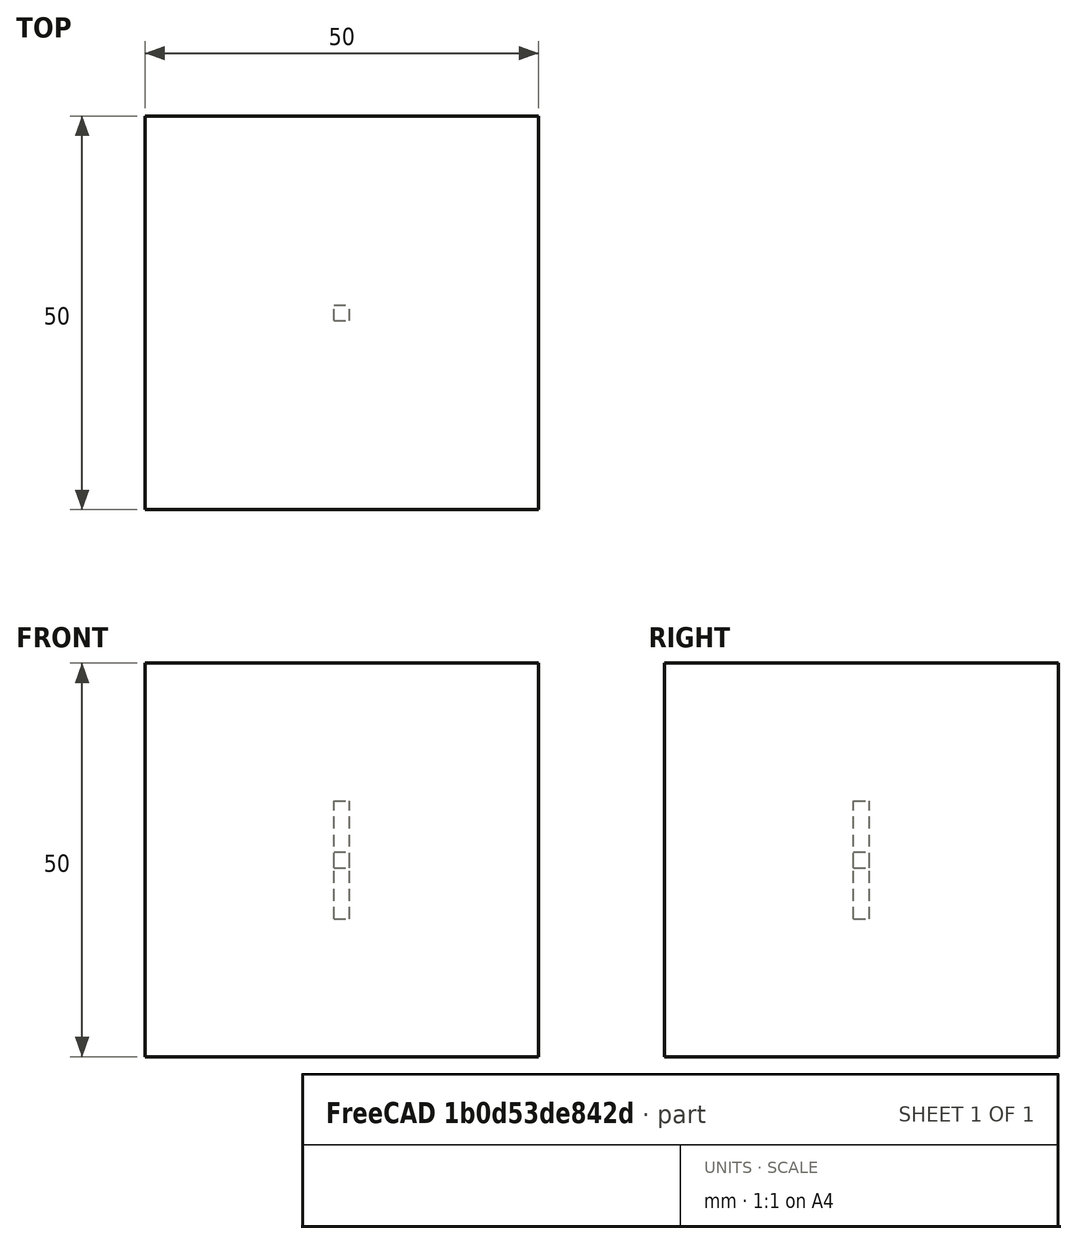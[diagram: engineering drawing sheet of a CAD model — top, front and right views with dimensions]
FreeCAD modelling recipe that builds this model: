
FCSTD DOCUMENT  (FreeCAD 0.20R29177 (Git))
Label: Expanded_simple_array
License: All rights reserved
LicenseURL: http://en.wikipedia.org/wiki/All_rights_reserved
objects: App::DocumentObjectGroupPython×1269, Part::FeaturePython×6, App::Part×6, App::Link×4, App::FeaturePython×2
note: 5 computed .brp shape members not serialized (recipe doc carries the construction recipe); baked Part::Feature solids carry a one-line shape summary decoded from their .brp

FEATURE [App::DocumentObjectGroupPython] Constants  # scripted group (container) (typed FeaturePython)
FEATURE [App::DocumentObjectGroupPython] Variables  # scripted group (container) (typed FeaturePython)
FEATURE [App::DocumentObjectGroupPython] Quantities  # scripted group (container) (typed FeaturePython)
FEATURE [App::DocumentObjectGroupPython] Isotopes  # scripted group (container) (typed FeaturePython)
FEATURE [App::DocumentObjectGroupPython] Elements  # scripted group (container) (typed FeaturePython)
FEATURE [App::DocumentObjectGroupPython] G4_CESIUM_IODIDE  label="G4_CESIUM_IODIDE : 1.000"  # scripted group (container) (typed FeaturePython)
  n = 1
FEATURE [App::DocumentObjectGroupPython] LYSO  # scripted group (container) (typed FeaturePython)
  ABSLENGTH = ABSLENGTHLAR
  Dunit = g/cm3
  Dvalue = 7.1
  FASTCOMPONENT = SCINTLAR
  Group = -> [G4_CESIUM_IODIDE]
  RAYLEIGH = RAYLEIGHLAR
  REEMISSIONPROB = SCINTLAR
  RESOLUTIONSCALE = RS
  RINDEX = RINDEXLAR
  SCINTILLATIONCOMPONENT1 = SCINTLAR
  SCINTILLATIONCOMPONENT2 = SCINTLAR
  SCINTILLATIONTIMECONSTANT1 = FTC
  SCINTILLATIONTIMECONSTANT2 = STC
  SCINTILLATIONYIELD = SY
  SCINTILLATIONYIELD1 = RY1
  SCINTILLATIONYIELD2 = RY2
  SLOWCOMPONENT = SCINTLAR
  YIELDRATIO = YR
  conduct = 2
  density = 1
  expand = 3
  name = LYSO
  specific = 4
FEATURE [App::DocumentObjectGroupPython] G4_AIR  label="G4_AIR : 1.000"  # scripted group (container) (typed FeaturePython)
  n = 1
FEATURE [App::DocumentObjectGroupPython] Air  # scripted group (container) (typed FeaturePython)
  Dunit = mg/cm3
  Dvalue = 1.29
  Group = -> [G4_AIR]
  RINDEX = AirRINDEX
  conduct = 2
  density = 1
  expand = 3
  name = Air
  specific = 4
FEATURE [App::DocumentObjectGroupPython] G4_SILICON_DIOXIDE  label="G4_SILICON_DIOXIDE : 1.000"  # scripted group (container) (typed FeaturePython)
  n = 1
FEATURE [App::DocumentObjectGroupPython] Glass  # scripted group (container) (typed FeaturePython)
  Dunit = g/cm3
  Dvalue = 2.32
  Group = -> [G4_SILICON_DIOXIDE]
  RINDEX = RINDEXLAR
  conduct = 2
  density = 1
  expand = 3
  name = Glass
  specific = 4
FEATURE [App::DocumentObjectGroupPython] SY  # scripted group (container) (typed FeaturePython)
  coldim = 1
  values = 100000
FEATURE [App::DocumentObjectGroupPython] RS  # scripted group (container) (typed FeaturePython)
  coldim = 1
  values = 1
FEATURE [App::DocumentObjectGroupPython] FTC  # scripted group (container) (typed FeaturePython)
  coldim = 1
  values = 21.5*ns
FEATURE [App::DocumentObjectGroupPython] STC  # scripted group (container) (typed FeaturePython)
  coldim = 1
  values = 43.8*ns
FEATURE [App::DocumentObjectGroupPython] RY1  # scripted group (container) (typed FeaturePython)
  coldim = 1
  values = 95
FEATURE [App::DocumentObjectGroupPython] RY2  # scripted group (container) (typed FeaturePython)
  coldim = 1
  values = 5
FEATURE [App::DocumentObjectGroupPython] YR  # scripted group (container) (typed FeaturePython)
  coldim = 1
  values = 0.8
FEATURE [App::DocumentObjectGroupPython] SCINTLAR  # scripted group (container) (typed FeaturePython)
  coldim = 2
  values = <blob: 2358 chars omitted>
FEATURE [App::DocumentObjectGroupPython] RINDEXLAR  # scripted group (container) (typed FeaturePython)
  coldim = 2
  values = <blob: 9384 chars omitted>
FEATURE [App::DocumentObjectGroupPython] ABSLENGTHLAR  # scripted group (container) (typed FeaturePython)
  coldim = 2
  values = 7.74901*eV 10.0*m 7.77525*eV 10.0*m 7.80167*eV 10.0*m 7.82827*eV 10.0*m 7.85506*eV 10.0*m 7.88202*eV 10.0*m 7.90917*eV 10.0*m 7.93651*eV 10.0*m 7.96404*eV 10.0*m 7.99176*eV 10.0*m 8.01968*eV 10.0*m 8.04779*eV 10.0*m 8.07609*eV 10.0*m 8.1046*eV 10.0*m 8.13331*eV 10.0*m 8.16222*eV 10.0*m 8.19134*eV 10.0*m 8.22067*eV 10.0*m 8.25021*eV 10.0*m 8.27996*eV 10.0*m 8.30993*eV 10.0*m 8.34012*eV 10.0*m 8.37052*eV 10.0*m 8.40115*eV 10.0*m 8.432*eV 10.0*m 8.46308*eV 10.0*m 8.4944*eV 10.0*m 8.52594*eV 10.0*m 8.55772*eV 10.0*m 8.58973*eV 10.0*m 8.62199*eV 10.0*m 8.65449*eV 10.0*m 8.68723*eV 10.0*m 8.72023*eV 10.0*m 8.75347*eV 10.0*m 8.78697*eV 10.0*m 8.82073*eV 10.0*m 8.85475*eV 10.0*m 8.88903*eV 10.0*m 8.92358*eV 10.0*m 8.9584*eV 10.0*m 8.99349*eV 10.0*m 9.02885*eV 10.0*m 9.0645*eV 10.0*m 9.10043*eV 10.0*m 9.13664*eV 10.0*m 9.17314*eV 10.0*m 9.20994*eV 10.0*m 9.24703*eV 10.0*m 9.28442*eV 10.0*m 9.32212*eV 10.0*m 9.36012*eV 10.0*m 9.39844*eV 10.0*m 9.43707*eV 10.0*m 9.47602*eV 10.0*m 9.51529*eV 10.0*m 9.55489*eV 10.0*m 9.59481*eV 10.0*m 9.63508*eV 10.0*m 9.67568*eV 10.0*m 9.71663*eV 10.0*m 9.75792*eV 10.0*m 9.79957*eV 10.0*m 9.84158*eV 10.0*m 9.88394*eV 10.0*m 9.92668*eV 10.0*m 9.96978*eV 10.0*m 10.0133*eV 10.0*m 10.0571*eV 10.0*m 10.1014*eV 10.0*m 10.146*eV 10.0*m 10.191*eV 10.0*m 10.2365*eV 10.0*m 10.2823*eV 10.0*m 10.3286*eV 10.0*m 10.3752*eV 10.0*m 10.4223*eV 10.0*m 10.4699*eV 10.0*m 10.5178*eV 10.0*m 10.5662*eV 10.0*m 10.6151*eV 10.0*m 10.6644*eV 10.0*m 10.7142*eV 10.0*m 10.7644*eV 10.0*m 10.8151*eV 10.0*m 10.8663*eV 10.0*m 10.9179*eV 10.0*m 10.9701*eV 10.0*m 11.0228*eV 10.0*m 11.076*eV 10.0*m 11.1296*eV 10.0*m 11.1839*eV 10.0*m 11.2386*eV 10.0*m 11.2939*eV 10.0*m 11.3497*eV 10.0*m 11.4061*eV 10.0*m 11.463*eV 10.0*m 11.5206*eV 10.0*m 11.5787*eV 10.0*m 11.6373*eV 10.0*m
FEATURE [App::DocumentObjectGroupPython] RAYLEIGHLAR  # scripted group (container) (typed FeaturePython)
  coldim = 2
  values = 7.74901*eV 90.0*cm 7.77525*eV 90.0*cm 7.80167*eV 90.0*cm 7.82827*eV 90.0*cm 7.85506*eV 90.0*cm 7.88202*eV 90.0*cm 7.90917*eV 90.0*cm 7.93651*eV 90.0*cm 7.96404*eV 90.0*cm 7.99176*eV 90.0*cm 8.01968*eV 90.0*cm 8.04779*eV 90.0*cm 8.07609*eV 90.0*cm 8.1046*eV 90.0*cm 8.13331*eV 90.0*cm 8.16222*eV 90.0*cm 8.19134*eV 90.0*cm 8.22067*eV 90.0*cm 8.25021*eV 90.0*cm 8.27996*eV 90.0*cm 8.30993*eV 90.0*cm 8.34012*eV 90.0*cm 8.37052*eV 90.0*cm 8.40115*eV 90.0*cm 8.432*eV 90.0*cm 8.46308*eV 90.0*cm 8.4944*eV 90.0*cm 8.52594*eV 90.0*cm 8.55772*eV 90.0*cm 8.58973*eV 90.0*cm 8.62199*eV 90.0*cm 8.65449*eV 90.0*cm 8.68723*eV 90.0*cm 8.72023*eV 90.0*cm 8.75347*eV 90.0*cm 8.78697*eV 90.0*cm 8.82073*eV 90.0*cm 8.85475*eV 90.0*cm 8.88903*eV 90.0*cm 8.92358*eV 90.0*cm 8.9584*eV 90.0*cm 8.99349*eV 90.0*cm 9.02885*eV 90.0*cm 9.0645*eV 90.0*cm 9.10043*eV 90.0*cm 9.13664*eV 90.0*cm 9.17314*eV 90.0*cm 9.20994*eV 90.0*cm 9.24703*eV 90.0*cm 9.28442*eV 90.0*cm 9.32212*eV 90.0*cm 9.36012*eV 90.0*cm 9.39844*eV 90.0*cm 9.43707*eV 90.0*cm 9.47602*eV 90.0*cm 9.51529*eV 90.0*cm 9.55489*eV 90.0*cm 9.59481*eV 90.0*cm 9.63508*eV 90.0*cm 9.67568*eV 90.0*cm 9.71663*eV 90.0*cm 9.75792*eV 90.0*cm 9.79957*eV 90.0*cm 9.84158*eV 90.0*cm 9.88394*eV 90.0*cm 9.92668*eV 90.0*cm 9.96978*eV 90.0*cm 10.0133*eV 90.0*cm 10.0571*eV 90.0*cm 10.1014*eV 90.0*cm 10.146*eV 90.0*cm 10.191*eV 90.0*cm 10.2365*eV 90.0*cm 10.2823*eV 90.0*cm 10.3286*eV 90.0*cm 10.3752*eV 90.0*cm 10.4223*eV 90.0*cm 10.4699*eV 90.0*cm 10.5178*eV 90.0*cm 10.5662*eV 90.0*cm 10.6151*eV 90.0*cm 10.6644*eV 90.0*cm 10.7142*eV 90.0*cm 10.7644*eV 90.0*cm 10.8151*eV 90.0*cm 10.8663*eV 90.0*cm 10.9179*eV 90.0*cm 10.9701*eV 90.0*cm 11.0228*eV 90.0*cm 11.076*eV 90.0*cm 11.1296*eV 90.0*cm 11.1839*eV 90.0*cm 11.2386*eV 90.0*cm 11.2939*eV 90.0*cm 11.3497*eV 90.0*cm 11.4061*eV 90.0*cm 11.463*eV 90.0*cm 11.5206*eV 90.0*cm 11.5787*eV 90.0*cm 11.6373*eV 90.0*cm
FEATURE [App::DocumentObjectGroupPython] REFLECTIVITY  # scripted group (container) (typed FeaturePython)
  coldim = 2
  values = 2.034*eV 0.98 2.068*eV 0.98 2.103*eV 0.98 2.139*eV 0.98 2.177*eV 0.98 2.216*eV 0.98 2.256*eV 0.98 2.298*eV 0.98 2.341*eV 0.98 2.386*eV 0.98 2.433*eV 0.98 2.481*eV 0.98 2.532*eV 0.98 2.585*eV 0.98 2.64*eV 0.98 2.697*eV 0.98 2.757*eV 0.98 2.82*eV 0.98 2.885*eV 0.98 2.954*eV 0.98 3.026*eV 0.98 3.102*eV 0.98 3.181*eV 0.98 3.265*eV 0.98 3.353*eV 0.98 3.446*eV 0.98 3.545*eV 0.98 3.649*eV 0.98 3.76*eV 0.98 3.877*eV 0.98 4.002*eV 0.98 4.136*eV 0.98 5.0*eV 0.98 6.0*eV 0.98 7.0*eV 0.98 8.0*eV 0.98 9.0*eV 0.98 9.0*eV 0.98 10.0*eV 0.98 11.0*eV 0.98 11.6*eV 0.98
FEATURE [App::DocumentObjectGroupPython] EFFICIENCY  # scripted group (container) (typed FeaturePython)
  coldim = 2
  values = 2.034*eV 1 2.068*eV 1 2.103*eV 1 2.139*eV 1 2.177*eV 1 2.216*eV 1 2.256*eV 1 2.298*eV 1 2.341*eV 1 2.386*eV 1 2.433*eV 1 2.481*eV 1 2.532*eV 1 2.585*eV 1 2.64*eV 1 2.697*eV 1 2.757*eV 1 2.82*eV 1 2.885*eV 1 2.954*eV 1 3.026*eV 1 3.102*eV 1 3.181*eV  1 3.265*eV 1 3.353*eV 1 3.446*eV 1 3.545*eV 1 3.649*eV 1 3.76*eV 1 3.877*eV 1 4.002*eV 1 4.136*eV 1 5.0*eV 1 6.0*eV 1 7.0*eV 1 8.0*eV 1 9.0*eV 1 9.0*eV 1 10.0*eV 1 11.0*eV 1 11.6*eV 1
FEATURE [App::DocumentObjectGroupPython] AirRINDEX  # scripted group (container) (typed FeaturePython)
  coldim = 2
  values = 2.034*eV 1 2.068*eV 1 2.103*eV 1 2.139*eV 1 2.177*eV 1 2.216*eV 1 2.256*eV 1 2.298*eV 1 2.341*eV 1 2.386*eV 1 2.433*eV 1 2.481*eV 1 2.532*eV 1 2.585*eV 1 2.64*eV 1 2.697*eV 1 2.757*eV 1 2.82*eV 1 2.885*eV 1 2.954*eV 1 3.026*eV 1 3.102*eV 1 3.181*eV 1 3.265*eV 1 3.353*eV 1 3.446*eV 1 3.545*eV 1 3.649*eV 1 3.76*eV 1 3.877*eV 1 4.002*eV 1 4.136*eV 1 5.0*eV 1 6.0*eV 1 7.0*eV 1 8.0*eV 1 9.0*eV 1 10.0*eV 1 11.0*eV 1 11.6*eV 1
FEATURE [App::DocumentObjectGroupPython] Matrix  # scripted group (container) (typed FeaturePython)
  Group = -> [SY,RS,FTC,STC,RY1,RY2,YR,SCINTLAR,RINDEXLAR,ABSLENGTHLAR,RAYLEIGHLAR,REFLECTIVITY,EFFICIENCY,AirRINDEX]
FEATURE [App::DocumentObjectGroupPython] ScintWrap  # scripted group (container) (typed FeaturePython)
  EFFICIENCY = EFFICIENCY
  REFLECTIVITY = REFLECTIVITY
  finish = 39
  model = 0
  type = 2
  value = 1
FEATURE [App::DocumentObjectGroupPython] Surfaces  # scripted group (container) (typed FeaturePython)
  Group = -> [ScintWrap]
FEATURE [App::DocumentObjectGroupPython] Opticals  # scripted group (container) (typed FeaturePython)
  Group = -> [Matrix,Surfaces]
FEATURE [App::DocumentObjectGroupPython] G4Isotopes  # scripted group (container) (typed FeaturePython)
FEATURE [App::DocumentObjectGroupPython] H_element  # scripted group (container) (typed FeaturePython)
  Z = 1
  atom_value = 1.008
  formula = H
  name = H_element
FEATURE [App::DocumentObjectGroupPython] He_element  # scripted group (container) (typed FeaturePython)
  Z = 2
  atom_value = 4.0026
  formula = He
  name = He_element
FEATURE [App::DocumentObjectGroupPython] Li_element  # scripted group (container) (typed FeaturePython)
  Z = 3
  atom_value = 6.94
  formula = Li
  name = Li_element
FEATURE [App::DocumentObjectGroupPython] Be_element  # scripted group (container) (typed FeaturePython)
  Z = 4
  atom_value = 9.01218
  formula = Be
  name = Be_element
FEATURE [App::DocumentObjectGroupPython] B_element  # scripted group (container) (typed FeaturePython)
  Z = 5
  atom_value = 10.81
  formula = B
  name = B_element
FEATURE [App::DocumentObjectGroupPython] C_element  # scripted group (container) (typed FeaturePython)
  Z = 6
  atom_value = 12.011
  formula = C
  name = C_element
FEATURE [App::DocumentObjectGroupPython] N_element  # scripted group (container) (typed FeaturePython)
  Z = 7
  atom_value = 14.007
  formula = N
  name = N_element
FEATURE [App::DocumentObjectGroupPython] O_element  # scripted group (container) (typed FeaturePython)
  Z = 8
  atom_value = 15.999
  formula = O
  name = O_element
FEATURE [App::DocumentObjectGroupPython] F_element  # scripted group (container) (typed FeaturePython)
  Z = 9
  atom_value = 18.9984
  formula = F
  name = F_element
FEATURE [App::DocumentObjectGroupPython] Ne_element  # scripted group (container) (typed FeaturePython)
  Z = 10
  atom_value = 20.1797
  formula = Ne
  name = Ne_element
FEATURE [App::DocumentObjectGroupPython] Na_element  # scripted group (container) (typed FeaturePython)
  Z = 11
  atom_value = 22.9898
  formula = Na
  name = Na_element
FEATURE [App::DocumentObjectGroupPython] Mg_element  # scripted group (container) (typed FeaturePython)
  Z = 12
  atom_value = 24.305
  formula = Mg
  name = Mg_element
FEATURE [App::DocumentObjectGroupPython] Al_element  # scripted group (container) (typed FeaturePython)
  Z = 13
  atom_value = 26.9815
  formula = Al
  name = Al_element
FEATURE [App::DocumentObjectGroupPython] Si_element  # scripted group (container) (typed FeaturePython)
  Z = 14
  atom_value = 28.085
  formula = Si
  name = Si_element
FEATURE [App::DocumentObjectGroupPython] P_element  # scripted group (container) (typed FeaturePython)
  Z = 15
  atom_value = 30.9738
  formula = P
  name = P_element
FEATURE [App::DocumentObjectGroupPython] S_element  # scripted group (container) (typed FeaturePython)
  Z = 16
  atom_value = 32.06
  formula = S
  name = S_element
FEATURE [App::DocumentObjectGroupPython] Cl_element  # scripted group (container) (typed FeaturePython)
  Z = 17
  atom_value = 35.45
  formula = Cl
  name = Cl_element
FEATURE [App::DocumentObjectGroupPython] Ar_element  # scripted group (container) (typed FeaturePython)
  Z = 18
  atom_value = 39.95
  formula = Ar
  name = Ar_element
FEATURE [App::DocumentObjectGroupPython] K_element  # scripted group (container) (typed FeaturePython)
  Z = 19
  atom_value = 39.0983
  formula = K
  name = K_element
FEATURE [App::DocumentObjectGroupPython] Ca_element  # scripted group (container) (typed FeaturePython)
  Z = 20
  atom_value = 40.078
  formula = Ca
  name = Ca_element
FEATURE [App::DocumentObjectGroupPython] Sc_element  # scripted group (container) (typed FeaturePython)
  Z = 21
  atom_value = 44.9559
  formula = Sc
  name = Sc_element
FEATURE [App::DocumentObjectGroupPython] Ti_element  # scripted group (container) (typed FeaturePython)
  Z = 22
  atom_value = 47.867
  formula = Ti
  name = Ti_element
FEATURE [App::DocumentObjectGroupPython] V_element  # scripted group (container) (typed FeaturePython)
  Z = 23
  atom_value = 50.9415
  formula = V
  name = V_element
FEATURE [App::DocumentObjectGroupPython] Cr_element  # scripted group (container) (typed FeaturePython)
  Z = 24
  atom_value = 51.9961
  formula = Cr
  name = Cr_element
FEATURE [App::DocumentObjectGroupPython] Mn_element  # scripted group (container) (typed FeaturePython)
  Z = 25
  atom_value = 54.938
  formula = Mn
  name = Mn_element
FEATURE [App::DocumentObjectGroupPython] Fe_element  # scripted group (container) (typed FeaturePython)
  Z = 26
  atom_value = 55.845
  formula = Fe
  name = Fe_element
FEATURE [App::DocumentObjectGroupPython] Co_element  # scripted group (container) (typed FeaturePython)
  Z = 27
  atom_value = 58.9332
  formula = Co
  name = Co_element
FEATURE [App::DocumentObjectGroupPython] Ni_element  # scripted group (container) (typed FeaturePython)
  Z = 28
  atom_value = 58.6934
  formula = Ni
  name = Ni_element
FEATURE [App::DocumentObjectGroupPython] Cu_element  # scripted group (container) (typed FeaturePython)
  Z = 29
  atom_value = 63.546
  formula = Cu
  name = Cu_element
FEATURE [App::DocumentObjectGroupPython] Zn_element  # scripted group (container) (typed FeaturePython)
  Z = 30
  atom_value = 65.38
  formula = Zn
  name = Zn_element
FEATURE [App::DocumentObjectGroupPython] Ga_element  # scripted group (container) (typed FeaturePython)
  Z = 31
  atom_value = 69.723
  formula = Ga
  name = Ga_element
FEATURE [App::DocumentObjectGroupPython] Ge_element  # scripted group (container) (typed FeaturePython)
  Z = 32
  atom_value = 72.63
  formula = Ge
  name = Ge_element
FEATURE [App::DocumentObjectGroupPython] As_element  # scripted group (container) (typed FeaturePython)
  Z = 33
  atom_value = 74.9216
  formula = As
  name = As_element
FEATURE [App::DocumentObjectGroupPython] Se_element  # scripted group (container) (typed FeaturePython)
  Z = 34
  atom_value = 78.971
  formula = Se
  name = Se_element
FEATURE [App::DocumentObjectGroupPython] Br_element  # scripted group (container) (typed FeaturePython)
  Z = 35
  atom_value = 79.904
  formula = Br
  name = Br_element
FEATURE [App::DocumentObjectGroupPython] Kr_element  # scripted group (container) (typed FeaturePython)
  Z = 36
  atom_value = 83.798
  formula = Kr
  name = Kr_element
FEATURE [App::DocumentObjectGroupPython] Rb_element  # scripted group (container) (typed FeaturePython)
  Z = 37
  atom_value = 85.4678
  formula = Rb
  name = Rb_element
FEATURE [App::DocumentObjectGroupPython] Sr_element  # scripted group (container) (typed FeaturePython)
  Z = 38
  atom_value = 87.62
  formula = Sr
  name = Sr_element
FEATURE [App::DocumentObjectGroupPython] Y_element  # scripted group (container) (typed FeaturePython)
  Z = 39
  atom_value = 88.9058
  formula = Y
  name = Y_element
FEATURE [App::DocumentObjectGroupPython] Zr_element  # scripted group (container) (typed FeaturePython)
  Z = 40
  atom_value = 91.224
  formula = Zr
  name = Zr_element
FEATURE [App::DocumentObjectGroupPython] Nb_element  # scripted group (container) (typed FeaturePython)
  Z = 41
  atom_value = 92.9064
  formula = Nb
  name = Nb_element
FEATURE [App::DocumentObjectGroupPython] Mo_element  # scripted group (container) (typed FeaturePython)
  Z = 42
  atom_value = 95.95
  formula = Mo
  name = Mo_element
FEATURE [App::DocumentObjectGroupPython] Tc_element  # scripted group (container) (typed FeaturePython)
  Z = 43
  atom_value = 97
  formula = Tc
  name = Tc_element
FEATURE [App::DocumentObjectGroupPython] Ru_element  # scripted group (container) (typed FeaturePython)
  Z = 44
  atom_value = 101.07
  formula = Ru
  name = Ru_element
FEATURE [App::DocumentObjectGroupPython] Rh_element  # scripted group (container) (typed FeaturePython)
  Z = 45
  atom_value = 102.905
  formula = Rh
  name = Rh_element
FEATURE [App::DocumentObjectGroupPython] Pd_element  # scripted group (container) (typed FeaturePython)
  Z = 46
  atom_value = 106.42
  formula = Pd
  name = Pd_element
FEATURE [App::DocumentObjectGroupPython] Ag_element  # scripted group (container) (typed FeaturePython)
  Z = 47
  atom_value = 107.868
  formula = Ag
  name = Ag_element
FEATURE [App::DocumentObjectGroupPython] Cd_element  # scripted group (container) (typed FeaturePython)
  Z = 48
  atom_value = 112.414
  formula = Cd
  name = Cd_element
FEATURE [App::DocumentObjectGroupPython] In_element  # scripted group (container) (typed FeaturePython)
  Z = 49
  atom_value = 114.818
  formula = In
  name = In_element
FEATURE [App::DocumentObjectGroupPython] Sn_element  # scripted group (container) (typed FeaturePython)
  Z = 50
  atom_value = 118.71
  formula = Sn
  name = Sn_element
FEATURE [App::DocumentObjectGroupPython] Sb_element  # scripted group (container) (typed FeaturePython)
  Z = 51
  atom_value = 121.76
  formula = Sb
  name = Sb_element
FEATURE [App::DocumentObjectGroupPython] Te_element  # scripted group (container) (typed FeaturePython)
  Z = 52
  atom_value = 127.6
  formula = Te
  name = Te_element
FEATURE [App::DocumentObjectGroupPython] I_element  # scripted group (container) (typed FeaturePython)
  Z = 53
  atom_value = 126.904
  formula = I
  name = I_element
FEATURE [App::DocumentObjectGroupPython] Xe_element  # scripted group (container) (typed FeaturePython)
  Z = 54
  atom_value = 131.293
  formula = Xe
  name = Xe_element
FEATURE [App::DocumentObjectGroupPython] Cs_element  # scripted group (container) (typed FeaturePython)
  Z = 55
  atom_value = 132.905
  formula = Cs
  name = Cs_element
FEATURE [App::DocumentObjectGroupPython] Ba_element  # scripted group (container) (typed FeaturePython)
  Z = 56
  atom_value = 137.327
  formula = Ba
  name = Ba_element
FEATURE [App::DocumentObjectGroupPython] La_element  # scripted group (container) (typed FeaturePython)
  Z = 57
  atom_value = 138.905
  formula = La
  name = La_element
FEATURE [App::DocumentObjectGroupPython] Ce_element  # scripted group (container) (typed FeaturePython)
  Z = 58
  atom_value = 140.116
  formula = Ce
  name = Ce_element
FEATURE [App::DocumentObjectGroupPython] Pr_element  # scripted group (container) (typed FeaturePython)
  Z = 59
  atom_value = 140.908
  formula = Pr
  name = Pr_element
FEATURE [App::DocumentObjectGroupPython] Nd_element  # scripted group (container) (typed FeaturePython)
  Z = 60
  atom_value = 144.242
  formula = Nd
  name = Nd_element
FEATURE [App::DocumentObjectGroupPython] Pm_element  # scripted group (container) (typed FeaturePython)
  Z = 61
  atom_value = 145
  formula = Pm
  name = Pm_element
FEATURE [App::DocumentObjectGroupPython] Sm_element  # scripted group (container) (typed FeaturePython)
  Z = 62
  atom_value = 150.36
  formula = Sm
  name = Sm_element
FEATURE [App::DocumentObjectGroupPython] Eu_element  # scripted group (container) (typed FeaturePython)
  Z = 63
  atom_value = 151.964
  formula = Eu
  name = Eu_element
FEATURE [App::DocumentObjectGroupPython] Gd_element  # scripted group (container) (typed FeaturePython)
  Z = 64
  atom_value = 157.25
  formula = Gd
  name = Gd_element
FEATURE [App::DocumentObjectGroupPython] Tb_element  # scripted group (container) (typed FeaturePython)
  Z = 65
  atom_value = 158.925
  formula = Tb
  name = Tb_element
FEATURE [App::DocumentObjectGroupPython] Dy_element  # scripted group (container) (typed FeaturePython)
  Z = 66
  atom_value = 162.5
  formula = Dy
  name = Dy_element
FEATURE [App::DocumentObjectGroupPython] Ho_element  # scripted group (container) (typed FeaturePython)
  Z = 67
  atom_value = 164.93
  formula = Ho
  name = Ho_element
FEATURE [App::DocumentObjectGroupPython] Er_element  # scripted group (container) (typed FeaturePython)
  Z = 68
  atom_value = 167.259
  formula = Er
  name = Er_element
FEATURE [App::DocumentObjectGroupPython] Tm_element  # scripted group (container) (typed FeaturePython)
  Z = 69
  atom_value = 168.934
  formula = Tm
  name = Tm_element
FEATURE [App::DocumentObjectGroupPython] Yb_element  # scripted group (container) (typed FeaturePython)
  Z = 70
  atom_value = 173.045
  formula = Yb
  name = Yb_element
FEATURE [App::DocumentObjectGroupPython] Lu_element  # scripted group (container) (typed FeaturePython)
  Z = 71
  atom_value = 174.967
  formula = Lu
  name = Lu_element
FEATURE [App::DocumentObjectGroupPython] Hf_element  # scripted group (container) (typed FeaturePython)
  Z = 72
  atom_value = 178.49
  formula = Hf
  name = Hf_element
FEATURE [App::DocumentObjectGroupPython] Ta_element  # scripted group (container) (typed FeaturePython)
  Z = 73
  atom_value = 180.948
  formula = Ta
  name = Ta_element
FEATURE [App::DocumentObjectGroupPython] W_element  # scripted group (container) (typed FeaturePython)
  Z = 74
  atom_value = 183.84
  formula = W
  name = W_element
FEATURE [App::DocumentObjectGroupPython] Re_element  # scripted group (container) (typed FeaturePython)
  Z = 75
  atom_value = 186.207
  formula = Re
  name = Re_element
FEATURE [App::DocumentObjectGroupPython] Os_element  # scripted group (container) (typed FeaturePython)
  Z = 76
  atom_value = 190.23
  formula = Os
  name = Os_element
FEATURE [App::DocumentObjectGroupPython] Ir_element  # scripted group (container) (typed FeaturePython)
  Z = 77
  atom_value = 192.217
  formula = Ir
  name = Ir_element
FEATURE [App::DocumentObjectGroupPython] Pt_element  # scripted group (container) (typed FeaturePython)
  Z = 78
  atom_value = 195.084
  formula = Pt
  name = Pt_element
FEATURE [App::DocumentObjectGroupPython] Au_element  # scripted group (container) (typed FeaturePython)
  Z = 79
  atom_value = 196.967
  formula = Au
  name = Au_element
FEATURE [App::DocumentObjectGroupPython] Hg_element  # scripted group (container) (typed FeaturePython)
  Z = 80
  atom_value = 200.592
  formula = Hg
  name = Hg_element
FEATURE [App::DocumentObjectGroupPython] Tl_element  # scripted group (container) (typed FeaturePython)
  Z = 81
  atom_value = 204.38
  formula = Tl
  name = Tl_element
FEATURE [App::DocumentObjectGroupPython] Pb_element  # scripted group (container) (typed FeaturePython)
  Z = 82
  atom_value = 207.2
  formula = Pb
  name = Pb_element
FEATURE [App::DocumentObjectGroupPython] Bi_element  # scripted group (container) (typed FeaturePython)
  Z = 83
  atom_value = 208.98
  formula = Bi
  name = Bi_element
FEATURE [App::DocumentObjectGroupPython] Po_element  # scripted group (container) (typed FeaturePython)
  Z = 84
  atom_value = 209
  formula = Po
  name = Po_element
FEATURE [App::DocumentObjectGroupPython] At_element  # scripted group (container) (typed FeaturePython)
  Z = 85
  atom_value = 210
  formula = At
  name = At_element
FEATURE [App::DocumentObjectGroupPython] Rn_element  # scripted group (container) (typed FeaturePython)
  Z = 86
  atom_value = 222
  formula = Rn
  name = Rn_element
FEATURE [App::DocumentObjectGroupPython] Fr_element  # scripted group (container) (typed FeaturePython)
  Z = 87
  atom_value = 223
  formula = Fr
  name = Fr_element
FEATURE [App::DocumentObjectGroupPython] Ra_element  # scripted group (container) (typed FeaturePython)
  Z = 88
  atom_value = 226
  formula = Ra
  name = Ra_element
FEATURE [App::DocumentObjectGroupPython] Ac_element  # scripted group (container) (typed FeaturePython)
  Z = 89
  atom_value = 227
  formula = Ac
  name = Ac_element
FEATURE [App::DocumentObjectGroupPython] Th_element  # scripted group (container) (typed FeaturePython)
  Z = 90
  atom_value = 232.038
  formula = Th
  name = Th_element
FEATURE [App::DocumentObjectGroupPython] Pa_element  # scripted group (container) (typed FeaturePython)
  Z = 91
  atom_value = 231.036
  formula = Pa
  name = Pa_element
FEATURE [App::DocumentObjectGroupPython] U_element  # scripted group (container) (typed FeaturePython)
  Z = 92
  atom_value = 238.029
  formula = U
  name = U_element
FEATURE [App::DocumentObjectGroupPython] Np_element  # scripted group (container) (typed FeaturePython)
  Z = 93
  atom_value = 237
  formula = Np
  name = Np_element
FEATURE [App::DocumentObjectGroupPython] Pu_element  # scripted group (container) (typed FeaturePython)
  Z = 94
  atom_value = 244
  formula = Pu
  name = Pu_element
FEATURE [App::DocumentObjectGroupPython] Am_element  # scripted group (container) (typed FeaturePython)
  Z = 95
  atom_value = 243
  formula = Am
  name = Am_element
FEATURE [App::DocumentObjectGroupPython] Cm_element  # scripted group (container) (typed FeaturePython)
  Z = 96
  atom_value = 247
  formula = Cm
  name = Cm_element
FEATURE [App::DocumentObjectGroupPython] Bk_element  # scripted group (container) (typed FeaturePython)
  Z = 97
  atom_value = 247
  formula = Bk
  name = Bk_element
FEATURE [App::DocumentObjectGroupPython] Cf_element  # scripted group (container) (typed FeaturePython)
  Z = 98
  atom_value = 251
  formula = Cf
  name = Cf_element
FEATURE [App::DocumentObjectGroupPython] G4Elements  # scripted group (container) (typed FeaturePython)
  Group = -> [H_element,He_element,Li_element,Be_element,B_element,C_element,N_element,O_element,F_element,Ne_element,Na_element,Mg_element,Al_element,Si_element,P_element,S_element,Cl_element,Ar_element,K_element,Ca_element,Sc_element,Ti_element,V_element,Cr_element,Mn_element,Fe_element,Co_element,Ni_element,Cu_element,Zn_element,Ga_element,Ge_element,As_element,Se_element,Br_element,Kr_element,Rb_element,+61 more]
FEATURE [App::DocumentObjectGroupPython] H_element001  label="H_element : 0.101"  # scripted group (container) (typed FeaturePython)
  n = 0.101327
FEATURE [App::DocumentObjectGroupPython] C_element001  label="C_element : 0.775"  # scripted group (container) (typed FeaturePython)
  n = 0.7755
FEATURE [App::DocumentObjectGroupPython] N_element001  label="N_element : 0.035"  # scripted group (container) (typed FeaturePython)
  n = 0.035057
FEATURE [App::DocumentObjectGroupPython] O_element001  label="O_element : 0.052"  # scripted group (container) (typed FeaturePython)
  n = 0.0523159
FEATURE [App::DocumentObjectGroupPython] F_element001  label="F_element : 0.017"  # scripted group (container) (typed FeaturePython)
  n = 0.017422
FEATURE [App::DocumentObjectGroupPython] Ca_element001  label="Ca_element : 0.018"  # scripted group (container) (typed FeaturePython)
  n = 0.018378
FEATURE [App::DocumentObjectGroupPython] G4_A_150_TISSUE  label="G4_A-150_TISSUE"  # scripted group (container) (typed FeaturePython)
  Dunit = g/cm3
  Dvalue = 1.127
  Group = -> [H_element001,C_element001,N_element001,O_element001,F_element001,Ca_element001]
  conduct = 2
  density = 1
  expand = 3
  formula = G4_A-150_TISSUE
  name = G4_A-150_TISSUE
  specific = 4
FEATURE [App::DocumentObjectGroupPython] C_element002  label="C_element : 3"  # scripted group (container) (typed FeaturePython)
  n = 3
  ref = C_element
FEATURE [App::DocumentObjectGroupPython] H_element002  label="H_element : 6"  # scripted group (container) (typed FeaturePython)
  n = 6
  ref = H_element
FEATURE [App::DocumentObjectGroupPython] O_element002  label="O_element : 1"  # scripted group (container) (typed FeaturePython)
  n = 1
  ref = O_element
FEATURE [App::DocumentObjectGroupPython] G4_ACETONE  # scripted group (container) (typed FeaturePython)
  Dunit = g/cm3
  Dvalue = 0.7899
  Group = -> [C_element002,H_element002,O_element002]
  conduct = 2
  density = 1
  expand = 3
  formula = G4_ACETONE
  name = G4_ACETONE
  specific = 4
FEATURE [App::DocumentObjectGroupPython] C_element003  label="C_element : 2"  # scripted group (container) (typed FeaturePython)
  n = 2
  ref = C_element
FEATURE [App::DocumentObjectGroupPython] H_element003  label="H_element : 2"  # scripted group (container) (typed FeaturePython)
  n = 2
  ref = H_element
FEATURE [App::DocumentObjectGroupPython] G4_ACETYLENE  # scripted group (container) (typed FeaturePython)
  Dunit = g/cm3
  Dvalue = 0.0010967
  Group = -> [C_element003,H_element003]
  conduct = 2
  density = 1
  expand = 3
  formula = G4_ACETYLENE
  name = G4_ACETYLENE
  specific = 4
FEATURE [App::DocumentObjectGroupPython] C_element004  label="C_element : 5"  # scripted group (container) (typed FeaturePython)
  n = 5
  ref = C_element
FEATURE [App::DocumentObjectGroupPython] H_element004  label="H_element : 5"  # scripted group (container) (typed FeaturePython)
  n = 5
  ref = H_element
FEATURE [App::DocumentObjectGroupPython] N_element002  label="N_element : 5"  # scripted group (container) (typed FeaturePython)
  n = 5
  ref = N_element
FEATURE [App::DocumentObjectGroupPython] G4_ADENINE  # scripted group (container) (typed FeaturePython)
  Dunit = g/cm3
  Dvalue = 1.6
  Group = -> [C_element004,H_element004,N_element002]
  conduct = 2
  density = 1
  expand = 3
  formula = G4_ADENINE
  name = G4_ADENINE
  specific = 4
FEATURE [App::DocumentObjectGroupPython] H_element005  label="H_element : 0.114"  # scripted group (container) (typed FeaturePython)
  n = 0.114
FEATURE [App::DocumentObjectGroupPython] C_element005  label="C_element : 0.598"  # scripted group (container) (typed FeaturePython)
  n = 0.598
FEATURE [App::DocumentObjectGroupPython] N_element003  label="N_element : 0.007"  # scripted group (container) (typed FeaturePython)
  n = 0.007
FEATURE [App::DocumentObjectGroupPython] O_element003  label="O_element : 0.278"  # scripted group (container) (typed FeaturePython)
  n = 0.278
FEATURE [App::DocumentObjectGroupPython] Na_element001  label="Na_element : 0.001"  # scripted group (container) (typed FeaturePython)
  n = 0.001
FEATURE [App::DocumentObjectGroupPython] S_element001  label="S_element : 0.001"  # scripted group (container) (typed FeaturePython)
  n = 0.001
FEATURE [App::DocumentObjectGroupPython] Cl_element001  label="Cl_element : 0.001"  # scripted group (container) (typed FeaturePython)
  n = 0.001
FEATURE [App::DocumentObjectGroupPython] G4_ADIPOSE_TISSUE_ICRP  # scripted group (container) (typed FeaturePython)
  Dunit = g/cm3
  Dvalue = 0.95
  Group = -> [H_element005,C_element005,N_element003,O_element003,Na_element001,S_element001,Cl_element001]
  conduct = 2
  density = 1
  expand = 3
  formula = G4_ADIPOSE_TISSUE_ICRP
  name = G4_ADIPOSE_TISSUE_ICRP
  specific = 4
FEATURE [App::DocumentObjectGroupPython] C_element006  label="C_element : 0.000"  # scripted group (container) (typed FeaturePython)
  n = 0.000124
FEATURE [App::DocumentObjectGroupPython] N_element004  label="N_element : 0.755"  # scripted group (container) (typed FeaturePython)
  n = 0.755268
FEATURE [App::DocumentObjectGroupPython] O_element004  label="O_element : 0.232"  # scripted group (container) (typed FeaturePython)
  n = 0.231781
FEATURE [App::DocumentObjectGroupPython] Ar_element001  label="Ar_element : 0.013"  # scripted group (container) (typed FeaturePython)
  n = 0.012827
FEATURE [App::DocumentObjectGroupPython] G4_AIR001  label="G4_AIR"  # scripted group (container) (typed FeaturePython)
  Dunit = g/cm3
  Dvalue = 0.00120479
  Group = -> [C_element006,N_element004,O_element004,Ar_element001]
  conduct = 2
  density = 1
  expand = 3
  formula = G4_AIR
  name = G4_AIR
  specific = 4
FEATURE [App::DocumentObjectGroupPython] C_element007  label="C_element : 006"  # scripted group (container) (typed FeaturePython)
  n = 3
  ref = C_element
FEATURE [App::DocumentObjectGroupPython] H_element006  label="H_element : 7"  # scripted group (container) (typed FeaturePython)
  n = 7
  ref = H_element
FEATURE [App::DocumentObjectGroupPython] N_element005  label="N_element : 1"  # scripted group (container) (typed FeaturePython)
  n = 1
  ref = N_element
FEATURE [App::DocumentObjectGroupPython] O_element005  label="O_element : 2"  # scripted group (container) (typed FeaturePython)
  n = 2
  ref = O_element
FEATURE [App::DocumentObjectGroupPython] G4_ALANINE  # scripted group (container) (typed FeaturePython)
  Dunit = g/cm3
  Dvalue = 1.42
  Group = -> [C_element007,H_element006,N_element005,O_element005]
  conduct = 2
  density = 1
  expand = 3
  formula = G4_ALANINE
  name = G4_ALANINE
  specific = 4
FEATURE [App::DocumentObjectGroupPython] Al_element001  label="Al_element : 2"  # scripted group (container) (typed FeaturePython)
  n = 2
  ref = Al_element
FEATURE [App::DocumentObjectGroupPython] O_element006  label="O_element : 3"  # scripted group (container) (typed FeaturePython)
  n = 3
  ref = O_element
FEATURE [App::DocumentObjectGroupPython] G4_ALUMINUM_OXIDE  # scripted group (container) (typed FeaturePython)
  Dunit = g/cm3
  Dvalue = 3.97
  Group = -> [Al_element001,O_element006]
  conduct = 2
  density = 1
  expand = 3
  formula = G4_ALUMINUM_OXIDE
  name = G4_ALUMINUM_OXIDE
  specific = 4
FEATURE [App::DocumentObjectGroupPython] H_element007  label="H_element : 0.106"  # scripted group (container) (typed FeaturePython)
  n = 0.10593
FEATURE [App::DocumentObjectGroupPython] C_element008  label="C_element : 0.789"  # scripted group (container) (typed FeaturePython)
  n = 0.788974
FEATURE [App::DocumentObjectGroupPython] O_element007  label="O_element : 0.105"  # scripted group (container) (typed FeaturePython)
  n = 0.105096
FEATURE [App::DocumentObjectGroupPython] G4_AMBER  # scripted group (container) (typed FeaturePython)
  Dunit = g/cm3
  Dvalue = 1.1
  Group = -> [H_element007,C_element008,O_element007]
  conduct = 2
  density = 1
  expand = 3
  formula = G4_AMBER
  name = G4_AMBER
  specific = 4
FEATURE [App::DocumentObjectGroupPython] N_element006  label="N_element : 006"  # scripted group (container) (typed FeaturePython)
  n = 1
  ref = N_element
FEATURE [App::DocumentObjectGroupPython] H_element008  label="H_element : 3"  # scripted group (container) (typed FeaturePython)
  n = 3
  ref = H_element
FEATURE [App::DocumentObjectGroupPython] G4_AMMONIA  # scripted group (container) (typed FeaturePython)
  Dunit = g/cm3
  Dvalue = 0.000826019
  Group = -> [N_element006,H_element008]
  conduct = 2
  density = 1
  expand = 3
  formula = G4_AMMONIA
  name = G4_AMMONIA
  specific = 4
FEATURE [App::DocumentObjectGroupPython] C_element009  label="C_element : 6"  # scripted group (container) (typed FeaturePython)
  n = 6
  ref = C_element
FEATURE [App::DocumentObjectGroupPython] H_element009  label="H_element : 008"  # scripted group (container) (typed FeaturePython)
  n = 7
  ref = H_element
FEATURE [App::DocumentObjectGroupPython] N_element007  label="N_element : 007"  # scripted group (container) (typed FeaturePython)
  n = 1
  ref = N_element
FEATURE [App::DocumentObjectGroupPython] G4_ANILINE  # scripted group (container) (typed FeaturePython)
  Dunit = g/cm3
  Dvalue = 1.0235
  Group = -> [C_element009,H_element009,N_element007]
  conduct = 2
  density = 1
  expand = 3
  formula = G4_ANILINE
  name = G4_ANILINE
  specific = 4
FEATURE [App::DocumentObjectGroupPython] C_element010  label="C_element : 14"  # scripted group (container) (typed FeaturePython)
  n = 14
  ref = C_element
FEATURE [App::DocumentObjectGroupPython] H_element010  label="H_element : 10"  # scripted group (container) (typed FeaturePython)
  n = 10
  ref = H_element
FEATURE [App::DocumentObjectGroupPython] G4_ANTHRACENE  # scripted group (container) (typed FeaturePython)
  Dunit = g/cm3
  Dvalue = 1.283
  Group = -> [C_element010,H_element010]
  conduct = 2
  density = 1
  expand = 3
  formula = G4_ANTHRACENE
  name = G4_ANTHRACENE
  specific = 4
FEATURE [App::DocumentObjectGroupPython] H_element011  label="H_element : 0.065"  # scripted group (container) (typed FeaturePython)
  n = 0.0654709
FEATURE [App::DocumentObjectGroupPython] C_element011  label="C_element : 0.537"  # scripted group (container) (typed FeaturePython)
  n = 0.536944
FEATURE [App::DocumentObjectGroupPython] N_element008  label="N_element : 0.021"  # scripted group (container) (typed FeaturePython)
  n = 0.0215
FEATURE [App::DocumentObjectGroupPython] O_element008  label="O_element : 0.032"  # scripted group (container) (typed FeaturePython)
  n = 0.032085
FEATURE [App::DocumentObjectGroupPython] F_element002  label="F_element : 0.167"  # scripted group (container) (typed FeaturePython)
  n = 0.167411
FEATURE [App::DocumentObjectGroupPython] Ca_element002  label="Ca_element : 0.177"  # scripted group (container) (typed FeaturePython)
  n = 0.176589
FEATURE [App::DocumentObjectGroupPython] G4_B_100_BONE  label="G4_B-100_BONE"  # scripted group (container) (typed FeaturePython)
  Dunit = g/cm3
  Dvalue = 1.45
  Group = -> [H_element011,C_element011,N_element008,O_element008,F_element002,Ca_element002]
  conduct = 2
  density = 1
  expand = 3
  formula = G4_B-100_BONE
  name = G4_B-100_BONE
  specific = 4
FEATURE [App::DocumentObjectGroupPython] H_element012  label="H_element : 0.057"  # scripted group (container) (typed FeaturePython)
  n = 0.057441
FEATURE [App::DocumentObjectGroupPython] C_element012  label="C_element : 0.790"  # scripted group (container) (typed FeaturePython)
  n = 0.774591
FEATURE [App::DocumentObjectGroupPython] O_element009  label="O_element : 0.168"  # scripted group (container) (typed FeaturePython)
  n = 0.167968
FEATURE [App::DocumentObjectGroupPython] G4_BAKELITE  # scripted group (container) (typed FeaturePython)
  Dunit = g/cm3
  Dvalue = 1.25
  Group = -> [H_element012,C_element012,O_element009]
  conduct = 2
  density = 1
  expand = 3
  formula = G4_BAKELITE
  name = G4_BAKELITE
  specific = 4
FEATURE [App::DocumentObjectGroupPython] Ba_element001  label="Ba_element : 1"  # scripted group (container) (typed FeaturePython)
  n = 1
  ref = Ba_element
FEATURE [App::DocumentObjectGroupPython] F_element003  label="F_element : 2"  # scripted group (container) (typed FeaturePython)
  n = 2
  ref = F_element
FEATURE [App::DocumentObjectGroupPython] G4_BARIUM_FLUORIDE  # scripted group (container) (typed FeaturePython)
  Dunit = g/cm3
  Dvalue = 4.89
  Group = -> [Ba_element001,F_element003]
  conduct = 2
  density = 1
  expand = 3
  formula = G4_BARIUM_FLUORIDE
  name = G4_BARIUM_FLUORIDE
  specific = 4
FEATURE [App::DocumentObjectGroupPython] Ba_element002  label="Ba_element : 002"  # scripted group (container) (typed FeaturePython)
  n = 1
  ref = Ba_element
FEATURE [App::DocumentObjectGroupPython] S_element002  label="S_element : 1"  # scripted group (container) (typed FeaturePython)
  n = 1
  ref = S_element
FEATURE [App::DocumentObjectGroupPython] O_element010  label="O_element : 4"  # scripted group (container) (typed FeaturePython)
  n = 4
  ref = O_element
FEATURE [App::DocumentObjectGroupPython] G4_BARIUM_SULFATE  # scripted group (container) (typed FeaturePython)
  Dunit = g/cm3
  Dvalue = 4.5
  Group = -> [Ba_element002,S_element002,O_element010]
  conduct = 2
  density = 1
  expand = 3
  formula = G4_BARIUM_SULFATE
  name = G4_BARIUM_SULFATE
  specific = 4
FEATURE [App::DocumentObjectGroupPython] C_element013  label="C_element : 007"  # scripted group (container) (typed FeaturePython)
  n = 6
  ref = C_element
FEATURE [App::DocumentObjectGroupPython] H_element013  label="H_element : 009"  # scripted group (container) (typed FeaturePython)
  n = 6
  ref = H_element
FEATURE [App::DocumentObjectGroupPython] G4_BENZENE  # scripted group (container) (typed FeaturePython)
  Dunit = g/cm3
  Dvalue = 0.87865
  Group = -> [C_element013,H_element013]
  conduct = 2
  density = 1
  expand = 3
  formula = G4_BENZENE
  name = G4_BENZENE
  specific = 4
FEATURE [App::DocumentObjectGroupPython] Be_element001  label="Be_element : 1"  # scripted group (container) (typed FeaturePython)
  n = 1
  ref = Be_element
FEATURE [App::DocumentObjectGroupPython] O_element011  label="O_element : 005"  # scripted group (container) (typed FeaturePython)
  n = 1
  ref = O_element
FEATURE [App::DocumentObjectGroupPython] G4_BERYLLIUM_OXIDE  # scripted group (container) (typed FeaturePython)
  Dunit = g/cm3
  Dvalue = 3.01
  Group = -> [Be_element001,O_element011]
  conduct = 2
  density = 1
  expand = 3
  formula = G4_BERYLLIUM_OXIDE
  name = G4_BERYLLIUM_OXIDE
  specific = 4
FEATURE [App::DocumentObjectGroupPython] Bi_element001  label="Bi_element : 4"  # scripted group (container) (typed FeaturePython)
  n = 4
  ref = Bi_element
FEATURE [App::DocumentObjectGroupPython] Ge_element001  label="Ge_element : 3"  # scripted group (container) (typed FeaturePython)
  n = 3
  ref = Ge_element
FEATURE [App::DocumentObjectGroupPython] O_element012  label="O_element : 12"  # scripted group (container) (typed FeaturePython)
  n = 12
  ref = O_element
FEATURE [App::DocumentObjectGroupPython] G4_BGO  # scripted group (container) (typed FeaturePython)
  Dunit = g/cm3
  Dvalue = 7.13
  Group = -> [Bi_element001,Ge_element001,O_element012]
  conduct = 2
  density = 1
  expand = 3
  formula = G4_BGO
  name = G4_BGO
  specific = 4
FEATURE [App::DocumentObjectGroupPython] H_element014  label="H_element : 0.102"  # scripted group (container) (typed FeaturePython)
  n = 0.102
FEATURE [App::DocumentObjectGroupPython] C_element014  label="C_element : 0.110"  # scripted group (container) (typed FeaturePython)
  n = 0.11
FEATURE [App::DocumentObjectGroupPython] N_element009  label="N_element : 0.033"  # scripted group (container) (typed FeaturePython)
  n = 0.033
FEATURE [App::DocumentObjectGroupPython] O_element013  label="O_element : 0.745"  # scripted group (container) (typed FeaturePython)
  n = 0.745
FEATURE [App::DocumentObjectGroupPython] Na_element002  label="Na_element : 0.002"  # scripted group (container) (typed FeaturePython)
  n = 0.001
FEATURE [App::DocumentObjectGroupPython] P_element001  label="P_element : 0.001"  # scripted group (container) (typed FeaturePython)
  n = 0.001
FEATURE [App::DocumentObjectGroupPython] S_element003  label="S_element : 0.002"  # scripted group (container) (typed FeaturePython)
  n = 0.002
FEATURE [App::DocumentObjectGroupPython] Cl_element002  label="Cl_element : 0.003"  # scripted group (container) (typed FeaturePython)
  n = 0.003
FEATURE [App::DocumentObjectGroupPython] K_element001  label="K_element : 0.002"  # scripted group (container) (typed FeaturePython)
  n = 0.002
FEATURE [App::DocumentObjectGroupPython] Fe_element001  label="Fe_element : 0.001"  # scripted group (container) (typed FeaturePython)
  n = 0.001
FEATURE [App::DocumentObjectGroupPython] G4_BLOOD_ICRP  # scripted group (container) (typed FeaturePython)
  Dunit = g/cm3
  Dvalue = 1.06
  Group = -> [H_element014,C_element014,N_element009,O_element013,Na_element002,P_element001,S_element003,Cl_element002,K_element001,Fe_element001]
  conduct = 2
  density = 1
  expand = 3
  formula = G4_BLOOD_ICRP
  name = G4_BLOOD_ICRP
  specific = 4
FEATURE [App::DocumentObjectGroupPython] H_element015  label="H_element : 0.064"  # scripted group (container) (typed FeaturePython)
  n = 0.064
FEATURE [App::DocumentObjectGroupPython] C_element015  label="C_element : 0.278"  # scripted group (container) (typed FeaturePython)
  n = 0.278
FEATURE [App::DocumentObjectGroupPython] N_element010  label="N_element : 0.027"  # scripted group (container) (typed FeaturePython)
  n = 0.027
FEATURE [App::DocumentObjectGroupPython] O_element014  label="O_element : 0.410"  # scripted group (container) (typed FeaturePython)
  n = 0.41
FEATURE [App::DocumentObjectGroupPython] Mg_element001  label="Mg_element : 0.002"  # scripted group (container) (typed FeaturePython)
  n = 0.002
FEATURE [App::DocumentObjectGroupPython] P_element002  label="P_element : 0.070"  # scripted group (container) (typed FeaturePython)
  n = 0.07
FEATURE [App::DocumentObjectGroupPython] S_element004  label="S_element : 0.003"  # scripted group (container) (typed FeaturePython)
  n = 0.002
FEATURE [App::DocumentObjectGroupPython] Ca_element003  label="Ca_element : 0.147"  # scripted group (container) (typed FeaturePython)
  n = 0.147
FEATURE [App::DocumentObjectGroupPython] G4_BONE_COMPACT_ICRU  # scripted group (container) (typed FeaturePython)
  Dunit = g/cm3
  Dvalue = 1.85
  Group = -> [H_element015,C_element015,N_element010,O_element014,Mg_element001,P_element002,S_element004,Ca_element003]
  conduct = 2
  density = 1
  expand = 3
  formula = G4_BONE_COMPACT_ICRU
  name = G4_BONE_COMPACT_ICRU
  specific = 4
FEATURE [App::DocumentObjectGroupPython] H_element016  label="H_element : 0.034"  # scripted group (container) (typed FeaturePython)
  n = 0.034
FEATURE [App::DocumentObjectGroupPython] C_element016  label="C_element : 0.155"  # scripted group (container) (typed FeaturePython)
  n = 0.155
FEATURE [App::DocumentObjectGroupPython] N_element011  label="N_element : 0.042"  # scripted group (container) (typed FeaturePython)
  n = 0.042
FEATURE [App::DocumentObjectGroupPython] O_element015  label="O_element : 0.435"  # scripted group (container) (typed FeaturePython)
  n = 0.435
FEATURE [App::DocumentObjectGroupPython] Na_element003  label="Na_element : 0.003"  # scripted group (container) (typed FeaturePython)
  n = 0.001
FEATURE [App::DocumentObjectGroupPython] Mg_element002  label="Mg_element : 0.003"  # scripted group (container) (typed FeaturePython)
  n = 0.002
FEATURE [App::DocumentObjectGroupPython] P_element003  label="P_element : 0.103"  # scripted group (container) (typed FeaturePython)
  n = 0.103
FEATURE [App::DocumentObjectGroupPython] S_element005  label="S_element : 0.004"  # scripted group (container) (typed FeaturePython)
  n = 0.003
FEATURE [App::DocumentObjectGroupPython] Ca_element004  label="Ca_element : 0.225"  # scripted group (container) (typed FeaturePython)
  n = 0.225
FEATURE [App::DocumentObjectGroupPython] G4_BONE_CORTICAL_ICRP  # scripted group (container) (typed FeaturePython)
  Dunit = g/cm3
  Dvalue = 1.92
  Group = -> [H_element016,C_element016,N_element011,O_element015,Na_element003,Mg_element002,P_element003,S_element005,Ca_element004]
  conduct = 2
  density = 1
  expand = 3
  formula = G4_BONE_CORTICAL_ICRP
  name = G4_BONE_CORTICAL_ICRP
  specific = 4
FEATURE [App::DocumentObjectGroupPython] B_element001  label="B_element : 4"  # scripted group (container) (typed FeaturePython)
  n = 4
  ref = B_element
FEATURE [App::DocumentObjectGroupPython] C_element017  label="C_element : 1"  # scripted group (container) (typed FeaturePython)
  n = 1
  ref = C_element
FEATURE [App::DocumentObjectGroupPython] G4_BORON_CARBIDE  # scripted group (container) (typed FeaturePython)
  Dunit = g/cm3
  Dvalue = 2.52
  Group = -> [B_element001,C_element017]
  conduct = 2
  density = 1
  expand = 3
  formula = G4_BORON_CARBIDE
  name = G4_BORON_CARBIDE
  specific = 4
FEATURE [App::DocumentObjectGroupPython] B_element002  label="B_element : 2"  # scripted group (container) (typed FeaturePython)
  n = 2
  ref = B_element
FEATURE [App::DocumentObjectGroupPython] O_element016  label="O_element : 006"  # scripted group (container) (typed FeaturePython)
  n = 3
  ref = O_element
FEATURE [App::DocumentObjectGroupPython] G4_BORON_OXIDE  # scripted group (container) (typed FeaturePython)
  Dunit = g/cm3
  Dvalue = 1.812
  Group = -> [B_element002,O_element016]
  conduct = 2
  density = 1
  expand = 3
  formula = G4_BORON_OXIDE
  name = G4_BORON_OXIDE
  specific = 4
FEATURE [App::DocumentObjectGroupPython] H_element017  label="H_element : 0.107"  # scripted group (container) (typed FeaturePython)
  n = 0.107
FEATURE [App::DocumentObjectGroupPython] C_element018  label="C_element : 0.145"  # scripted group (container) (typed FeaturePython)
  n = 0.145
FEATURE [App::DocumentObjectGroupPython] N_element012  label="N_element : 0.022"  # scripted group (container) (typed FeaturePython)
  n = 0.022
FEATURE [App::DocumentObjectGroupPython] O_element017  label="O_element : 0.712"  # scripted group (container) (typed FeaturePython)
  n = 0.712
FEATURE [App::DocumentObjectGroupPython] Na_element004  label="Na_element : 0.004"  # scripted group (container) (typed FeaturePython)
  n = 0.002
FEATURE [App::DocumentObjectGroupPython] P_element004  label="P_element : 0.004"  # scripted group (container) (typed FeaturePython)
  n = 0.004
FEATURE [App::DocumentObjectGroupPython] S_element006  label="S_element : 0.005"  # scripted group (container) (typed FeaturePython)
  n = 0.002
FEATURE [App::DocumentObjectGroupPython] Cl_element003  label="Cl_element : 0.004"  # scripted group (container) (typed FeaturePython)
  n = 0.003
FEATURE [App::DocumentObjectGroupPython] K_element002  label="K_element : 0.003"  # scripted group (container) (typed FeaturePython)
  n = 0.003
FEATURE [App::DocumentObjectGroupPython] G4_BRAIN_ICRP  # scripted group (container) (typed FeaturePython)
  Dunit = g/cm3
  Dvalue = 1.04
  Group = -> [H_element017,C_element018,N_element012,O_element017,Na_element004,P_element004,S_element006,Cl_element003,K_element002]
  conduct = 2
  density = 1
  expand = 3
  formula = G4_BRAIN_ICRP
  name = G4_BRAIN_ICRP
  specific = 4
FEATURE [App::DocumentObjectGroupPython] C_element019  label="C_element : 4"  # scripted group (container) (typed FeaturePython)
  n = 4
  ref = C_element
FEATURE [App::DocumentObjectGroupPython] H_element018  label="H_element : 010"  # scripted group (container) (typed FeaturePython)
  n = 10
  ref = H_element
FEATURE [App::DocumentObjectGroupPython] G4_BUTANE  # scripted group (container) (typed FeaturePython)
  Dunit = g/cm3
  Dvalue = 0.00249343
  Group = -> [C_element019,H_element018]
  conduct = 2
  density = 1
  expand = 3
  formula = G4_BUTANE
  name = G4_BUTANE
  specific = 4
FEATURE [App::DocumentObjectGroupPython] C_element020  label="C_element : 008"  # scripted group (container) (typed FeaturePython)
  n = 4
  ref = C_element
FEATURE [App::DocumentObjectGroupPython] H_element019  label="H_element : 011"  # scripted group (container) (typed FeaturePython)
  n = 10
  ref = H_element
FEATURE [App::DocumentObjectGroupPython] O_element018  label="O_element : 007"  # scripted group (container) (typed FeaturePython)
  n = 1
  ref = O_element
FEATURE [App::DocumentObjectGroupPython] G4_N_BUTYL_ALCOHOL  label="G4_N-BUTYL_ALCOHOL"  # scripted group (container) (typed FeaturePython)
  Dunit = g/cm3
  Dvalue = 0.8098
  Group = -> [C_element020,H_element019,O_element018]
  conduct = 2
  density = 1
  expand = 3
  formula = G4_N-BUTYL_ALCOHOL
  name = G4_N-BUTYL_ALCOHOL
  specific = 4
FEATURE [App::DocumentObjectGroupPython] H_element020  label="H_element : 0.025"  # scripted group (container) (typed FeaturePython)
  n = 0.02468
FEATURE [App::DocumentObjectGroupPython] C_element021  label="C_element : 0.502"  # scripted group (container) (typed FeaturePython)
  n = 0.501611
FEATURE [App::DocumentObjectGroupPython] O_element019  label="O_element : 0.005"  # scripted group (container) (typed FeaturePython)
  n = 0.004527
FEATURE [App::DocumentObjectGroupPython] F_element004  label="F_element : 0.465"  # scripted group (container) (typed FeaturePython)
  n = 0.465209
FEATURE [App::DocumentObjectGroupPython] Si_element001  label="Si_element : 0.004"  # scripted group (container) (typed FeaturePython)
  n = 0.003973
FEATURE [App::DocumentObjectGroupPython] G4_C_552  label="G4_C-552"  # scripted group (container) (typed FeaturePython)
  Dunit = g/cm3
  Dvalue = 1.76
  Group = -> [H_element020,C_element021,O_element019,F_element004,Si_element001]
  conduct = 2
  density = 1
  expand = 3
  formula = G4_C-552
  name = G4_C-552
  specific = 4
FEATURE [App::DocumentObjectGroupPython] Cd_element001  label="Cd_element : 1"  # scripted group (container) (typed FeaturePython)
  n = 1
  ref = Cd_element
FEATURE [App::DocumentObjectGroupPython] Te_element001  label="Te_element : 1"  # scripted group (container) (typed FeaturePython)
  n = 1
  ref = Te_element
FEATURE [App::DocumentObjectGroupPython] G4_CADMIUM_TELLURIDE  # scripted group (container) (typed FeaturePython)
  Dunit = g/cm3
  Dvalue = 6.2
  Group = -> [Cd_element001,Te_element001]
  conduct = 2
  density = 1
  expand = 3
  formula = G4_CADMIUM_TELLURIDE
  name = G4_CADMIUM_TELLURIDE
  specific = 4
FEATURE [App::DocumentObjectGroupPython] Cd_element002  label="Cd_element : 002"  # scripted group (container) (typed FeaturePython)
  n = 1
  ref = Cd_element
FEATURE [App::DocumentObjectGroupPython] W_element001  label="W_element : 1"  # scripted group (container) (typed FeaturePython)
  n = 1
  ref = W_element
FEATURE [App::DocumentObjectGroupPython] O_element020  label="O_element : 008"  # scripted group (container) (typed FeaturePython)
  n = 4
  ref = O_element
FEATURE [App::DocumentObjectGroupPython] G4_CADMIUM_TUNGSTATE  # scripted group (container) (typed FeaturePython)
  Dunit = g/cm3
  Dvalue = 7.9
  Group = -> [Cd_element002,W_element001,O_element020]
  conduct = 2
  density = 1
  expand = 3
  formula = G4_CADMIUM_TUNGSTATE
  name = G4_CADMIUM_TUNGSTATE
  specific = 4
FEATURE [App::DocumentObjectGroupPython] Ca_element005  label="Ca_element : 1"  # scripted group (container) (typed FeaturePython)
  n = 1
  ref = Ca_element
FEATURE [App::DocumentObjectGroupPython] C_element022  label="C_element : 009"  # scripted group (container) (typed FeaturePython)
  n = 1
  ref = C_element
FEATURE [App::DocumentObjectGroupPython] O_element021  label="O_element : 009"  # scripted group (container) (typed FeaturePython)
  n = 3
  ref = O_element
FEATURE [App::DocumentObjectGroupPython] G4_CALCIUM_CARBONATE  # scripted group (container) (typed FeaturePython)
  Dunit = g/cm3
  Dvalue = 2.8
  Group = -> [Ca_element005,C_element022,O_element021]
  conduct = 2
  density = 1
  expand = 3
  formula = G4_CALCIUM_CARBONATE
  name = G4_CALCIUM_CARBONATE
  specific = 4
FEATURE [App::DocumentObjectGroupPython] Ca_element006  label="Ca_element : 002"  # scripted group (container) (typed FeaturePython)
  n = 1
  ref = Ca_element
FEATURE [App::DocumentObjectGroupPython] F_element005  label="F_element : 003"  # scripted group (container) (typed FeaturePython)
  n = 2
  ref = F_element
FEATURE [App::DocumentObjectGroupPython] G4_CALCIUM_FLUORIDE  # scripted group (container) (typed FeaturePython)
  Dunit = g/cm3
  Dvalue = 3.18
  Group = -> [Ca_element006,F_element005]
  conduct = 2
  density = 1
  expand = 3
  formula = G4_CALCIUM_FLUORIDE
  name = G4_CALCIUM_FLUORIDE
  specific = 4
FEATURE [App::DocumentObjectGroupPython] Ca_element007  label="Ca_element : 003"  # scripted group (container) (typed FeaturePython)
  n = 1
  ref = Ca_element
FEATURE [App::DocumentObjectGroupPython] O_element022  label="O_element : 010"  # scripted group (container) (typed FeaturePython)
  n = 1
  ref = O_element
FEATURE [App::DocumentObjectGroupPython] G4_CALCIUM_OXIDE  # scripted group (container) (typed FeaturePython)
  Dunit = g/cm3
  Dvalue = 3.3
  Group = -> [Ca_element007,O_element022]
  conduct = 2
  density = 1
  expand = 3
  formula = G4_CALCIUM_OXIDE
  name = G4_CALCIUM_OXIDE
  specific = 4
FEATURE [App::DocumentObjectGroupPython] Ca_element008  label="Ca_element : 004"  # scripted group (container) (typed FeaturePython)
  n = 1
  ref = Ca_element
FEATURE [App::DocumentObjectGroupPython] S_element007  label="S_element : 002"  # scripted group (container) (typed FeaturePython)
  n = 1
  ref = S_element
FEATURE [App::DocumentObjectGroupPython] O_element023  label="O_element : 011"  # scripted group (container) (typed FeaturePython)
  n = 4
  ref = O_element
FEATURE [App::DocumentObjectGroupPython] G4_CALCIUM_SULFATE  # scripted group (container) (typed FeaturePython)
  Dunit = g/cm3
  Dvalue = 2.96
  Group = -> [Ca_element008,S_element007,O_element023]
  conduct = 2
  density = 1
  expand = 3
  formula = G4_CALCIUM_SULFATE
  name = G4_CALCIUM_SULFATE
  specific = 4
FEATURE [App::DocumentObjectGroupPython] Ca_element009  label="Ca_element : 005"  # scripted group (container) (typed FeaturePython)
  n = 1
  ref = Ca_element
FEATURE [App::DocumentObjectGroupPython] W_element002  label="W_element : 002"  # scripted group (container) (typed FeaturePython)
  n = 1
  ref = W_element
FEATURE [App::DocumentObjectGroupPython] O_element024  label="O_element : 012"  # scripted group (container) (typed FeaturePython)
  n = 4
  ref = O_element
FEATURE [App::DocumentObjectGroupPython] G4_CALCIUM_TUNGSTATE  # scripted group (container) (typed FeaturePython)
  Dunit = g/cm3
  Dvalue = 6.062
  Group = -> [Ca_element009,W_element002,O_element024]
  conduct = 2
  density = 1
  expand = 3
  formula = G4_CALCIUM_TUNGSTATE
  name = G4_CALCIUM_TUNGSTATE
  specific = 4
FEATURE [App::DocumentObjectGroupPython] C_element023  label="C_element : 010"  # scripted group (container) (typed FeaturePython)
  n = 1
  ref = C_element
FEATURE [App::DocumentObjectGroupPython] O_element025  label="O_element : 013"  # scripted group (container) (typed FeaturePython)
  n = 2
  ref = O_element
FEATURE [App::DocumentObjectGroupPython] G4_CARBON_DIOXIDE  # scripted group (container) (typed FeaturePython)
  Dunit = g/cm3
  Dvalue = 0.00184212
  Group = -> [C_element023,O_element025]
  conduct = 2
  density = 1
  expand = 3
  formula = G4_CARBON_DIOXIDE
  name = G4_CARBON_DIOXIDE
  specific = 4
FEATURE [App::DocumentObjectGroupPython] C_element024  label="C_element : 011"  # scripted group (container) (typed FeaturePython)
  n = 1
  ref = C_element
FEATURE [App::DocumentObjectGroupPython] Cl_element004  label="Cl_element : 4"  # scripted group (container) (typed FeaturePython)
  n = 4
  ref = Cl_element
FEATURE [App::DocumentObjectGroupPython] G4_CARBON_TETRACHLORIDE  # scripted group (container) (typed FeaturePython)
  Dunit = g/cm3
  Dvalue = 1.594
  Group = -> [C_element024,Cl_element004]
  conduct = 2
  density = 1
  expand = 3
  formula = G4_CARBON_TETRACHLORIDE
  name = G4_CARBON_TETRACHLORIDE
  specific = 4
FEATURE [App::DocumentObjectGroupPython] C_element025  label="C_element : 012"  # scripted group (container) (typed FeaturePython)
  n = 6
  ref = C_element
FEATURE [App::DocumentObjectGroupPython] H_element021  label="H_element : 012"  # scripted group (container) (typed FeaturePython)
  n = 10
  ref = H_element
FEATURE [App::DocumentObjectGroupPython] O_element026  label="O_element : 5"  # scripted group (container) (typed FeaturePython)
  n = 5
  ref = O_element
FEATURE [App::DocumentObjectGroupPython] G4_CELLULOSE_CELLOPHANE  # scripted group (container) (typed FeaturePython)
  Dunit = g/cm3
  Dvalue = 1.42
  Group = -> [C_element025,H_element021,O_element026]
  conduct = 2
  density = 1
  expand = 3
  formula = G4_CELLULOSE_CELLOPHANE
  name = G4_CELLULOSE_CELLOPHANE
  specific = 4
FEATURE [App::DocumentObjectGroupPython] H_element022  label="H_element : 0.067"  # scripted group (container) (typed FeaturePython)
  n = 0.067125
FEATURE [App::DocumentObjectGroupPython] C_element026  label="C_element : 0.545"  # scripted group (container) (typed FeaturePython)
  n = 0.545403
FEATURE [App::DocumentObjectGroupPython] O_element027  label="O_element : 0.387"  # scripted group (container) (typed FeaturePython)
  n = 0.387472
FEATURE [App::DocumentObjectGroupPython] G4_CELLULOSE_BUTYRATE  # scripted group (container) (typed FeaturePython)
  Dunit = g/cm3
  Dvalue = 1.2
  Group = -> [H_element022,C_element026,O_element027]
  conduct = 2
  density = 1
  expand = 3
  formula = G4_CELLULOSE_BUTYRATE
  name = G4_CELLULOSE_BUTYRATE
  specific = 4
FEATURE [App::DocumentObjectGroupPython] H_element023  label="H_element : 0.029"  # scripted group (container) (typed FeaturePython)
  n = 0.029216
FEATURE [App::DocumentObjectGroupPython] C_element027  label="C_element : 0.271"  # scripted group (container) (typed FeaturePython)
  n = 0.271296
FEATURE [App::DocumentObjectGroupPython] N_element013  label="N_element : 0.121"  # scripted group (container) (typed FeaturePython)
  n = 0.121276
FEATURE [App::DocumentObjectGroupPython] O_element028  label="O_element : 0.578"  # scripted group (container) (typed FeaturePython)
  n = 0.578212
FEATURE [App::DocumentObjectGroupPython] G4_CELLULOSE_NITRATE  # scripted group (container) (typed FeaturePython)
  Dunit = g/cm3
  Dvalue = 1.49
  Group = -> [H_element023,C_element027,N_element013,O_element028]
  conduct = 2
  density = 1
  expand = 3
  formula = G4_CELLULOSE_NITRATE
  name = G4_CELLULOSE_NITRATE
  specific = 4
FEATURE [App::DocumentObjectGroupPython] H_element024  label="H_element : 0.108"  # scripted group (container) (typed FeaturePython)
  n = 0.107596
FEATURE [App::DocumentObjectGroupPython] N_element014  label="N_element : 0.001"  # scripted group (container) (typed FeaturePython)
  n = 0.0008
FEATURE [App::DocumentObjectGroupPython] O_element029  label="O_element : 0.875"  # scripted group (container) (typed FeaturePython)
  n = 0.874976
FEATURE [App::DocumentObjectGroupPython] S_element008  label="S_element : 0.015"  # scripted group (container) (typed FeaturePython)
  n = 0.014627
FEATURE [App::DocumentObjectGroupPython] Ce_element001  label="Ce_element : 0.002"  # scripted group (container) (typed FeaturePython)
  n = 0.002001
FEATURE [App::DocumentObjectGroupPython] G4_CERIC_SULFATE  # scripted group (container) (typed FeaturePython)
  Dunit = g/cm3
  Dvalue = 1.03
  Group = -> [H_element024,N_element014,O_element029,S_element008,Ce_element001]
  conduct = 2
  density = 1
  expand = 3
  formula = G4_CERIC_SULFATE
  name = G4_CERIC_SULFATE
  specific = 4
FEATURE [App::DocumentObjectGroupPython] Cs_element001  label="Cs_element : 1"  # scripted group (container) (typed FeaturePython)
  n = 1
  ref = Cs_element
FEATURE [App::DocumentObjectGroupPython] F_element006  label="F_element : 1"  # scripted group (container) (typed FeaturePython)
  n = 1
  ref = F_element
FEATURE [App::DocumentObjectGroupPython] G4_CESIUM_FLUORIDE  # scripted group (container) (typed FeaturePython)
  Dunit = g/cm3
  Dvalue = 4.115
  Group = -> [Cs_element001,F_element006]
  conduct = 2
  density = 1
  expand = 3
  formula = G4_CESIUM_FLUORIDE
  name = G4_CESIUM_FLUORIDE
  specific = 4
FEATURE [App::DocumentObjectGroupPython] Cs_element002  label="Cs_element : 002"  # scripted group (container) (typed FeaturePython)
  n = 1
  ref = Cs_element
FEATURE [App::DocumentObjectGroupPython] I_element001  label="I_element : 1"  # scripted group (container) (typed FeaturePython)
  n = 1
  ref = I_element
FEATURE [App::DocumentObjectGroupPython] G4_CESIUM_IODIDE001  label="G4_CESIUM_IODIDE"  # scripted group (container) (typed FeaturePython)
  Dunit = g/cm3
  Dvalue = 4.51
  Group = -> [Cs_element002,I_element001]
  conduct = 2
  density = 1
  expand = 3
  formula = G4_CESIUM_IODIDE
  name = G4_CESIUM_IODIDE
  specific = 4
FEATURE [App::DocumentObjectGroupPython] C_element028  label="C_element : 013"  # scripted group (container) (typed FeaturePython)
  n = 6
  ref = C_element
FEATURE [App::DocumentObjectGroupPython] H_element025  label="H_element : 013"  # scripted group (container) (typed FeaturePython)
  n = 5
  ref = H_element
FEATURE [App::DocumentObjectGroupPython] Cl_element005  label="Cl_element : 1"  # scripted group (container) (typed FeaturePython)
  n = 1
  ref = Cl_element
FEATURE [App::DocumentObjectGroupPython] G4_CHLOROBENZENE  # scripted group (container) (typed FeaturePython)
  Dunit = g/cm3
  Dvalue = 1.1058
  Group = -> [C_element028,H_element025,Cl_element005]
  conduct = 2
  density = 1
  expand = 3
  formula = G4_CHLOROBENZENE
  name = G4_CHLOROBENZENE
  specific = 4
FEATURE [App::DocumentObjectGroupPython] C_element029  label="C_element : 014"  # scripted group (container) (typed FeaturePython)
  n = 1
  ref = C_element
FEATURE [App::DocumentObjectGroupPython] H_element026  label="H_element : 1"  # scripted group (container) (typed FeaturePython)
  n = 1
  ref = H_element
FEATURE [App::DocumentObjectGroupPython] Cl_element006  label="Cl_element : 3"  # scripted group (container) (typed FeaturePython)
  n = 3
  ref = Cl_element
FEATURE [App::DocumentObjectGroupPython] G4_CHLOROFORM  # scripted group (container) (typed FeaturePython)
  Dunit = g/cm3
  Dvalue = 1.4832
  Group = -> [C_element029,H_element026,Cl_element006]
  conduct = 2
  density = 1
  expand = 3
  formula = G4_CHLOROFORM
  name = G4_CHLOROFORM
  specific = 4
FEATURE [App::DocumentObjectGroupPython] H_element027  label="H_element : 0.010"  # scripted group (container) (typed FeaturePython)
  n = 0.01
FEATURE [App::DocumentObjectGroupPython] C_element030  label="C_element : 0.001"  # scripted group (container) (typed FeaturePython)
  n = 0.001
FEATURE [App::DocumentObjectGroupPython] O_element030  label="O_element : 0.529"  # scripted group (container) (typed FeaturePython)
  n = 0.529107
FEATURE [App::DocumentObjectGroupPython] Na_element005  label="Na_element : 0.016"  # scripted group (container) (typed FeaturePython)
  n = 0.016
FEATURE [App::DocumentObjectGroupPython] Mg_element003  label="Mg_element : 0.004"  # scripted group (container) (typed FeaturePython)
  n = 0.002
FEATURE [App::DocumentObjectGroupPython] Al_element002  label="Al_element : 0.034"  # scripted group (container) (typed FeaturePython)
  n = 0.033872
FEATURE [App::DocumentObjectGroupPython] Si_element002  label="Si_element : 0.337"  # scripted group (container) (typed FeaturePython)
  n = 0.337021
FEATURE [App::DocumentObjectGroupPython] K_element003  label="K_element : 0.013"  # scripted group (container) (typed FeaturePython)
  n = 0.013
FEATURE [App::DocumentObjectGroupPython] Ca_element010  label="Ca_element : 0.044"  # scripted group (container) (typed FeaturePython)
  n = 0.044
FEATURE [App::DocumentObjectGroupPython] Fe_element002  label="Fe_element : 0.014"  # scripted group (container) (typed FeaturePython)
  n = 0.014
FEATURE [App::DocumentObjectGroupPython] G4_CONCRETE  # scripted group (container) (typed FeaturePython)
  Dunit = g/cm3
  Dvalue = 2.3
  Group = -> [H_element027,C_element030,O_element030,Na_element005,Mg_element003,Al_element002,Si_element002,K_element003,Ca_element010,Fe_element002]
  conduct = 2
  density = 1
  expand = 3
  formula = G4_CONCRETE
  name = G4_CONCRETE
  specific = 4
FEATURE [App::DocumentObjectGroupPython] C_element031  label="C_element : 015"  # scripted group (container) (typed FeaturePython)
  n = 6
  ref = C_element
FEATURE [App::DocumentObjectGroupPython] H_element028  label="H_element : 12"  # scripted group (container) (typed FeaturePython)
  n = 12
  ref = H_element
FEATURE [App::DocumentObjectGroupPython] G4_CYCLOHEXANE  # scripted group (container) (typed FeaturePython)
  Dunit = g/cm3
  Dvalue = 0.779
  Group = -> [C_element031,H_element028]
  conduct = 2
  density = 1
  expand = 3
  formula = G4_CYCLOHEXANE
  name = G4_CYCLOHEXANE
  specific = 4
FEATURE [App::DocumentObjectGroupPython] C_element032  label="C_element : 016"  # scripted group (container) (typed FeaturePython)
  n = 6
  ref = C_element
FEATURE [App::DocumentObjectGroupPython] H_element029  label="H_element : 4"  # scripted group (container) (typed FeaturePython)
  n = 4
  ref = H_element
FEATURE [App::DocumentObjectGroupPython] Cl_element007  label="Cl_element : 2"  # scripted group (container) (typed FeaturePython)
  n = 2
  ref = Cl_element
FEATURE [App::DocumentObjectGroupPython] G4_1_2_DICHLOROBENZENE  label="G4_1.2-DICHLOROBENZENE"  # scripted group (container) (typed FeaturePython)
  Dunit = g/cm3
  Dvalue = 1.3048
  Group = -> [C_element032,H_element029,Cl_element007]
  conduct = 2
  density = 1
  expand = 3
  formula = G4_1.2-DICHLOROBENZENE
  name = G4_1.2-DICHLOROBENZENE
  specific = 4
FEATURE [App::DocumentObjectGroupPython] C_element033  label="C_element : 017"  # scripted group (container) (typed FeaturePython)
  n = 4
  ref = C_element
FEATURE [App::DocumentObjectGroupPython] H_element030  label="H_element : 8"  # scripted group (container) (typed FeaturePython)
  n = 8
  ref = H_element
FEATURE [App::DocumentObjectGroupPython] O_element031  label="O_element : 014"  # scripted group (container) (typed FeaturePython)
  n = 1
  ref = O_element
FEATURE [App::DocumentObjectGroupPython] Cl_element008  label="Cl_element : 005"  # scripted group (container) (typed FeaturePython)
  n = 2
  ref = Cl_element
FEATURE [App::DocumentObjectGroupPython] G4_DICHLORODIETHYL_ETHER  # scripted group (container) (typed FeaturePython)
  Dunit = g/cm3
  Dvalue = 1.2199
  Group = -> [C_element033,H_element030,O_element031,Cl_element008]
  conduct = 2
  density = 1
  expand = 3
  formula = G4_DICHLORODIETHYL_ETHER
  name = G4_DICHLORODIETHYL_ETHER
  specific = 4
FEATURE [App::DocumentObjectGroupPython] C_element034  label="C_element : 018"  # scripted group (container) (typed FeaturePython)
  n = 2
  ref = C_element
FEATURE [App::DocumentObjectGroupPython] H_element031  label="H_element : 014"  # scripted group (container) (typed FeaturePython)
  n = 4
  ref = H_element
FEATURE [App::DocumentObjectGroupPython] Cl_element009  label="Cl_element : 006"  # scripted group (container) (typed FeaturePython)
  n = 2
  ref = Cl_element
FEATURE [App::DocumentObjectGroupPython] G4_1_2_DICHLOROETHANE  label="G4_1.2-DICHLOROETHANE"  # scripted group (container) (typed FeaturePython)
  Dunit = g/cm3
  Dvalue = 1.2351
  Group = -> [C_element034,H_element031,Cl_element009]
  conduct = 2
  density = 1
  expand = 3
  formula = G4_1.2-DICHLOROETHANE
  name = G4_1.2-DICHLOROETHANE
  specific = 4
FEATURE [App::DocumentObjectGroupPython] C_element035  label="C_element : 019"  # scripted group (container) (typed FeaturePython)
  n = 4
  ref = C_element
FEATURE [App::DocumentObjectGroupPython] H_element032  label="H_element : 015"  # scripted group (container) (typed FeaturePython)
  n = 10
  ref = H_element
FEATURE [App::DocumentObjectGroupPython] O_element032  label="O_element : 015"  # scripted group (container) (typed FeaturePython)
  n = 1
  ref = O_element
FEATURE [App::DocumentObjectGroupPython] G4_DIETHYL_ETHER  # scripted group (container) (typed FeaturePython)
  Dunit = g/cm3
  Dvalue = 0.71378
  Group = -> [C_element035,H_element032,O_element032]
  conduct = 2
  density = 1
  expand = 3
  formula = G4_DIETHYL_ETHER
  name = G4_DIETHYL_ETHER
  specific = 4
FEATURE [App::DocumentObjectGroupPython] C_element036  label="C_element : 020"  # scripted group (container) (typed FeaturePython)
  n = 3
  ref = C_element
FEATURE [App::DocumentObjectGroupPython] H_element033  label="H_element : 016"  # scripted group (container) (typed FeaturePython)
  n = 7
  ref = H_element
FEATURE [App::DocumentObjectGroupPython] N_element015  label="N_element : 008"  # scripted group (container) (typed FeaturePython)
  n = 1
  ref = N_element
FEATURE [App::DocumentObjectGroupPython] O_element033  label="O_element : 016"  # scripted group (container) (typed FeaturePython)
  n = 1
  ref = O_element
FEATURE [App::DocumentObjectGroupPython] G4_N_N_DIMETHYL_FORMAMIDE  label="G4_N.N-DIMETHYL_FORMAMIDE"  # scripted group (container) (typed FeaturePython)
  Dunit = g/cm3
  Dvalue = 0.9487
  Group = -> [C_element036,H_element033,N_element015,O_element033]
  conduct = 2
  density = 1
  expand = 3
  formula = G4_N.N-DIMETHYL_FORMAMIDE
  name = G4_N.N-DIMETHYL_FORMAMIDE
  specific = 4
FEATURE [App::DocumentObjectGroupPython] C_element037  label="C_element : 021"  # scripted group (container) (typed FeaturePython)
  n = 2
  ref = C_element
FEATURE [App::DocumentObjectGroupPython] H_element034  label="H_element : 017"  # scripted group (container) (typed FeaturePython)
  n = 6
  ref = H_element
FEATURE [App::DocumentObjectGroupPython] O_element034  label="O_element : 017"  # scripted group (container) (typed FeaturePython)
  n = 1
  ref = O_element
FEATURE [App::DocumentObjectGroupPython] S_element009  label="S_element : 003"  # scripted group (container) (typed FeaturePython)
  n = 1
  ref = S_element
FEATURE [App::DocumentObjectGroupPython] G4_DIMETHYL_SULFOXIDE  # scripted group (container) (typed FeaturePython)
  Dunit = g/cm3
  Dvalue = 1.1014
  Group = -> [C_element037,H_element034,O_element034,S_element009]
  conduct = 2
  density = 1
  expand = 3
  formula = G4_DIMETHYL_SULFOXIDE
  name = G4_DIMETHYL_SULFOXIDE
  specific = 4
FEATURE [App::DocumentObjectGroupPython] C_element038  label="C_element : 022"  # scripted group (container) (typed FeaturePython)
  n = 2
  ref = C_element
FEATURE [App::DocumentObjectGroupPython] H_element035  label="H_element : 018"  # scripted group (container) (typed FeaturePython)
  n = 6
  ref = H_element
FEATURE [App::DocumentObjectGroupPython] G4_ETHANE  # scripted group (container) (typed FeaturePython)
  Dunit = g/cm3
  Dvalue = 0.00125324
  Group = -> [C_element038,H_element035]
  conduct = 2
  density = 1
  expand = 3
  formula = G4_ETHANE
  name = G4_ETHANE
  specific = 4
FEATURE [App::DocumentObjectGroupPython] C_element039  label="C_element : 023"  # scripted group (container) (typed FeaturePython)
  n = 2
  ref = C_element
FEATURE [App::DocumentObjectGroupPython] H_element036  label="H_element : 019"  # scripted group (container) (typed FeaturePython)
  n = 6
  ref = H_element
FEATURE [App::DocumentObjectGroupPython] O_element035  label="O_element : 018"  # scripted group (container) (typed FeaturePython)
  n = 1
  ref = O_element
FEATURE [App::DocumentObjectGroupPython] G4_ETHYL_ALCOHOL  # scripted group (container) (typed FeaturePython)
  Dunit = g/cm3
  Dvalue = 0.7893
  Group = -> [C_element039,H_element036,O_element035]
  conduct = 2
  density = 1
  expand = 3
  formula = G4_ETHYL_ALCOHOL
  name = G4_ETHYL_ALCOHOL
  specific = 4
FEATURE [App::DocumentObjectGroupPython] H_element037  label="H_element : 0.090"  # scripted group (container) (typed FeaturePython)
  n = 0.090027
FEATURE [App::DocumentObjectGroupPython] C_element040  label="C_element : 0.585"  # scripted group (container) (typed FeaturePython)
  n = 0.585182
FEATURE [App::DocumentObjectGroupPython] O_element036  label="O_element : 0.325"  # scripted group (container) (typed FeaturePython)
  n = 0.324791
FEATURE [App::DocumentObjectGroupPython] G4_ETHYL_CELLULOSE  # scripted group (container) (typed FeaturePython)
  Dunit = g/cm3
  Dvalue = 1.13
  Group = -> [H_element037,C_element040,O_element036]
  conduct = 2
  density = 1
  expand = 3
  formula = G4_ETHYL_CELLULOSE
  name = G4_ETHYL_CELLULOSE
  specific = 4
FEATURE [App::DocumentObjectGroupPython] C_element041  label="C_element : 024"  # scripted group (container) (typed FeaturePython)
  n = 2
  ref = C_element
FEATURE [App::DocumentObjectGroupPython] H_element038  label="H_element : 020"  # scripted group (container) (typed FeaturePython)
  n = 4
  ref = H_element
FEATURE [App::DocumentObjectGroupPython] G4_ETHYLENE  # scripted group (container) (typed FeaturePython)
  Dunit = g/cm3
  Dvalue = 0.00117497
  Group = -> [C_element041,H_element038]
  conduct = 2
  density = 1
  expand = 3
  formula = G4_ETHYLENE
  name = G4_ETHYLENE
  specific = 4
FEATURE [App::DocumentObjectGroupPython] H_element039  label="H_element : 0.096"  # scripted group (container) (typed FeaturePython)
  n = 0.096
FEATURE [App::DocumentObjectGroupPython] C_element042  label="C_element : 0.195"  # scripted group (container) (typed FeaturePython)
  n = 0.195
FEATURE [App::DocumentObjectGroupPython] N_element016  label="N_element : 0.057"  # scripted group (container) (typed FeaturePython)
  n = 0.057
FEATURE [App::DocumentObjectGroupPython] O_element037  label="O_element : 0.646"  # scripted group (container) (typed FeaturePython)
  n = 0.646
FEATURE [App::DocumentObjectGroupPython] Na_element006  label="Na_element : 0.017"  # scripted group (container) (typed FeaturePython)
  n = 0.001
FEATURE [App::DocumentObjectGroupPython] P_element005  label="P_element : 0.104"  # scripted group (container) (typed FeaturePython)
  n = 0.001
FEATURE [App::DocumentObjectGroupPython] S_element010  label="S_element : 0.016"  # scripted group (container) (typed FeaturePython)
  n = 0.003
FEATURE [App::DocumentObjectGroupPython] Cl_element010  label="Cl_element : 0.005"  # scripted group (container) (typed FeaturePython)
  n = 0.001
FEATURE [App::DocumentObjectGroupPython] G4_EYE_LENS_ICRP  # scripted group (container) (typed FeaturePython)
  Dunit = g/cm3
  Dvalue = 1.07
  Group = -> [H_element039,C_element042,N_element016,O_element037,Na_element006,P_element005,S_element010,Cl_element010]
  conduct = 2
  density = 1
  expand = 3
  formula = G4_EYE_LENS_ICRP
  name = G4_EYE_LENS_ICRP
  specific = 4
FEATURE [App::DocumentObjectGroupPython] Fe_element003  label="Fe_element : 2"  # scripted group (container) (typed FeaturePython)
  n = 2
  ref = Fe_element
FEATURE [App::DocumentObjectGroupPython] O_element038  label="O_element : 019"  # scripted group (container) (typed FeaturePython)
  n = 3
  ref = O_element
FEATURE [App::DocumentObjectGroupPython] G4_FERRIC_OXIDE  # scripted group (container) (typed FeaturePython)
  Dunit = g/cm3
  Dvalue = 5.2
  Group = -> [Fe_element003,O_element038]
  conduct = 2
  density = 1
  expand = 3
  formula = G4_FERRIC_OXIDE
  name = G4_FERRIC_OXIDE
  specific = 4
FEATURE [App::DocumentObjectGroupPython] Fe_element004  label="Fe_element : 1"  # scripted group (container) (typed FeaturePython)
  n = 1
  ref = Fe_element
FEATURE [App::DocumentObjectGroupPython] B_element003  label="B_element : 1"  # scripted group (container) (typed FeaturePython)
  n = 1
  ref = B_element
FEATURE [App::DocumentObjectGroupPython] G4_FERROBORIDE  # scripted group (container) (typed FeaturePython)
  Dunit = g/cm3
  Dvalue = 7.15
  Group = -> [Fe_element004,B_element003]
  conduct = 2
  density = 1
  expand = 3
  formula = G4_FERROBORIDE
  name = G4_FERROBORIDE
  specific = 4
FEATURE [App::DocumentObjectGroupPython] Fe_element005  label="Fe_element : 003"  # scripted group (container) (typed FeaturePython)
  n = 1
  ref = Fe_element
FEATURE [App::DocumentObjectGroupPython] O_element039  label="O_element : 020"  # scripted group (container) (typed FeaturePython)
  n = 1
  ref = O_element
FEATURE [App::DocumentObjectGroupPython] G4_FERROUS_OXIDE  # scripted group (container) (typed FeaturePython)
  Dunit = g/cm3
  Dvalue = 5.7
  Group = -> [Fe_element005,O_element039]
  conduct = 2
  density = 1
  expand = 3
  formula = G4_FERROUS_OXIDE
  name = G4_FERROUS_OXIDE
  specific = 4
FEATURE [App::DocumentObjectGroupPython] H_element040  label="H_element : 0.115"  # scripted group (container) (typed FeaturePython)
  n = 0.108259
FEATURE [App::DocumentObjectGroupPython] N_element017  label="N_element : 0.000"  # scripted group (container) (typed FeaturePython)
  n = 2.7e-05
FEATURE [App::DocumentObjectGroupPython] O_element040  label="O_element : 0.879"  # scripted group (container) (typed FeaturePython)
  n = 0.878636
FEATURE [App::DocumentObjectGroupPython] Na_element007  label="Na_element : 0.000"  # scripted group (container) (typed FeaturePython)
  n = 2.2e-05
FEATURE [App::DocumentObjectGroupPython] S_element011  label="S_element : 0.013"  # scripted group (container) (typed FeaturePython)
  n = 0.012968
FEATURE [App::DocumentObjectGroupPython] Cl_element011  label="Cl_element : 0.000"  # scripted group (container) (typed FeaturePython)
  n = 3.4e-05
FEATURE [App::DocumentObjectGroupPython] Fe_element006  label="Fe_element : 0.000"  # scripted group (container) (typed FeaturePython)
  n = 5.4e-05
FEATURE [App::DocumentObjectGroupPython] G4_FERROUS_SULFATE  # scripted group (container) (typed FeaturePython)
  Dunit = g/cm3
  Dvalue = 1.024
  Group = -> [H_element040,N_element017,O_element040,Na_element007,S_element011,Cl_element011,Fe_element006]
  conduct = 2
  density = 1
  expand = 3
  formula = G4_FERROUS_SULFATE
  name = G4_FERROUS_SULFATE
  specific = 4
FEATURE [App::DocumentObjectGroupPython] C_element043  label="C_element : 0.099"  # scripted group (container) (typed FeaturePython)
  n = 0.099335
FEATURE [App::DocumentObjectGroupPython] F_element007  label="F_element : 0.314"  # scripted group (container) (typed FeaturePython)
  n = 0.314247
FEATURE [App::DocumentObjectGroupPython] Cl_element012  label="Cl_element : 0.586"  # scripted group (container) (typed FeaturePython)
  n = 0.586418
FEATURE [App::DocumentObjectGroupPython] G4_FREON_12  label="G4_FREON-12"  # scripted group (container) (typed FeaturePython)
  Dunit = g/cm3
  Dvalue = 1.12
  Group = -> [C_element043,F_element007,Cl_element012]
  conduct = 2
  density = 1
  expand = 3
  formula = G4_FREON-12
  name = G4_FREON-12
  specific = 4
FEATURE [App::DocumentObjectGroupPython] C_element044  label="C_element : 0.057"  # scripted group (container) (typed FeaturePython)
  n = 0.057245
FEATURE [App::DocumentObjectGroupPython] F_element008  label="F_element : 0.181"  # scripted group (container) (typed FeaturePython)
  n = 0.181096
FEATURE [App::DocumentObjectGroupPython] Br_element001  label="Br_element : 0.762"  # scripted group (container) (typed FeaturePython)
  n = 0.761659
FEATURE [App::DocumentObjectGroupPython] G4_FREON_12B2  label="G4_FREON-12B2"  # scripted group (container) (typed FeaturePython)
  Dunit = g/cm3
  Dvalue = 1.8
  Group = -> [C_element044,F_element008,Br_element001]
  conduct = 2
  density = 1
  expand = 3
  formula = G4_FREON-12B2
  name = G4_FREON-12B2
  specific = 4
FEATURE [App::DocumentObjectGroupPython] C_element045  label="C_element : 0.115"  # scripted group (container) (typed FeaturePython)
  n = 0.114983
FEATURE [App::DocumentObjectGroupPython] F_element009  label="F_element : 0.546"  # scripted group (container) (typed FeaturePython)
  n = 0.545621
FEATURE [App::DocumentObjectGroupPython] Cl_element013  label="Cl_element : 0.339"  # scripted group (container) (typed FeaturePython)
  n = 0.339396
FEATURE [App::DocumentObjectGroupPython] G4_FREON_13  label="G4_FREON-13"  # scripted group (container) (typed FeaturePython)
  Dunit = g/cm3
  Dvalue = 0.95
  Group = -> [C_element045,F_element009,Cl_element013]
  conduct = 2
  density = 1
  expand = 3
  formula = G4_FREON-13
  name = G4_FREON-13
  specific = 4
FEATURE [App::DocumentObjectGroupPython] C_element046  label="C_element : 025"  # scripted group (container) (typed FeaturePython)
  n = 1
  ref = C_element
FEATURE [App::DocumentObjectGroupPython] F_element010  label="F_element : 3"  # scripted group (container) (typed FeaturePython)
  n = 3
  ref = F_element
FEATURE [App::DocumentObjectGroupPython] Br_element002  label="Br_element : 1"  # scripted group (container) (typed FeaturePython)
  n = 1
  ref = Br_element
FEATURE [App::DocumentObjectGroupPython] G4_FREON_13B1  label="G4_FREON-13B1"  # scripted group (container) (typed FeaturePython)
  Dunit = g/cm3
  Dvalue = 1.5
  Group = -> [C_element046,F_element010,Br_element002]
  conduct = 2
  density = 1
  expand = 3
  formula = G4_FREON-13B1
  name = G4_FREON-13B1
  specific = 4
FEATURE [App::DocumentObjectGroupPython] C_element047  label="C_element : 0.061"  # scripted group (container) (typed FeaturePython)
  n = 0.061309
FEATURE [App::DocumentObjectGroupPython] F_element011  label="F_element : 0.291"  # scripted group (container) (typed FeaturePython)
  n = 0.290924
FEATURE [App::DocumentObjectGroupPython] I_element002  label="I_element : 0.648"  # scripted group (container) (typed FeaturePython)
  n = 0.647767
FEATURE [App::DocumentObjectGroupPython] G4_FREON_13I1  label="G4_FREON-13I1"  # scripted group (container) (typed FeaturePython)
  Dunit = g/cm3
  Dvalue = 1.8
  Group = -> [C_element047,F_element011,I_element002]
  conduct = 2
  density = 1
  expand = 3
  formula = G4_FREON-13I1
  name = G4_FREON-13I1
  specific = 4
FEATURE [App::DocumentObjectGroupPython] Gd_element001  label="Gd_element : 2"  # scripted group (container) (typed FeaturePython)
  n = 2
  ref = Gd_element
FEATURE [App::DocumentObjectGroupPython] O_element041  label="O_element : 021"  # scripted group (container) (typed FeaturePython)
  n = 2
  ref = O_element
FEATURE [App::DocumentObjectGroupPython] S_element012  label="S_element : 004"  # scripted group (container) (typed FeaturePython)
  n = 1
  ref = S_element
FEATURE [App::DocumentObjectGroupPython] G4_GADOLINIUM_OXYSULFIDE  # scripted group (container) (typed FeaturePython)
  Dunit = g/cm3
  Dvalue = 7.44
  Group = -> [Gd_element001,O_element041,S_element012]
  conduct = 2
  density = 1
  expand = 3
  formula = G4_GADOLINIUM_OXYSULFIDE
  name = G4_GADOLINIUM_OXYSULFIDE
  specific = 4
FEATURE [App::DocumentObjectGroupPython] Ga_element001  label="Ga_element : 1"  # scripted group (container) (typed FeaturePython)
  n = 1
  ref = Ga_element
FEATURE [App::DocumentObjectGroupPython] As_element001  label="As_element : 1"  # scripted group (container) (typed FeaturePython)
  n = 1
  ref = As_element
FEATURE [App::DocumentObjectGroupPython] G4_GALLIUM_ARSENIDE  # scripted group (container) (typed FeaturePython)
  Dunit = g/cm3
  Dvalue = 5.31
  Group = -> [Ga_element001,As_element001]
  conduct = 2
  density = 1
  expand = 3
  formula = G4_GALLIUM_ARSENIDE
  name = G4_GALLIUM_ARSENIDE
  specific = 4
FEATURE [App::DocumentObjectGroupPython] H_element041  label="H_element : 0.081"  # scripted group (container) (typed FeaturePython)
  n = 0.08118
FEATURE [App::DocumentObjectGroupPython] C_element048  label="C_element : 0.416"  # scripted group (container) (typed FeaturePython)
  n = 0.41606
FEATURE [App::DocumentObjectGroupPython] N_element018  label="N_element : 0.111"  # scripted group (container) (typed FeaturePython)
  n = 0.11124
FEATURE [App::DocumentObjectGroupPython] O_element042  label="O_element : 0.381"  # scripted group (container) (typed FeaturePython)
  n = 0.38064
FEATURE [App::DocumentObjectGroupPython] S_element013  label="S_element : 0.011"  # scripted group (container) (typed FeaturePython)
  n = 0.01088
FEATURE [App::DocumentObjectGroupPython] G4_GEL_PHOTO_EMULSION  # scripted group (container) (typed FeaturePython)
  Dunit = g/cm3
  Dvalue = 1.2914
  Group = -> [H_element041,C_element048,N_element018,O_element042,S_element013]
  conduct = 2
  density = 1
  expand = 3
  formula = G4_GEL_PHOTO_EMULSION
  name = G4_GEL_PHOTO_EMULSION
  specific = 4
FEATURE [App::DocumentObjectGroupPython] B_element004  label="B_element : 0.040"  # scripted group (container) (typed FeaturePython)
  n = 0.0400639
FEATURE [App::DocumentObjectGroupPython] O_element043  label="O_element : 0.540"  # scripted group (container) (typed FeaturePython)
  n = 0.539561
FEATURE [App::DocumentObjectGroupPython] Na_element008  label="Na_element : 0.028"  # scripted group (container) (typed FeaturePython)
  n = 0.0281909
FEATURE [App::DocumentObjectGroupPython] Al_element003  label="Al_element : 0.012"  # scripted group (container) (typed FeaturePython)
  n = 0.011644
FEATURE [App::DocumentObjectGroupPython] Si_element003  label="Si_element : 0.377"  # scripted group (container) (typed FeaturePython)
  n = 0.377219
FEATURE [App::DocumentObjectGroupPython] K_element004  label="K_element : 0.014"  # scripted group (container) (typed FeaturePython)
  n = 0.00332099
FEATURE [App::DocumentObjectGroupPython] G4_Pyrex_Glass  # scripted group (container) (typed FeaturePython)
  Dunit = g/cm3
  Dvalue = 2.23
  Group = -> [B_element004,O_element043,Na_element008,Al_element003,Si_element003,K_element004]
  conduct = 2
  density = 1
  expand = 3
  formula = G4_Pyrex_Glass
  name = G4_Pyrex_Glass
  specific = 4
FEATURE [App::DocumentObjectGroupPython] O_element044  label="O_element : 0.156"  # scripted group (container) (typed FeaturePython)
  n = 0.156453
FEATURE [App::DocumentObjectGroupPython] Si_element004  label="Si_element : 0.081"  # scripted group (container) (typed FeaturePython)
  n = 0.080866
FEATURE [App::DocumentObjectGroupPython] Ti_element001  label="Ti_element : 0.008"  # scripted group (container) (typed FeaturePython)
  n = 0.008092
FEATURE [App::DocumentObjectGroupPython] As_element002  label="As_element : 0.003"  # scripted group (container) (typed FeaturePython)
  n = 0.002651
FEATURE [App::DocumentObjectGroupPython] Pb_element001  label="Pb_element : 0.752"  # scripted group (container) (typed FeaturePython)
  n = 0.751938
FEATURE [App::DocumentObjectGroupPython] G4_GLASS_LEAD  # scripted group (container) (typed FeaturePython)
  Dunit = g/cm3
  Dvalue = 6.22
  Group = -> [O_element044,Si_element004,Ti_element001,As_element002,Pb_element001]
  conduct = 2
  density = 1
  expand = 3
  formula = G4_GLASS_LEAD
  name = G4_GLASS_LEAD
  specific = 4
FEATURE [App::DocumentObjectGroupPython] O_element045  label="O_element : 0.460"  # scripted group (container) (typed FeaturePython)
  n = 0.4598
FEATURE [App::DocumentObjectGroupPython] Na_element009  label="Na_element : 0.096"  # scripted group (container) (typed FeaturePython)
  n = 0.0964411
FEATURE [App::DocumentObjectGroupPython] Si_element005  label="Si_element : 0.378"  # scripted group (container) (typed FeaturePython)
  n = 0.336553
FEATURE [App::DocumentObjectGroupPython] Ca_element011  label="Ca_element : 0.107"  # scripted group (container) (typed FeaturePython)
  n = 0.107205
FEATURE [App::DocumentObjectGroupPython] G4_GLASS_PLATE  # scripted group (container) (typed FeaturePython)
  Dunit = g/cm3
  Dvalue = 2.4
  Group = -> [O_element045,Na_element009,Si_element005,Ca_element011]
  conduct = 2
  density = 1
  expand = 3
  formula = G4_GLASS_PLATE
  name = G4_GLASS_PLATE
  specific = 4
FEATURE [App::DocumentObjectGroupPython] C_element049  label="C_element : 026"  # scripted group (container) (typed FeaturePython)
  n = 5
  ref = C_element
FEATURE [App::DocumentObjectGroupPython] H_element042  label="H_element : 021"  # scripted group (container) (typed FeaturePython)
  n = 10
  ref = H_element
FEATURE [App::DocumentObjectGroupPython] N_element019  label="N_element : 2"  # scripted group (container) (typed FeaturePython)
  n = 2
  ref = N_element
FEATURE [App::DocumentObjectGroupPython] O_element046  label="O_element : 022"  # scripted group (container) (typed FeaturePython)
  n = 3
  ref = O_element
FEATURE [App::DocumentObjectGroupPython] G4_GLUTAMINE  # scripted group (container) (typed FeaturePython)
  Dunit = g/cm3
  Dvalue = 1.46
  Group = -> [C_element049,H_element042,N_element019,O_element046]
  conduct = 2
  density = 1
  expand = 3
  formula = G4_GLUTAMINE
  name = G4_GLUTAMINE
  specific = 4
FEATURE [App::DocumentObjectGroupPython] C_element050  label="C_element : 027"  # scripted group (container) (typed FeaturePython)
  n = 3
  ref = C_element
FEATURE [App::DocumentObjectGroupPython] H_element043  label="H_element : 022"  # scripted group (container) (typed FeaturePython)
  n = 8
  ref = H_element
FEATURE [App::DocumentObjectGroupPython] O_element047  label="O_element : 023"  # scripted group (container) (typed FeaturePython)
  n = 3
  ref = O_element
FEATURE [App::DocumentObjectGroupPython] G4_GLYCEROL  # scripted group (container) (typed FeaturePython)
  Dunit = g/cm3
  Dvalue = 1.2613
  Group = -> [C_element050,H_element043,O_element047]
  conduct = 2
  density = 1
  expand = 3
  formula = G4_GLYCEROL
  name = G4_GLYCEROL
  specific = 4
FEATURE [App::DocumentObjectGroupPython] C_element051  label="C_element : 028"  # scripted group (container) (typed FeaturePython)
  n = 5
  ref = C_element
FEATURE [App::DocumentObjectGroupPython] H_element044  label="H_element : 023"  # scripted group (container) (typed FeaturePython)
  n = 5
  ref = H_element
FEATURE [App::DocumentObjectGroupPython] N_element020  label="N_element : 009"  # scripted group (container) (typed FeaturePython)
  n = 5
  ref = N_element
FEATURE [App::DocumentObjectGroupPython] O_element048  label="O_element : 024"  # scripted group (container) (typed FeaturePython)
  n = 1
  ref = O_element
FEATURE [App::DocumentObjectGroupPython] G4_GUANINE  # scripted group (container) (typed FeaturePython)
  Dunit = g/cm3
  Dvalue = 2.2
  Group = -> [C_element051,H_element044,N_element020,O_element048]
  conduct = 2
  density = 1
  expand = 3
  formula = G4_GUANINE
  name = G4_GUANINE
  specific = 4
FEATURE [App::DocumentObjectGroupPython] Ca_element012  label="Ca_element : 006"  # scripted group (container) (typed FeaturePython)
  n = 1
  ref = Ca_element
FEATURE [App::DocumentObjectGroupPython] S_element014  label="S_element : 005"  # scripted group (container) (typed FeaturePython)
  n = 1
  ref = S_element
FEATURE [App::DocumentObjectGroupPython] O_element049  label="O_element : 6"  # scripted group (container) (typed FeaturePython)
  n = 6
  ref = O_element
FEATURE [App::DocumentObjectGroupPython] H_element045  label="H_element : 024"  # scripted group (container) (typed FeaturePython)
  n = 4
  ref = H_element
FEATURE [App::DocumentObjectGroupPython] G4_GYPSUM  # scripted group (container) (typed FeaturePython)
  Dunit = g/cm3
  Dvalue = 2.32
  Group = -> [Ca_element012,S_element014,O_element049,H_element045]
  conduct = 2
  density = 1
  expand = 3
  formula = G4_GYPSUM
  name = G4_GYPSUM
  specific = 4
FEATURE [App::DocumentObjectGroupPython] C_element052  label="C_element : 7"  # scripted group (container) (typed FeaturePython)
  n = 7
  ref = C_element
FEATURE [App::DocumentObjectGroupPython] H_element046  label="H_element : 16"  # scripted group (container) (typed FeaturePython)
  n = 16
  ref = H_element
FEATURE [App::DocumentObjectGroupPython] G4_N_HEPTANE  label="G4_N-HEPTANE"  # scripted group (container) (typed FeaturePython)
  Dunit = g/cm3
  Dvalue = 0.68376
  Group = -> [C_element052,H_element046]
  conduct = 2
  density = 1
  expand = 3
  formula = G4_N-HEPTANE
  name = G4_N-HEPTANE
  specific = 4
FEATURE [App::DocumentObjectGroupPython] C_element053  label="C_element : 029"  # scripted group (container) (typed FeaturePython)
  n = 6
  ref = C_element
FEATURE [App::DocumentObjectGroupPython] H_element047  label="H_element : 14"  # scripted group (container) (typed FeaturePython)
  n = 14
  ref = H_element
FEATURE [App::DocumentObjectGroupPython] G4_N_HEXANE  label="G4_N-HEXANE"  # scripted group (container) (typed FeaturePython)
  Dunit = g/cm3
  Dvalue = 0.6603
  Group = -> [C_element053,H_element047]
  conduct = 2
  density = 1
  expand = 3
  formula = G4_N-HEXANE
  name = G4_N-HEXANE
  specific = 4
FEATURE [App::DocumentObjectGroupPython] C_element054  label="C_element : 22"  # scripted group (container) (typed FeaturePython)
  n = 22
  ref = C_element
FEATURE [App::DocumentObjectGroupPython] H_element048  label="H_element : 025"  # scripted group (container) (typed FeaturePython)
  n = 10
  ref = H_element
FEATURE [App::DocumentObjectGroupPython] N_element021  label="N_element : 010"  # scripted group (container) (typed FeaturePython)
  n = 2
  ref = N_element
FEATURE [App::DocumentObjectGroupPython] O_element050  label="O_element : 025"  # scripted group (container) (typed FeaturePython)
  n = 5
  ref = O_element
FEATURE [App::DocumentObjectGroupPython] G4_KAPTON  # scripted group (container) (typed FeaturePython)
  Dunit = g/cm3
  Dvalue = 1.42
  Group = -> [C_element054,H_element048,N_element021,O_element050]
  conduct = 2
  density = 1
  expand = 3
  formula = G4_KAPTON
  name = G4_KAPTON
  specific = 4
FEATURE [App::DocumentObjectGroupPython] La_element001  label="La_element : 1"  # scripted group (container) (typed FeaturePython)
  n = 1
  ref = La_element
FEATURE [App::DocumentObjectGroupPython] Br_element003  label="Br_element : 002"  # scripted group (container) (typed FeaturePython)
  n = 1
  ref = Br_element
FEATURE [App::DocumentObjectGroupPython] O_element051  label="O_element : 026"  # scripted group (container) (typed FeaturePython)
  n = 1
  ref = O_element
FEATURE [App::DocumentObjectGroupPython] G4_LANTHANUM_OXYBROMIDE  # scripted group (container) (typed FeaturePython)
  Dunit = g/cm3
  Dvalue = 6.28
  Group = -> [La_element001,Br_element003,O_element051]
  conduct = 2
  density = 1
  expand = 3
  formula = G4_LANTHANUM_OXYBROMIDE
  name = G4_LANTHANUM_OXYBROMIDE
  specific = 4
FEATURE [App::DocumentObjectGroupPython] La_element002  label="La_element : 2"  # scripted group (container) (typed FeaturePython)
  n = 2
  ref = La_element
FEATURE [App::DocumentObjectGroupPython] O_element052  label="O_element : 027"  # scripted group (container) (typed FeaturePython)
  n = 2
  ref = O_element
FEATURE [App::DocumentObjectGroupPython] S_element015  label="S_element : 006"  # scripted group (container) (typed FeaturePython)
  n = 1
  ref = S_element
FEATURE [App::DocumentObjectGroupPython] G4_LANTHANUM_OXYSULFIDE  # scripted group (container) (typed FeaturePython)
  Dunit = g/cm3
  Dvalue = 5.86
  Group = -> [La_element002,O_element052,S_element015]
  conduct = 2
  density = 1
  expand = 3
  formula = G4_LANTHANUM_OXYSULFIDE
  name = G4_LANTHANUM_OXYSULFIDE
  specific = 4
FEATURE [App::DocumentObjectGroupPython] O_element053  label="O_element : 0.072"  # scripted group (container) (typed FeaturePython)
  n = 0.071682
FEATURE [App::DocumentObjectGroupPython] Pb_element002  label="Pb_element : 0.928"  # scripted group (container) (typed FeaturePython)
  n = 0.928318
FEATURE [App::DocumentObjectGroupPython] G4_LEAD_OXIDE  # scripted group (container) (typed FeaturePython)
  Dunit = g/cm3
  Dvalue = 9.53
  Group = -> [O_element053,Pb_element002]
  conduct = 2
  density = 1
  expand = 3
  formula = G4_LEAD_OXIDE
  name = G4_LEAD_OXIDE
  specific = 4
FEATURE [App::DocumentObjectGroupPython] Li_element001  label="Li_element : 1"  # scripted group (container) (typed FeaturePython)
  n = 1
  ref = Li_element
FEATURE [App::DocumentObjectGroupPython] N_element022  label="N_element : 011"  # scripted group (container) (typed FeaturePython)
  n = 1
  ref = N_element
FEATURE [App::DocumentObjectGroupPython] H_element049  label="H_element : 026"  # scripted group (container) (typed FeaturePython)
  n = 2
  ref = H_element
FEATURE [App::DocumentObjectGroupPython] G4_LITHIUM_AMIDE  # scripted group (container) (typed FeaturePython)
  Dunit = g/cm3
  Dvalue = 1.178
  Group = -> [Li_element001,N_element022,H_element049]
  conduct = 2
  density = 1
  expand = 3
  formula = G4_LITHIUM_AMIDE
  name = G4_LITHIUM_AMIDE
  specific = 4
FEATURE [App::DocumentObjectGroupPython] Li_element002  label="Li_element : 2"  # scripted group (container) (typed FeaturePython)
  n = 2
  ref = Li_element
FEATURE [App::DocumentObjectGroupPython] C_element055  label="C_element : 030"  # scripted group (container) (typed FeaturePython)
  n = 1
  ref = C_element
FEATURE [App::DocumentObjectGroupPython] O_element054  label="O_element : 028"  # scripted group (container) (typed FeaturePython)
  n = 3
  ref = O_element
FEATURE [App::DocumentObjectGroupPython] G4_LITHIUM_CARBONATE  # scripted group (container) (typed FeaturePython)
  Dunit = g/cm3
  Dvalue = 2.11
  Group = -> [Li_element002,C_element055,O_element054]
  conduct = 2
  density = 1
  expand = 3
  formula = G4_LITHIUM_CARBONATE
  name = G4_LITHIUM_CARBONATE
  specific = 4
FEATURE [App::DocumentObjectGroupPython] Li_element003  label="Li_element : 003"  # scripted group (container) (typed FeaturePython)
  n = 1
  ref = Li_element
FEATURE [App::DocumentObjectGroupPython] F_element012  label="F_element : 004"  # scripted group (container) (typed FeaturePython)
  n = 1
  ref = F_element
FEATURE [App::DocumentObjectGroupPython] G4_LITHIUM_FLUORIDE  # scripted group (container) (typed FeaturePython)
  Dunit = g/cm3
  Dvalue = 2.635
  Group = -> [Li_element003,F_element012]
  conduct = 2
  density = 1
  expand = 3
  formula = G4_LITHIUM_FLUORIDE
  name = G4_LITHIUM_FLUORIDE
  specific = 4
FEATURE [App::DocumentObjectGroupPython] Li_element004  label="Li_element : 004"  # scripted group (container) (typed FeaturePython)
  n = 1
  ref = Li_element
FEATURE [App::DocumentObjectGroupPython] H_element050  label="H_element : 027"  # scripted group (container) (typed FeaturePython)
  n = 1
  ref = H_element
FEATURE [App::DocumentObjectGroupPython] G4_LITHIUM_HYDRIDE  # scripted group (container) (typed FeaturePython)
  Dunit = g/cm3
  Dvalue = 0.82
  Group = -> [Li_element004,H_element050]
  conduct = 2
  density = 1
  expand = 3
  formula = G4_LITHIUM_HYDRIDE
  name = G4_LITHIUM_HYDRIDE
  specific = 4
FEATURE [App::DocumentObjectGroupPython] Li_element005  label="Li_element : 005"  # scripted group (container) (typed FeaturePython)
  n = 1
  ref = Li_element
FEATURE [App::DocumentObjectGroupPython] I_element003  label="I_element : 002"  # scripted group (container) (typed FeaturePython)
  n = 1
  ref = I_element
FEATURE [App::DocumentObjectGroupPython] G4_LITHIUM_IODIDE  # scripted group (container) (typed FeaturePython)
  Dunit = g/cm3
  Dvalue = 3.494
  Group = -> [Li_element005,I_element003]
  conduct = 2
  density = 1
  expand = 3
  formula = G4_LITHIUM_IODIDE
  name = G4_LITHIUM_IODIDE
  specific = 4
FEATURE [App::DocumentObjectGroupPython] Li_element006  label="Li_element : 006"  # scripted group (container) (typed FeaturePython)
  n = 2
  ref = Li_element
FEATURE [App::DocumentObjectGroupPython] O_element055  label="O_element : 029"  # scripted group (container) (typed FeaturePython)
  n = 1
  ref = O_element
FEATURE [App::DocumentObjectGroupPython] G4_LITHIUM_OXIDE  # scripted group (container) (typed FeaturePython)
  Dunit = g/cm3
  Dvalue = 2.013
  Group = -> [Li_element006,O_element055]
  conduct = 2
  density = 1
  expand = 3
  formula = G4_LITHIUM_OXIDE
  name = G4_LITHIUM_OXIDE
  specific = 4
FEATURE [App::DocumentObjectGroupPython] Li_element007  label="Li_element : 007"  # scripted group (container) (typed FeaturePython)
  n = 2
  ref = Li_element
FEATURE [App::DocumentObjectGroupPython] B_element005  label="B_element : 005"  # scripted group (container) (typed FeaturePython)
  n = 4
  ref = B_element
FEATURE [App::DocumentObjectGroupPython] O_element056  label="O_element : 7"  # scripted group (container) (typed FeaturePython)
  n = 7
  ref = O_element
FEATURE [App::DocumentObjectGroupPython] G4_LITHIUM_TETRABORATE  # scripted group (container) (typed FeaturePython)
  Dunit = g/cm3
  Dvalue = 2.44
  Group = -> [Li_element007,B_element005,O_element056]
  conduct = 2
  density = 1
  expand = 3
  formula = G4_LITHIUM_TETRABORATE
  name = G4_LITHIUM_TETRABORATE
  specific = 4
FEATURE [App::DocumentObjectGroupPython] H_element051  label="H_element : 0.105"  # scripted group (container) (typed FeaturePython)
  n = 0.105
FEATURE [App::DocumentObjectGroupPython] C_element056  label="C_element : 0.083"  # scripted group (container) (typed FeaturePython)
  n = 0.083
FEATURE [App::DocumentObjectGroupPython] N_element023  label="N_element : 0.023"  # scripted group (container) (typed FeaturePython)
  n = 0.023
FEATURE [App::DocumentObjectGroupPython] O_element057  label="O_element : 0.779"  # scripted group (container) (typed FeaturePython)
  n = 0.779
FEATURE [App::DocumentObjectGroupPython] Na_element010  label="Na_element : 0.097"  # scripted group (container) (typed FeaturePython)
  n = 0.002
FEATURE [App::DocumentObjectGroupPython] P_element006  label="P_element : 0.105"  # scripted group (container) (typed FeaturePython)
  n = 0.001
FEATURE [App::DocumentObjectGroupPython] S_element016  label="S_element : 0.017"  # scripted group (container) (typed FeaturePython)
  n = 0.002
FEATURE [App::DocumentObjectGroupPython] Cl_element014  label="Cl_element : 0.587"  # scripted group (container) (typed FeaturePython)
  n = 0.003
FEATURE [App::DocumentObjectGroupPython] K_element005  label="K_element : 0.015"  # scripted group (container) (typed FeaturePython)
  n = 0.002
FEATURE [App::DocumentObjectGroupPython] G4_LUNG_ICRP  # scripted group (container) (typed FeaturePython)
  Dunit = g/cm3
  Dvalue = 1.04
  Group = -> [H_element051,C_element056,N_element023,O_element057,Na_element010,P_element006,S_element016,Cl_element014,K_element005]
  conduct = 2
  density = 1
  expand = 3
  formula = G4_LUNG_ICRP
  name = G4_LUNG_ICRP
  specific = 4
FEATURE [App::DocumentObjectGroupPython] H_element052  label="H_element : 0.116"  # scripted group (container) (typed FeaturePython)
  n = 0.114318
FEATURE [App::DocumentObjectGroupPython] C_element057  label="C_element : 0.656"  # scripted group (container) (typed FeaturePython)
  n = 0.655824
FEATURE [App::DocumentObjectGroupPython] O_element058  label="O_element : 0.092"  # scripted group (container) (typed FeaturePython)
  n = 0.0921831
FEATURE [App::DocumentObjectGroupPython] Mg_element004  label="Mg_element : 0.135"  # scripted group (container) (typed FeaturePython)
  n = 0.134792
FEATURE [App::DocumentObjectGroupPython] Ca_element013  label="Ca_element : 0.003"  # scripted group (container) (typed FeaturePython)
  n = 0.002883
FEATURE [App::DocumentObjectGroupPython] G4_M3_WAX  # scripted group (container) (typed FeaturePython)
  Dunit = g/cm3
  Dvalue = 1.05
  Group = -> [H_element052,C_element057,O_element058,Mg_element004,Ca_element013]
  conduct = 2
  density = 1
  expand = 3
  formula = G4_M3_WAX
  name = G4_M3_WAX
  specific = 4
FEATURE [App::DocumentObjectGroupPython] Mg_element005  label="Mg_element : 1"  # scripted group (container) (typed FeaturePython)
  n = 1
  ref = Mg_element
FEATURE [App::DocumentObjectGroupPython] C_element058  label="C_element : 031"  # scripted group (container) (typed FeaturePython)
  n = 1
  ref = C_element
FEATURE [App::DocumentObjectGroupPython] O_element059  label="O_element : 030"  # scripted group (container) (typed FeaturePython)
  n = 3
  ref = O_element
FEATURE [App::DocumentObjectGroupPython] G4_MAGNESIUM_CARBONATE  # scripted group (container) (typed FeaturePython)
  Dunit = g/cm3
  Dvalue = 2.958
  Group = -> [Mg_element005,C_element058,O_element059]
  conduct = 2
  density = 1
  expand = 3
  formula = G4_MAGNESIUM_CARBONATE
  name = G4_MAGNESIUM_CARBONATE
  specific = 4
FEATURE [App::DocumentObjectGroupPython] Mg_element006  label="Mg_element : 002"  # scripted group (container) (typed FeaturePython)
  n = 1
  ref = Mg_element
FEATURE [App::DocumentObjectGroupPython] F_element013  label="F_element : 005"  # scripted group (container) (typed FeaturePython)
  n = 2
  ref = F_element
FEATURE [App::DocumentObjectGroupPython] G4_MAGNESIUM_FLUORIDE  # scripted group (container) (typed FeaturePython)
  Dunit = g/cm3
  Dvalue = 3
  Group = -> [Mg_element006,F_element013]
  conduct = 2
  density = 1
  expand = 3
  formula = G4_MAGNESIUM_FLUORIDE
  name = G4_MAGNESIUM_FLUORIDE
  specific = 4
FEATURE [App::DocumentObjectGroupPython] Mg_element007  label="Mg_element : 003"  # scripted group (container) (typed FeaturePython)
  n = 1
  ref = Mg_element
FEATURE [App::DocumentObjectGroupPython] O_element060  label="O_element : 031"  # scripted group (container) (typed FeaturePython)
  n = 1
  ref = O_element
FEATURE [App::DocumentObjectGroupPython] G4_MAGNESIUM_OXIDE  # scripted group (container) (typed FeaturePython)
  Dunit = g/cm3
  Dvalue = 3.58
  Group = -> [Mg_element007,O_element060]
  conduct = 2
  density = 1
  expand = 3
  formula = G4_MAGNESIUM_OXIDE
  name = G4_MAGNESIUM_OXIDE
  specific = 4
FEATURE [App::DocumentObjectGroupPython] Mg_element008  label="Mg_element : 004"  # scripted group (container) (typed FeaturePython)
  n = 1
  ref = Mg_element
FEATURE [App::DocumentObjectGroupPython] B_element006  label="B_element : 006"  # scripted group (container) (typed FeaturePython)
  n = 4
  ref = B_element
FEATURE [App::DocumentObjectGroupPython] O_element061  label="O_element : 032"  # scripted group (container) (typed FeaturePython)
  n = 7
  ref = O_element
FEATURE [App::DocumentObjectGroupPython] G4_MAGNESIUM_TETRABORATE  # scripted group (container) (typed FeaturePython)
  Dunit = g/cm3
  Dvalue = 2.53
  Group = -> [Mg_element008,B_element006,O_element061]
  conduct = 2
  density = 1
  expand = 3
  formula = G4_MAGNESIUM_TETRABORATE
  name = G4_MAGNESIUM_TETRABORATE
  specific = 4
FEATURE [App::DocumentObjectGroupPython] Hg_element001  label="Hg_element : 1"  # scripted group (container) (typed FeaturePython)
  n = 1
  ref = Hg_element
FEATURE [App::DocumentObjectGroupPython] I_element004  label="I_element : 2"  # scripted group (container) (typed FeaturePython)
  n = 2
  ref = I_element
FEATURE [App::DocumentObjectGroupPython] G4_MERCURIC_IODIDE  # scripted group (container) (typed FeaturePython)
  Dunit = g/cm3
  Dvalue = 6.36
  Group = -> [Hg_element001,I_element004]
  conduct = 2
  density = 1
  expand = 3
  formula = G4_MERCURIC_IODIDE
  name = G4_MERCURIC_IODIDE
  specific = 4
FEATURE [App::DocumentObjectGroupPython] C_element059  label="C_element : 032"  # scripted group (container) (typed FeaturePython)
  n = 1
  ref = C_element
FEATURE [App::DocumentObjectGroupPython] H_element053  label="H_element : 028"  # scripted group (container) (typed FeaturePython)
  n = 4
  ref = H_element
FEATURE [App::DocumentObjectGroupPython] G4_METHANE  # scripted group (container) (typed FeaturePython)
  Dunit = g/cm3
  Dvalue = 0.000667151
  Group = -> [C_element059,H_element053]
  conduct = 2
  density = 1
  expand = 3
  formula = G4_METHANE
  name = G4_METHANE
  specific = 4
FEATURE [App::DocumentObjectGroupPython] C_element060  label="C_element : 033"  # scripted group (container) (typed FeaturePython)
  n = 1
  ref = C_element
FEATURE [App::DocumentObjectGroupPython] H_element054  label="H_element : 029"  # scripted group (container) (typed FeaturePython)
  n = 4
  ref = H_element
FEATURE [App::DocumentObjectGroupPython] O_element062  label="O_element : 033"  # scripted group (container) (typed FeaturePython)
  n = 1
  ref = O_element
FEATURE [App::DocumentObjectGroupPython] G4_METHANOL  # scripted group (container) (typed FeaturePython)
  Dunit = g/cm3
  Dvalue = 0.7914
  Group = -> [C_element060,H_element054,O_element062]
  conduct = 2
  density = 1
  expand = 3
  formula = G4_METHANOL
  name = G4_METHANOL
  specific = 4
FEATURE [App::DocumentObjectGroupPython] H_element055  label="H_element : 0.134"  # scripted group (container) (typed FeaturePython)
  n = 0.13404
FEATURE [App::DocumentObjectGroupPython] C_element061  label="C_element : 0.778"  # scripted group (container) (typed FeaturePython)
  n = 0.77796
FEATURE [App::DocumentObjectGroupPython] O_element063  label="O_element : 0.035"  # scripted group (container) (typed FeaturePython)
  n = 0.03502
FEATURE [App::DocumentObjectGroupPython] Mg_element009  label="Mg_element : 0.039"  # scripted group (container) (typed FeaturePython)
  n = 0.038594
FEATURE [App::DocumentObjectGroupPython] Ti_element002  label="Ti_element : 0.014"  # scripted group (container) (typed FeaturePython)
  n = 0.014386
FEATURE [App::DocumentObjectGroupPython] G4_MIX_D_WAX  # scripted group (container) (typed FeaturePython)
  Dunit = g/cm3
  Dvalue = 0.99
  Group = -> [H_element055,C_element061,O_element063,Mg_element009,Ti_element002]
  conduct = 2
  density = 1
  expand = 3
  formula = G4_MIX_D_WAX
  name = G4_MIX_D_WAX
  specific = 4
FEATURE [App::DocumentObjectGroupPython] H_element056  label="H_element : 0.135"  # scripted group (container) (typed FeaturePython)
  n = 0.081192
FEATURE [App::DocumentObjectGroupPython] C_element062  label="C_element : 0.583"  # scripted group (container) (typed FeaturePython)
  n = 0.583442
FEATURE [App::DocumentObjectGroupPython] N_element024  label="N_element : 0.018"  # scripted group (container) (typed FeaturePython)
  n = 0.017798
FEATURE [App::DocumentObjectGroupPython] O_element064  label="O_element : 0.186"  # scripted group (container) (typed FeaturePython)
  n = 0.186381
FEATURE [App::DocumentObjectGroupPython] Mg_element010  label="Mg_element : 0.130"  # scripted group (container) (typed FeaturePython)
  n = 0.130287
FEATURE [App::DocumentObjectGroupPython] Cl_element015  label="Cl_element : 0.588"  # scripted group (container) (typed FeaturePython)
  n = 0.0009
FEATURE [App::DocumentObjectGroupPython] G4_MS20_TISSUE  # scripted group (container) (typed FeaturePython)
  Dunit = g/cm3
  Dvalue = 1
  Group = -> [H_element056,C_element062,N_element024,O_element064,Mg_element010,Cl_element015]
  conduct = 2
  density = 1
  expand = 3
  formula = G4_MS20_TISSUE
  name = G4_MS20_TISSUE
  specific = 4
FEATURE [App::DocumentObjectGroupPython] H_element057  label="H_element : 0.136"  # scripted group (container) (typed FeaturePython)
  n = 0.102
FEATURE [App::DocumentObjectGroupPython] C_element063  label="C_element : 0.143"  # scripted group (container) (typed FeaturePython)
  n = 0.143
FEATURE [App::DocumentObjectGroupPython] N_element025  label="N_element : 0.034"  # scripted group (container) (typed FeaturePython)
  n = 0.034
FEATURE [App::DocumentObjectGroupPython] O_element065  label="O_element : 0.710"  # scripted group (container) (typed FeaturePython)
  n = 0.71
FEATURE [App::DocumentObjectGroupPython] Na_element011  label="Na_element : 0.098"  # scripted group (container) (typed FeaturePython)
  n = 0.001
FEATURE [App::DocumentObjectGroupPython] P_element007  label="P_element : 0.002"  # scripted group (container) (typed FeaturePython)
  n = 0.002
FEATURE [App::DocumentObjectGroupPython] S_element017  label="S_element : 0.018"  # scripted group (container) (typed FeaturePython)
  n = 0.003
FEATURE [App::DocumentObjectGroupPython] Cl_element016  label="Cl_element : 0.589"  # scripted group (container) (typed FeaturePython)
  n = 0.001
FEATURE [App::DocumentObjectGroupPython] K_element006  label="K_element : 0.004"  # scripted group (container) (typed FeaturePython)
  n = 0.004
FEATURE [App::DocumentObjectGroupPython] G4_MUSCLE_SKELETAL_ICRP  # scripted group (container) (typed FeaturePython)
  Dunit = g/cm3
  Dvalue = 1.05
  Group = -> [H_element057,C_element063,N_element025,O_element065,Na_element011,P_element007,S_element017,Cl_element016,K_element006]
  conduct = 2
  density = 1
  expand = 3
  formula = G4_MUSCLE_SKELETAL_ICRP
  name = G4_MUSCLE_SKELETAL_ICRP
  specific = 4
FEATURE [App::DocumentObjectGroupPython] H_element058  label="H_element : 0.137"  # scripted group (container) (typed FeaturePython)
  n = 0.102102
FEATURE [App::DocumentObjectGroupPython] C_element064  label="C_element : 0.123"  # scripted group (container) (typed FeaturePython)
  n = 0.123123
FEATURE [App::DocumentObjectGroupPython] N_element026  label="N_element : 0.756"  # scripted group (container) (typed FeaturePython)
  n = 0.035035
FEATURE [App::DocumentObjectGroupPython] O_element066  label="O_element : 0.730"  # scripted group (container) (typed FeaturePython)
  n = 0.72973
FEATURE [App::DocumentObjectGroupPython] Na_element012  label="Na_element : 0.099"  # scripted group (container) (typed FeaturePython)
  n = 0.001001
FEATURE [App::DocumentObjectGroupPython] P_element008  label="P_element : 0.106"  # scripted group (container) (typed FeaturePython)
  n = 0.002002
FEATURE [App::DocumentObjectGroupPython] S_element018  label="S_element : 0.019"  # scripted group (container) (typed FeaturePython)
  n = 0.004004
FEATURE [App::DocumentObjectGroupPython] K_element007  label="K_element : 0.016"  # scripted group (container) (typed FeaturePython)
  n = 0.003003
FEATURE [App::DocumentObjectGroupPython] G4_MUSCLE_STRIATED_ICRU  # scripted group (container) (typed FeaturePython)
  Dunit = g/cm3
  Dvalue = 1.04
  Group = -> [H_element058,C_element064,N_element026,O_element066,Na_element012,P_element008,S_element018,K_element007]
  conduct = 2
  density = 1
  expand = 3
  formula = G4_MUSCLE_STRIATED_ICRU
  name = G4_MUSCLE_STRIATED_ICRU
  specific = 4
FEATURE [App::DocumentObjectGroupPython] H_element059  label="H_element : 0.098"  # scripted group (container) (typed FeaturePython)
  n = 0.0982341
FEATURE [App::DocumentObjectGroupPython] C_element065  label="C_element : 0.156"  # scripted group (container) (typed FeaturePython)
  n = 0.156214
FEATURE [App::DocumentObjectGroupPython] N_element027  label="N_element : 0.757"  # scripted group (container) (typed FeaturePython)
  n = 0.035451
FEATURE [App::DocumentObjectGroupPython] O_element067  label="O_element : 0.880"  # scripted group (container) (typed FeaturePython)
  n = 0.710101
FEATURE [App::DocumentObjectGroupPython] G4_MUSCLE_WITH_SUCROSE  # scripted group (container) (typed FeaturePython)
  Dunit = g/cm3
  Dvalue = 1.11
  Group = -> [H_element059,C_element065,N_element027,O_element067]
  conduct = 2
  density = 1
  expand = 3
  formula = G4_MUSCLE_WITH_SUCROSE
  name = G4_MUSCLE_WITH_SUCROSE
  specific = 4
FEATURE [App::DocumentObjectGroupPython] H_element060  label="H_element : 0.138"  # scripted group (container) (typed FeaturePython)
  n = 0.101969
FEATURE [App::DocumentObjectGroupPython] C_element066  label="C_element : 0.120"  # scripted group (container) (typed FeaturePython)
  n = 0.120058
FEATURE [App::DocumentObjectGroupPython] N_element028  label="N_element : 0.758"  # scripted group (container) (typed FeaturePython)
  n = 0.035451
FEATURE [App::DocumentObjectGroupPython] O_element068  label="O_element : 0.743"  # scripted group (container) (typed FeaturePython)
  n = 0.742522
FEATURE [App::DocumentObjectGroupPython] G4_MUSCLE_WITHOUT_SUCROSE  # scripted group (container) (typed FeaturePython)
  Dunit = g/cm3
  Dvalue = 1.07
  Group = -> [H_element060,C_element066,N_element028,O_element068]
  conduct = 2
  density = 1
  expand = 3
  formula = G4_MUSCLE_WITHOUT_SUCROSE
  name = G4_MUSCLE_WITHOUT_SUCROSE
  specific = 4
FEATURE [App::DocumentObjectGroupPython] C_element067  label="C_element : 10"  # scripted group (container) (typed FeaturePython)
  n = 10
  ref = C_element
FEATURE [App::DocumentObjectGroupPython] H_element061  label="H_element : 030"  # scripted group (container) (typed FeaturePython)
  n = 8
  ref = H_element
FEATURE [App::DocumentObjectGroupPython] G4_NAPHTHALENE  # scripted group (container) (typed FeaturePython)
  Dunit = g/cm3
  Dvalue = 1.145
  Group = -> [C_element067,H_element061]
  conduct = 2
  density = 1
  expand = 3
  formula = G4_NAPHTHALENE
  name = G4_NAPHTHALENE
  specific = 4
FEATURE [App::DocumentObjectGroupPython] C_element068  label="C_element : 034"  # scripted group (container) (typed FeaturePython)
  n = 6
  ref = C_element
FEATURE [App::DocumentObjectGroupPython] H_element062  label="H_element : 031"  # scripted group (container) (typed FeaturePython)
  n = 5
  ref = H_element
FEATURE [App::DocumentObjectGroupPython] N_element029  label="N_element : 012"  # scripted group (container) (typed FeaturePython)
  n = 1
  ref = N_element
FEATURE [App::DocumentObjectGroupPython] O_element069  label="O_element : 034"  # scripted group (container) (typed FeaturePython)
  n = 2
  ref = O_element
FEATURE [App::DocumentObjectGroupPython] G4_NITROBENZENE  # scripted group (container) (typed FeaturePython)
  Dunit = g/cm3
  Dvalue = 1.19867
  Group = -> [C_element068,H_element062,N_element029,O_element069]
  conduct = 2
  density = 1
  expand = 3
  formula = G4_NITROBENZENE
  name = G4_NITROBENZENE
  specific = 4
FEATURE [App::DocumentObjectGroupPython] N_element030  label="N_element : 013"  # scripted group (container) (typed FeaturePython)
  n = 2
  ref = N_element
FEATURE [App::DocumentObjectGroupPython] O_element070  label="O_element : 035"  # scripted group (container) (typed FeaturePython)
  n = 1
  ref = O_element
FEATURE [App::DocumentObjectGroupPython] G4_NITROUS_OXIDE  # scripted group (container) (typed FeaturePython)
  Dunit = g/cm3
  Dvalue = 0.00183094
  Group = -> [N_element030,O_element070]
  conduct = 2
  density = 1
  expand = 3
  formula = G4_NITROUS_OXIDE
  name = G4_NITROUS_OXIDE
  specific = 4
FEATURE [App::DocumentObjectGroupPython] H_element063  label="H_element : 0.104"  # scripted group (container) (typed FeaturePython)
  n = 0.103509
FEATURE [App::DocumentObjectGroupPython] C_element069  label="C_element : 0.648"  # scripted group (container) (typed FeaturePython)
  n = 0.648416
FEATURE [App::DocumentObjectGroupPython] N_element031  label="N_element : 0.100"  # scripted group (container) (typed FeaturePython)
  n = 0.0995361
FEATURE [App::DocumentObjectGroupPython] O_element071  label="O_element : 0.149"  # scripted group (container) (typed FeaturePython)
  n = 0.148539
FEATURE [App::DocumentObjectGroupPython] G4_NYLON_8062  label="G4_NYLON-8062"  # scripted group (container) (typed FeaturePython)
  Dunit = g/cm3
  Dvalue = 1.08
  Group = -> [H_element063,C_element069,N_element031,O_element071]
  conduct = 2
  density = 1
  expand = 3
  formula = G4_NYLON-8062
  name = G4_NYLON-8062
  specific = 4
FEATURE [App::DocumentObjectGroupPython] C_element070  label="C_element : 035"  # scripted group (container) (typed FeaturePython)
  n = 6
  ref = C_element
FEATURE [App::DocumentObjectGroupPython] H_element064  label="H_element : 11"  # scripted group (container) (typed FeaturePython)
  n = 11
  ref = H_element
FEATURE [App::DocumentObjectGroupPython] N_element032  label="N_element : 014"  # scripted group (container) (typed FeaturePython)
  n = 1
  ref = N_element
FEATURE [App::DocumentObjectGroupPython] O_element072  label="O_element : 036"  # scripted group (container) (typed FeaturePython)
  n = 1
  ref = O_element
FEATURE [App::DocumentObjectGroupPython] G4_NYLON_6_6  label="G4_NYLON-6-6"  # scripted group (container) (typed FeaturePython)
  Dunit = g/cm3
  Dvalue = 1.14
  Group = -> [C_element070,H_element064,N_element032,O_element072]
  conduct = 2
  density = 1
  expand = 3
  formula = G4_NYLON-6-6
  name = G4_NYLON-6-6
  specific = 4
FEATURE [App::DocumentObjectGroupPython] H_element065  label="H_element : 0.139"  # scripted group (container) (typed FeaturePython)
  n = 0.107062
FEATURE [App::DocumentObjectGroupPython] C_element071  label="C_element : 0.680"  # scripted group (container) (typed FeaturePython)
  n = 0.680449
FEATURE [App::DocumentObjectGroupPython] N_element033  label="N_element : 0.099"  # scripted group (container) (typed FeaturePython)
  n = 0.099189
FEATURE [App::DocumentObjectGroupPython] O_element073  label="O_element : 0.113"  # scripted group (container) (typed FeaturePython)
  n = 0.1133
FEATURE [App::DocumentObjectGroupPython] G4_NYLON_6_10  label="G4_NYLON-6-10"  # scripted group (container) (typed FeaturePython)
  Dunit = g/cm3
  Dvalue = 1.14
  Group = -> [H_element065,C_element071,N_element033,O_element073]
  conduct = 2
  density = 1
  expand = 3
  formula = G4_NYLON-6-10
  name = G4_NYLON-6-10
  specific = 4
FEATURE [App::DocumentObjectGroupPython] H_element066  label="H_element : 0.140"  # scripted group (container) (typed FeaturePython)
  n = 0.115476
FEATURE [App::DocumentObjectGroupPython] C_element072  label="C_element : 0.721"  # scripted group (container) (typed FeaturePython)
  n = 0.720818
FEATURE [App::DocumentObjectGroupPython] N_element034  label="N_element : 0.076"  # scripted group (container) (typed FeaturePython)
  n = 0.0764169
FEATURE [App::DocumentObjectGroupPython] O_element074  label="O_element : 0.087"  # scripted group (container) (typed FeaturePython)
  n = 0.0872889
FEATURE [App::DocumentObjectGroupPython] G4_NYLON_11_RILSAN  label="G4_NYLON-11_RILSAN"  # scripted group (container) (typed FeaturePython)
  Dunit = g/cm3
  Dvalue = 1.425
  Group = -> [H_element066,C_element072,N_element034,O_element074]
  conduct = 2
  density = 1
  expand = 3
  formula = G4_NYLON-11_RILSAN
  name = G4_NYLON-11_RILSAN
  specific = 4
FEATURE [App::DocumentObjectGroupPython] C_element073  label="C_element : 8"  # scripted group (container) (typed FeaturePython)
  n = 8
  ref = C_element
FEATURE [App::DocumentObjectGroupPython] H_element067  label="H_element : 18"  # scripted group (container) (typed FeaturePython)
  n = 18
  ref = H_element
FEATURE [App::DocumentObjectGroupPython] G4_OCTANE  # scripted group (container) (typed FeaturePython)
  Dunit = g/cm3
  Dvalue = 0.7026
  Group = -> [C_element073,H_element067]
  conduct = 2
  density = 1
  expand = 3
  formula = G4_OCTANE
  name = G4_OCTANE
  specific = 4
FEATURE [App::DocumentObjectGroupPython] C_element074  label="C_element : 25"  # scripted group (container) (typed FeaturePython)
  n = 25
  ref = C_element
FEATURE [App::DocumentObjectGroupPython] H_element068  label="H_element : 52"  # scripted group (container) (typed FeaturePython)
  n = 52
  ref = H_element
FEATURE [App::DocumentObjectGroupPython] G4_PARAFFIN  # scripted group (container) (typed FeaturePython)
  Dunit = g/cm3
  Dvalue = 0.93
  Group = -> [C_element074,H_element068]
  conduct = 2
  density = 1
  expand = 3
  formula = G4_PARAFFIN
  name = G4_PARAFFIN
  specific = 4
FEATURE [App::DocumentObjectGroupPython] C_element075  label="C_element : 036"  # scripted group (container) (typed FeaturePython)
  n = 5
  ref = C_element
FEATURE [App::DocumentObjectGroupPython] H_element069  label="H_element : 032"  # scripted group (container) (typed FeaturePython)
  n = 12
  ref = H_element
FEATURE [App::DocumentObjectGroupPython] G4_N_PENTANE  label="G4_N-PENTANE"  # scripted group (container) (typed FeaturePython)
  Dunit = g/cm3
  Dvalue = 0.6262
  Group = -> [C_element075,H_element069]
  conduct = 2
  density = 1
  expand = 3
  formula = G4_N-PENTANE
  name = G4_N-PENTANE
  specific = 4
FEATURE [App::DocumentObjectGroupPython] H_element070  label="H_element : 0.014"  # scripted group (container) (typed FeaturePython)
  n = 0.0141
FEATURE [App::DocumentObjectGroupPython] C_element076  label="C_element : 0.072"  # scripted group (container) (typed FeaturePython)
  n = 0.072261
FEATURE [App::DocumentObjectGroupPython] N_element035  label="N_element : 0.019"  # scripted group (container) (typed FeaturePython)
  n = 0.01932
FEATURE [App::DocumentObjectGroupPython] O_element075  label="O_element : 0.066"  # scripted group (container) (typed FeaturePython)
  n = 0.066101
FEATURE [App::DocumentObjectGroupPython] S_element019  label="S_element : 0.020"  # scripted group (container) (typed FeaturePython)
  n = 0.00189
FEATURE [App::DocumentObjectGroupPython] Br_element004  label="Br_element : 0.349"  # scripted group (container) (typed FeaturePython)
  n = 0.349103
FEATURE [App::DocumentObjectGroupPython] Ag_element001  label="Ag_element : 0.474"  # scripted group (container) (typed FeaturePython)
  n = 0.474105
FEATURE [App::DocumentObjectGroupPython] I_element005  label="I_element : 0.003"  # scripted group (container) (typed FeaturePython)
  n = 0.00312
FEATURE [App::DocumentObjectGroupPython] G4_PHOTO_EMULSION  # scripted group (container) (typed FeaturePython)
  Dunit = g/cm3
  Dvalue = 3.815
  Group = -> [H_element070,C_element076,N_element035,O_element075,S_element019,Br_element004,Ag_element001,I_element005]
  conduct = 2
  density = 1
  expand = 3
  formula = G4_PHOTO_EMULSION
  name = G4_PHOTO_EMULSION
  specific = 4
FEATURE [App::DocumentObjectGroupPython] C_element077  label="C_element : 9"  # scripted group (container) (typed FeaturePython)
  n = 9
  ref = C_element
FEATURE [App::DocumentObjectGroupPython] H_element071  label="H_element : 033"  # scripted group (container) (typed FeaturePython)
  n = 10
  ref = H_element
FEATURE [App::DocumentObjectGroupPython] G4_PLASTIC_SC_VINYLTOLUENE  # scripted group (container) (typed FeaturePython)
  Dunit = g/cm3
  Dvalue = 1.032
  Group = -> [C_element077,H_element071]
  conduct = 2
  density = 1
  expand = 3
  formula = G4_PLASTIC_SC_VINYLTOLUENE
  name = G4_PLASTIC_SC_VINYLTOLUENE
  specific = 4
FEATURE [App::DocumentObjectGroupPython] Pu_element001  label="Pu_element : 1"  # scripted group (container) (typed FeaturePython)
  n = 1
  ref = Pu_element
FEATURE [App::DocumentObjectGroupPython] O_element076  label="O_element : 037"  # scripted group (container) (typed FeaturePython)
  n = 2
  ref = O_element
FEATURE [App::DocumentObjectGroupPython] G4_PLUTONIUM_DIOXIDE  # scripted group (container) (typed FeaturePython)
  Dunit = g/cm3
  Dvalue = 11.46
  Group = -> [Pu_element001,O_element076]
  conduct = 2
  density = 1
  expand = 3
  formula = G4_PLUTONIUM_DIOXIDE
  name = G4_PLUTONIUM_DIOXIDE
  specific = 4
FEATURE [App::DocumentObjectGroupPython] C_element078  label="C_element : 037"  # scripted group (container) (typed FeaturePython)
  n = 3
  ref = C_element
FEATURE [App::DocumentObjectGroupPython] H_element072  label="H_element : 034"  # scripted group (container) (typed FeaturePython)
  n = 3
  ref = H_element
FEATURE [App::DocumentObjectGroupPython] N_element036  label="N_element : 015"  # scripted group (container) (typed FeaturePython)
  n = 1
  ref = N_element
FEATURE [App::DocumentObjectGroupPython] G4_POLYACRYLONITRILE  # scripted group (container) (typed FeaturePython)
  Dunit = g/cm3
  Dvalue = 1.17
  Group = -> [C_element078,H_element072,N_element036]
  conduct = 2
  density = 1
  expand = 3
  formula = G4_POLYACRYLONITRILE
  name = G4_POLYACRYLONITRILE
  specific = 4
FEATURE [App::DocumentObjectGroupPython] C_element079  label="C_element : 16"  # scripted group (container) (typed FeaturePython)
  n = 16
  ref = C_element
FEATURE [App::DocumentObjectGroupPython] H_element073  label="H_element : 035"  # scripted group (container) (typed FeaturePython)
  n = 14
  ref = H_element
FEATURE [App::DocumentObjectGroupPython] O_element077  label="O_element : 038"  # scripted group (container) (typed FeaturePython)
  n = 3
  ref = O_element
FEATURE [App::DocumentObjectGroupPython] G4_POLYCARBONATE  # scripted group (container) (typed FeaturePython)
  Dunit = g/cm3
  Dvalue = 1.2
  Group = -> [C_element079,H_element073,O_element077]
  conduct = 2
  density = 1
  expand = 3
  formula = G4_POLYCARBONATE
  name = G4_POLYCARBONATE
  specific = 4
FEATURE [App::DocumentObjectGroupPython] C_element080  label="C_element : 038"  # scripted group (container) (typed FeaturePython)
  n = 8
  ref = C_element
FEATURE [App::DocumentObjectGroupPython] H_element074  label="H_element : 036"  # scripted group (container) (typed FeaturePython)
  n = 7
  ref = H_element
FEATURE [App::DocumentObjectGroupPython] Cl_element017  label="Cl_element : 007"  # scripted group (container) (typed FeaturePython)
  n = 1
  ref = Cl_element
FEATURE [App::DocumentObjectGroupPython] G4_POLYCHLOROSTYRENE  # scripted group (container) (typed FeaturePython)
  Dunit = g/cm3
  Dvalue = 1.3
  Group = -> [C_element080,H_element074,Cl_element017]
  conduct = 2
  density = 1
  expand = 3
  formula = G4_POLYCHLOROSTYRENE
  name = G4_POLYCHLOROSTYRENE
  specific = 4
FEATURE [App::DocumentObjectGroupPython] C_element081  label="C_element : 039"  # scripted group (container) (typed FeaturePython)
  n = 1
  ref = C_element
FEATURE [App::DocumentObjectGroupPython] H_element075  label="H_element : 037"  # scripted group (container) (typed FeaturePython)
  n = 2
  ref = H_element
FEATURE [App::DocumentObjectGroupPython] G4_POLYETHYLENE  # scripted group (container) (typed FeaturePython)
  Dunit = g/cm3
  Dvalue = 0.94
  Group = -> [C_element081,H_element075]
  conduct = 2
  density = 1
  expand = 3
  formula = G4_POLYETHYLENE
  name = G4_POLYETHYLENE
  specific = 4
FEATURE [App::DocumentObjectGroupPython] C_element082  label="C_element : 040"  # scripted group (container) (typed FeaturePython)
  n = 10
  ref = C_element
FEATURE [App::DocumentObjectGroupPython] H_element076  label="H_element : 038"  # scripted group (container) (typed FeaturePython)
  n = 8
  ref = H_element
FEATURE [App::DocumentObjectGroupPython] O_element078  label="O_element : 039"  # scripted group (container) (typed FeaturePython)
  n = 4
  ref = O_element
FEATURE [App::DocumentObjectGroupPython] G4_MYLAR  # scripted group (container) (typed FeaturePython)
  Dunit = g/cm3
  Dvalue = 1.4
  Group = -> [C_element082,H_element076,O_element078]
  conduct = 2
  density = 1
  expand = 3
  formula = G4_MYLAR
  name = G4_MYLAR
  specific = 4
FEATURE [App::DocumentObjectGroupPython] C_element083  label="C_element : 041"  # scripted group (container) (typed FeaturePython)
  n = 5
  ref = C_element
FEATURE [App::DocumentObjectGroupPython] H_element077  label="H_element : 039"  # scripted group (container) (typed FeaturePython)
  n = 8
  ref = H_element
FEATURE [App::DocumentObjectGroupPython] O_element079  label="O_element : 040"  # scripted group (container) (typed FeaturePython)
  n = 2
  ref = O_element
FEATURE [App::DocumentObjectGroupPython] G4_PLEXIGLASS  # scripted group (container) (typed FeaturePython)
  Dunit = g/cm3
  Dvalue = 1.19
  Group = -> [C_element083,H_element077,O_element079]
  conduct = 2
  density = 1
  expand = 3
  formula = G4_PLEXIGLASS
  name = G4_PLEXIGLASS
  specific = 4
FEATURE [App::DocumentObjectGroupPython] C_element084  label="C_element : 042"  # scripted group (container) (typed FeaturePython)
  n = 1
  ref = C_element
FEATURE [App::DocumentObjectGroupPython] H_element078  label="H_element : 040"  # scripted group (container) (typed FeaturePython)
  n = 2
  ref = H_element
FEATURE [App::DocumentObjectGroupPython] O_element080  label="O_element : 041"  # scripted group (container) (typed FeaturePython)
  n = 1
  ref = O_element
FEATURE [App::DocumentObjectGroupPython] G4_POLYOXYMETHYLENE  # scripted group (container) (typed FeaturePython)
  Dunit = g/cm3
  Dvalue = 1.425
  Group = -> [C_element084,H_element078,O_element080]
  conduct = 2
  density = 1
  expand = 3
  formula = G4_POLYOXYMETHYLENE
  name = G4_POLYOXYMETHYLENE
  specific = 4
FEATURE [App::DocumentObjectGroupPython] C_element085  label="C_element : 043"  # scripted group (container) (typed FeaturePython)
  n = 2
  ref = C_element
FEATURE [App::DocumentObjectGroupPython] H_element079  label="H_element : 041"  # scripted group (container) (typed FeaturePython)
  n = 4
  ref = H_element
FEATURE [App::DocumentObjectGroupPython] G4_POLYPROPYLENE  # scripted group (container) (typed FeaturePython)
  Dunit = g/cm3
  Dvalue = 0.9
  Group = -> [C_element085,H_element079]
  conduct = 2
  density = 1
  expand = 3
  formula = G4_POLYPROPYLENE
  name = G4_POLYPROPYLENE
  specific = 4
FEATURE [App::DocumentObjectGroupPython] C_element086  label="C_element : 044"  # scripted group (container) (typed FeaturePython)
  n = 8
  ref = C_element
FEATURE [App::DocumentObjectGroupPython] H_element080  label="H_element : 042"  # scripted group (container) (typed FeaturePython)
  n = 8
  ref = H_element
FEATURE [App::DocumentObjectGroupPython] G4_POLYSTYRENE  # scripted group (container) (typed FeaturePython)
  Dunit = g/cm3
  Dvalue = 1.06
  Group = -> [C_element086,H_element080]
  conduct = 2
  density = 1
  expand = 3
  formula = G4_POLYSTYRENE
  name = G4_POLYSTYRENE
  specific = 4
FEATURE [App::DocumentObjectGroupPython] C_element087  label="C_element : 045"  # scripted group (container) (typed FeaturePython)
  n = 2
  ref = C_element
FEATURE [App::DocumentObjectGroupPython] F_element014  label="F_element : 4"  # scripted group (container) (typed FeaturePython)
  n = 4
  ref = F_element
FEATURE [App::DocumentObjectGroupPython] G4_TEFLON  # scripted group (container) (typed FeaturePython)
  Dunit = g/cm3
  Dvalue = 2.2
  Group = -> [C_element087,F_element014]
  conduct = 2
  density = 1
  expand = 3
  formula = G4_TEFLON
  name = G4_TEFLON
  specific = 4
FEATURE [App::DocumentObjectGroupPython] C_element088  label="C_element : 046"  # scripted group (container) (typed FeaturePython)
  n = 2
  ref = C_element
FEATURE [App::DocumentObjectGroupPython] F_element015  label="F_element : 006"  # scripted group (container) (typed FeaturePython)
  n = 3
  ref = F_element
FEATURE [App::DocumentObjectGroupPython] Cl_element018  label="Cl_element : 008"  # scripted group (container) (typed FeaturePython)
  n = 1
  ref = Cl_element
FEATURE [App::DocumentObjectGroupPython] G4_POLYTRIFLUOROCHLOROETHYLENE  # scripted group (container) (typed FeaturePython)
  Dunit = g/cm3
  Dvalue = 2.1
  Group = -> [C_element088,F_element015,Cl_element018]
  conduct = 2
  density = 1
  expand = 3
  formula = G4_POLYTRIFLUOROCHLOROETHYLENE
  name = G4_POLYTRIFLUOROCHLOROETHYLENE
  specific = 4
FEATURE [App::DocumentObjectGroupPython] C_element089  label="C_element : 047"  # scripted group (container) (typed FeaturePython)
  n = 4
  ref = C_element
FEATURE [App::DocumentObjectGroupPython] H_element081  label="H_element : 043"  # scripted group (container) (typed FeaturePython)
  n = 6
  ref = H_element
FEATURE [App::DocumentObjectGroupPython] O_element081  label="O_element : 042"  # scripted group (container) (typed FeaturePython)
  n = 2
  ref = O_element
FEATURE [App::DocumentObjectGroupPython] G4_POLYVINYL_ACETATE  # scripted group (container) (typed FeaturePython)
  Dunit = g/cm3
  Dvalue = 1.19
  Group = -> [C_element089,H_element081,O_element081]
  conduct = 2
  density = 1
  expand = 3
  formula = G4_POLYVINYL_ACETATE
  name = G4_POLYVINYL_ACETATE
  specific = 4
FEATURE [App::DocumentObjectGroupPython] C_element090  label="C_element : 048"  # scripted group (container) (typed FeaturePython)
  n = 2
  ref = C_element
FEATURE [App::DocumentObjectGroupPython] H_element082  label="H_element : 044"  # scripted group (container) (typed FeaturePython)
  n = 4
  ref = H_element
FEATURE [App::DocumentObjectGroupPython] O_element082  label="O_element : 043"  # scripted group (container) (typed FeaturePython)
  n = 1
  ref = O_element
FEATURE [App::DocumentObjectGroupPython] G4_POLYVINYL_ALCOHOL  # scripted group (container) (typed FeaturePython)
  Dunit = g/cm3
  Dvalue = 1.3
  Group = -> [C_element090,H_element082,O_element082]
  conduct = 2
  density = 1
  expand = 3
  formula = G4_POLYVINYL_ALCOHOL
  name = G4_POLYVINYL_ALCOHOL
  specific = 4
FEATURE [App::DocumentObjectGroupPython] C_element091  label="C_element : 049"  # scripted group (container) (typed FeaturePython)
  n = 8
  ref = C_element
FEATURE [App::DocumentObjectGroupPython] H_element083  label="H_element : 045"  # scripted group (container) (typed FeaturePython)
  n = 14
  ref = H_element
FEATURE [App::DocumentObjectGroupPython] O_element083  label="O_element : 044"  # scripted group (container) (typed FeaturePython)
  n = 2
  ref = O_element
FEATURE [App::DocumentObjectGroupPython] G4_POLYVINYL_BUTYRAL  # scripted group (container) (typed FeaturePython)
  Dunit = g/cm3
  Dvalue = 1.12
  Group = -> [C_element091,H_element083,O_element083]
  conduct = 2
  density = 1
  expand = 3
  formula = G4_POLYVINYL_BUTYRAL
  name = G4_POLYVINYL_BUTYRAL
  specific = 4
FEATURE [App::DocumentObjectGroupPython] C_element092  label="C_element : 050"  # scripted group (container) (typed FeaturePython)
  n = 2
  ref = C_element
FEATURE [App::DocumentObjectGroupPython] H_element084  label="H_element : 046"  # scripted group (container) (typed FeaturePython)
  n = 3
  ref = H_element
FEATURE [App::DocumentObjectGroupPython] Cl_element019  label="Cl_element : 009"  # scripted group (container) (typed FeaturePython)
  n = 1
  ref = Cl_element
FEATURE [App::DocumentObjectGroupPython] G4_POLYVINYL_CHLORIDE  # scripted group (container) (typed FeaturePython)
  Dunit = g/cm3
  Dvalue = 1.3
  Group = -> [C_element092,H_element084,Cl_element019]
  conduct = 2
  density = 1
  expand = 3
  formula = G4_POLYVINYL_CHLORIDE
  name = G4_POLYVINYL_CHLORIDE
  specific = 4
FEATURE [App::DocumentObjectGroupPython] C_element093  label="C_element : 051"  # scripted group (container) (typed FeaturePython)
  n = 2
  ref = C_element
FEATURE [App::DocumentObjectGroupPython] H_element085  label="H_element : 047"  # scripted group (container) (typed FeaturePython)
  n = 2
  ref = H_element
FEATURE [App::DocumentObjectGroupPython] Cl_element020  label="Cl_element : 010"  # scripted group (container) (typed FeaturePython)
  n = 2
  ref = Cl_element
FEATURE [App::DocumentObjectGroupPython] G4_POLYVINYLIDENE_CHLORIDE  # scripted group (container) (typed FeaturePython)
  Dunit = g/cm3
  Dvalue = 1.7
  Group = -> [C_element093,H_element085,Cl_element020]
  conduct = 2
  density = 1
  expand = 3
  formula = G4_POLYVINYLIDENE_CHLORIDE
  name = G4_POLYVINYLIDENE_CHLORIDE
  specific = 4
FEATURE [App::DocumentObjectGroupPython] C_element094  label="C_element : 052"  # scripted group (container) (typed FeaturePython)
  n = 2
  ref = C_element
FEATURE [App::DocumentObjectGroupPython] H_element086  label="H_element : 048"  # scripted group (container) (typed FeaturePython)
  n = 2
  ref = H_element
FEATURE [App::DocumentObjectGroupPython] F_element016  label="F_element : 007"  # scripted group (container) (typed FeaturePython)
  n = 2
  ref = F_element
FEATURE [App::DocumentObjectGroupPython] G4_POLYVINYLIDENE_FLUORIDE  # scripted group (container) (typed FeaturePython)
  Dunit = g/cm3
  Dvalue = 1.76
  Group = -> [C_element094,H_element086,F_element016]
  conduct = 2
  density = 1
  expand = 3
  formula = G4_POLYVINYLIDENE_FLUORIDE
  name = G4_POLYVINYLIDENE_FLUORIDE
  specific = 4
FEATURE [App::DocumentObjectGroupPython] C_element095  label="C_element : 053"  # scripted group (container) (typed FeaturePython)
  n = 6
  ref = C_element
FEATURE [App::DocumentObjectGroupPython] H_element087  label="H_element : 9"  # scripted group (container) (typed FeaturePython)
  n = 9
  ref = H_element
FEATURE [App::DocumentObjectGroupPython] N_element037  label="N_element : 016"  # scripted group (container) (typed FeaturePython)
  n = 1
  ref = N_element
FEATURE [App::DocumentObjectGroupPython] O_element084  label="O_element : 045"  # scripted group (container) (typed FeaturePython)
  n = 1
  ref = O_element
FEATURE [App::DocumentObjectGroupPython] G4_POLYVINYL_PYRROLIDONE  # scripted group (container) (typed FeaturePython)
  Dunit = g/cm3
  Dvalue = 1.25
  Group = -> [C_element095,H_element087,N_element037,O_element084]
  conduct = 2
  density = 1
  expand = 3
  formula = G4_POLYVINYL_PYRROLIDONE
  name = G4_POLYVINYL_PYRROLIDONE
  specific = 4
FEATURE [App::DocumentObjectGroupPython] K_element008  label="K_element : 1"  # scripted group (container) (typed FeaturePython)
  n = 1
  ref = K_element
FEATURE [App::DocumentObjectGroupPython] I_element006  label="I_element : 003"  # scripted group (container) (typed FeaturePython)
  n = 1
  ref = I_element
FEATURE [App::DocumentObjectGroupPython] G4_POTASSIUM_IODIDE  # scripted group (container) (typed FeaturePython)
  Dunit = g/cm3
  Dvalue = 3.13
  Group = -> [K_element008,I_element006]
  conduct = 2
  density = 1
  expand = 3
  formula = G4_POTASSIUM_IODIDE
  name = G4_POTASSIUM_IODIDE
  specific = 4
FEATURE [App::DocumentObjectGroupPython] K_element009  label="K_element : 2"  # scripted group (container) (typed FeaturePython)
  n = 2
  ref = K_element
FEATURE [App::DocumentObjectGroupPython] O_element085  label="O_element : 046"  # scripted group (container) (typed FeaturePython)
  n = 1
  ref = O_element
FEATURE [App::DocumentObjectGroupPython] G4_POTASSIUM_OXIDE  # scripted group (container) (typed FeaturePython)
  Dunit = g/cm3
  Dvalue = 2.32
  Group = -> [K_element009,O_element085]
  conduct = 2
  density = 1
  expand = 3
  formula = G4_POTASSIUM_OXIDE
  name = G4_POTASSIUM_OXIDE
  specific = 4
FEATURE [App::DocumentObjectGroupPython] C_element096  label="C_element : 054"  # scripted group (container) (typed FeaturePython)
  n = 3
  ref = C_element
FEATURE [App::DocumentObjectGroupPython] H_element088  label="H_element : 049"  # scripted group (container) (typed FeaturePython)
  n = 8
  ref = H_element
FEATURE [App::DocumentObjectGroupPython] G4_PROPANE  # scripted group (container) (typed FeaturePython)
  Dunit = g/cm3
  Dvalue = 0.00187939
  Group = -> [C_element096,H_element088]
  conduct = 2
  density = 1
  expand = 3
  formula = G4_PROPANE
  name = G4_PROPANE
  specific = 4
FEATURE [App::DocumentObjectGroupPython] C_element097  label="C_element : 055"  # scripted group (container) (typed FeaturePython)
  n = 3
  ref = C_element
FEATURE [App::DocumentObjectGroupPython] H_element089  label="H_element : 050"  # scripted group (container) (typed FeaturePython)
  n = 8
  ref = H_element
FEATURE [App::DocumentObjectGroupPython] G4_lPROPANE  # scripted group (container) (typed FeaturePython)
  Dunit = g/cm3
  Dvalue = 0.43
  Group = -> [C_element097,H_element089]
  conduct = 2
  density = 1
  expand = 3
  formula = G4_lPROPANE
  name = G4_lPROPANE
  specific = 4
FEATURE [App::DocumentObjectGroupPython] C_element098  label="C_element : 056"  # scripted group (container) (typed FeaturePython)
  n = 3
  ref = C_element
FEATURE [App::DocumentObjectGroupPython] H_element090  label="H_element : 051"  # scripted group (container) (typed FeaturePython)
  n = 8
  ref = H_element
FEATURE [App::DocumentObjectGroupPython] O_element086  label="O_element : 047"  # scripted group (container) (typed FeaturePython)
  n = 1
  ref = O_element
FEATURE [App::DocumentObjectGroupPython] G4_N_PROPYL_ALCOHOL  label="G4_N-PROPYL_ALCOHOL"  # scripted group (container) (typed FeaturePython)
  Dunit = g/cm3
  Dvalue = 0.8035
  Group = -> [C_element098,H_element090,O_element086]
  conduct = 2
  density = 1
  expand = 3
  formula = G4_N-PROPYL_ALCOHOL
  name = G4_N-PROPYL_ALCOHOL
  specific = 4
FEATURE [App::DocumentObjectGroupPython] C_element099  label="C_element : 057"  # scripted group (container) (typed FeaturePython)
  n = 5
  ref = C_element
FEATURE [App::DocumentObjectGroupPython] H_element091  label="H_element : 052"  # scripted group (container) (typed FeaturePython)
  n = 5
  ref = H_element
FEATURE [App::DocumentObjectGroupPython] N_element038  label="N_element : 017"  # scripted group (container) (typed FeaturePython)
  n = 1
  ref = N_element
FEATURE [App::DocumentObjectGroupPython] G4_PYRIDINE  # scripted group (container) (typed FeaturePython)
  Dunit = g/cm3
  Dvalue = 0.9819
  Group = -> [C_element099,H_element091,N_element038]
  conduct = 2
  density = 1
  expand = 3
  formula = G4_PYRIDINE
  name = G4_PYRIDINE
  specific = 4
FEATURE [App::DocumentObjectGroupPython] H_element092  label="H_element : 0.144"  # scripted group (container) (typed FeaturePython)
  n = 0.143711
FEATURE [App::DocumentObjectGroupPython] C_element100  label="C_element : 0.856"  # scripted group (container) (typed FeaturePython)
  n = 0.856289
FEATURE [App::DocumentObjectGroupPython] G4_RUBBER_BUTYL  # scripted group (container) (typed FeaturePython)
  Dunit = g/cm3
  Dvalue = 0.92
  Group = -> [H_element092,C_element100]
  conduct = 2
  density = 1
  expand = 3
  formula = G4_RUBBER_BUTYL
  name = G4_RUBBER_BUTYL
  specific = 4
FEATURE [App::DocumentObjectGroupPython] H_element093  label="H_element : 0.118"  # scripted group (container) (typed FeaturePython)
  n = 0.118371
FEATURE [App::DocumentObjectGroupPython] C_element101  label="C_element : 0.882"  # scripted group (container) (typed FeaturePython)
  n = 0.881629
FEATURE [App::DocumentObjectGroupPython] G4_RUBBER_NATURAL  # scripted group (container) (typed FeaturePython)
  Dunit = g/cm3
  Dvalue = 0.92
  Group = -> [H_element093,C_element101]
  conduct = 2
  density = 1
  expand = 3
  formula = G4_RUBBER_NATURAL
  name = G4_RUBBER_NATURAL
  specific = 4
FEATURE [App::DocumentObjectGroupPython] H_element094  label="H_element : 0.145"  # scripted group (container) (typed FeaturePython)
  n = 0.05692
FEATURE [App::DocumentObjectGroupPython] C_element102  label="C_element : 0.543"  # scripted group (container) (typed FeaturePython)
  n = 0.542646
FEATURE [App::DocumentObjectGroupPython] Cl_element021  label="Cl_element : 0.400"  # scripted group (container) (typed FeaturePython)
  n = 0.400434
FEATURE [App::DocumentObjectGroupPython] G4_RUBBER_NEOPRENE  # scripted group (container) (typed FeaturePython)
  Dunit = g/cm3
  Dvalue = 1.23
  Group = -> [H_element094,C_element102,Cl_element021]
  conduct = 2
  density = 1
  expand = 3
  formula = G4_RUBBER_NEOPRENE
  name = G4_RUBBER_NEOPRENE
  specific = 4
FEATURE [App::DocumentObjectGroupPython] Si_element006  label="Si_element : 1"  # scripted group (container) (typed FeaturePython)
  n = 1
  ref = Si_element
FEATURE [App::DocumentObjectGroupPython] O_element087  label="O_element : 048"  # scripted group (container) (typed FeaturePython)
  n = 2
  ref = O_element
FEATURE [App::DocumentObjectGroupPython] G4_SILICON_DIOXIDE001  label="G4_SILICON_DIOXIDE"  # scripted group (container) (typed FeaturePython)
  Dunit = g/cm3
  Dvalue = 2.32
  Group = -> [Si_element006,O_element087]
  conduct = 2
  density = 1
  expand = 3
  formula = G4_SILICON_DIOXIDE
  name = G4_SILICON_DIOXIDE
  specific = 4
FEATURE [App::DocumentObjectGroupPython] Ag_element002  label="Ag_element : 1"  # scripted group (container) (typed FeaturePython)
  n = 1
  ref = Ag_element
FEATURE [App::DocumentObjectGroupPython] Br_element005  label="Br_element : 003"  # scripted group (container) (typed FeaturePython)
  n = 1
  ref = Br_element
FEATURE [App::DocumentObjectGroupPython] G4_SILVER_BROMIDE  # scripted group (container) (typed FeaturePython)
  Dunit = g/cm3
  Dvalue = 6.473
  Group = -> [Ag_element002,Br_element005]
  conduct = 2
  density = 1
  expand = 3
  formula = G4_SILVER_BROMIDE
  name = G4_SILVER_BROMIDE
  specific = 4
FEATURE [App::DocumentObjectGroupPython] Ag_element003  label="Ag_element : 002"  # scripted group (container) (typed FeaturePython)
  n = 1
  ref = Ag_element
FEATURE [App::DocumentObjectGroupPython] Cl_element022  label="Cl_element : 011"  # scripted group (container) (typed FeaturePython)
  n = 1
  ref = Cl_element
FEATURE [App::DocumentObjectGroupPython] G4_SILVER_CHLORIDE  # scripted group (container) (typed FeaturePython)
  Dunit = g/cm3
  Dvalue = 5.56
  Group = -> [Ag_element003,Cl_element022]
  conduct = 2
  density = 1
  expand = 3
  formula = G4_SILVER_CHLORIDE
  name = G4_SILVER_CHLORIDE
  specific = 4
FEATURE [App::DocumentObjectGroupPython] Br_element006  label="Br_element : 0.423"  # scripted group (container) (typed FeaturePython)
  n = 0.422895
FEATURE [App::DocumentObjectGroupPython] Ag_element004  label="Ag_element : 0.574"  # scripted group (container) (typed FeaturePython)
  n = 0.573748
FEATURE [App::DocumentObjectGroupPython] I_element007  label="I_element : 0.649"  # scripted group (container) (typed FeaturePython)
  n = 0.003357
FEATURE [App::DocumentObjectGroupPython] G4_SILVER_HALIDES  # scripted group (container) (typed FeaturePython)
  Dunit = g/cm3
  Dvalue = 6.47
  Group = -> [Br_element006,Ag_element004,I_element007]
  conduct = 2
  density = 1
  expand = 3
  formula = G4_SILVER_HALIDES
  name = G4_SILVER_HALIDES
  specific = 4
FEATURE [App::DocumentObjectGroupPython] Ag_element005  label="Ag_element : 003"  # scripted group (container) (typed FeaturePython)
  n = 1
  ref = Ag_element
FEATURE [App::DocumentObjectGroupPython] I_element008  label="I_element : 004"  # scripted group (container) (typed FeaturePython)
  n = 1
  ref = I_element
FEATURE [App::DocumentObjectGroupPython] G4_SILVER_IODIDE  # scripted group (container) (typed FeaturePython)
  Dunit = g/cm3
  Dvalue = 6.01
  Group = -> [Ag_element005,I_element008]
  conduct = 2
  density = 1
  expand = 3
  formula = G4_SILVER_IODIDE
  name = G4_SILVER_IODIDE
  specific = 4
FEATURE [App::DocumentObjectGroupPython] H_element095  label="H_element : 0.100"  # scripted group (container) (typed FeaturePython)
  n = 0.1
FEATURE [App::DocumentObjectGroupPython] C_element103  label="C_element : 0.204"  # scripted group (container) (typed FeaturePython)
  n = 0.204
FEATURE [App::DocumentObjectGroupPython] N_element039  label="N_element : 0.759"  # scripted group (container) (typed FeaturePython)
  n = 0.042
FEATURE [App::DocumentObjectGroupPython] O_element088  label="O_element : 0.645"  # scripted group (container) (typed FeaturePython)
  n = 0.645
FEATURE [App::DocumentObjectGroupPython] Na_element013  label="Na_element : 0.100"  # scripted group (container) (typed FeaturePython)
  n = 0.002
FEATURE [App::DocumentObjectGroupPython] P_element009  label="P_element : 0.107"  # scripted group (container) (typed FeaturePython)
  n = 0.001
FEATURE [App::DocumentObjectGroupPython] S_element020  label="S_element : 0.021"  # scripted group (container) (typed FeaturePython)
  n = 0.002
FEATURE [App::DocumentObjectGroupPython] Cl_element023  label="Cl_element : 0.590"  # scripted group (container) (typed FeaturePython)
  n = 0.003
FEATURE [App::DocumentObjectGroupPython] K_element010  label="K_element : 0.001"  # scripted group (container) (typed FeaturePython)
  n = 0.001
FEATURE [App::DocumentObjectGroupPython] G4_SKIN_ICRP  # scripted group (container) (typed FeaturePython)
  Dunit = g/cm3
  Dvalue = 1.09
  Group = -> [H_element095,C_element103,N_element039,O_element088,Na_element013,P_element009,S_element020,Cl_element023,K_element010]
  conduct = 2
  density = 1
  expand = 3
  formula = G4_SKIN_ICRP
  name = G4_SKIN_ICRP
  specific = 4
FEATURE [App::DocumentObjectGroupPython] Na_element014  label="Na_element : 2"  # scripted group (container) (typed FeaturePython)
  n = 2
  ref = Na_element
FEATURE [App::DocumentObjectGroupPython] C_element104  label="C_element : 058"  # scripted group (container) (typed FeaturePython)
  n = 1
  ref = C_element
FEATURE [App::DocumentObjectGroupPython] O_element089  label="O_element : 049"  # scripted group (container) (typed FeaturePython)
  n = 3
  ref = O_element
FEATURE [App::DocumentObjectGroupPython] G4_SODIUM_CARBONATE  # scripted group (container) (typed FeaturePython)
  Dunit = g/cm3
  Dvalue = 2.532
  Group = -> [Na_element014,C_element104,O_element089]
  conduct = 2
  density = 1
  expand = 3
  formula = G4_SODIUM_CARBONATE
  name = G4_SODIUM_CARBONATE
  specific = 4
FEATURE [App::DocumentObjectGroupPython] Na_element015  label="Na_element : 1"  # scripted group (container) (typed FeaturePython)
  n = 1
  ref = Na_element
FEATURE [App::DocumentObjectGroupPython] I_element009  label="I_element : 005"  # scripted group (container) (typed FeaturePython)
  n = 1
  ref = I_element
FEATURE [App::DocumentObjectGroupPython] G4_SODIUM_IODIDE  # scripted group (container) (typed FeaturePython)
  Dunit = g/cm3
  Dvalue = 3.667
  Group = -> [Na_element015,I_element009]
  conduct = 2
  density = 1
  expand = 3
  formula = G4_SODIUM_IODIDE
  name = G4_SODIUM_IODIDE
  specific = 4
FEATURE [App::DocumentObjectGroupPython] Na_element016  label="Na_element : 003"  # scripted group (container) (typed FeaturePython)
  n = 2
  ref = Na_element
FEATURE [App::DocumentObjectGroupPython] O_element090  label="O_element : 050"  # scripted group (container) (typed FeaturePython)
  n = 1
  ref = O_element
FEATURE [App::DocumentObjectGroupPython] G4_SODIUM_MONOXIDE  # scripted group (container) (typed FeaturePython)
  Dunit = g/cm3
  Dvalue = 2.27
  Group = -> [Na_element016,O_element090]
  conduct = 2
  density = 1
  expand = 3
  formula = G4_SODIUM_MONOXIDE
  name = G4_SODIUM_MONOXIDE
  specific = 4
FEATURE [App::DocumentObjectGroupPython] Na_element017  label="Na_element : 004"  # scripted group (container) (typed FeaturePython)
  n = 1
  ref = Na_element
FEATURE [App::DocumentObjectGroupPython] N_element040  label="N_element : 018"  # scripted group (container) (typed FeaturePython)
  n = 1
  ref = N_element
FEATURE [App::DocumentObjectGroupPython] O_element091  label="O_element : 051"  # scripted group (container) (typed FeaturePython)
  n = 3
  ref = O_element
FEATURE [App::DocumentObjectGroupPython] G4_SODIUM_NITRATE  # scripted group (container) (typed FeaturePython)
  Dunit = g/cm3
  Dvalue = 2.261
  Group = -> [Na_element017,N_element040,O_element091]
  conduct = 2
  density = 1
  expand = 3
  formula = G4_SODIUM_NITRATE
  name = G4_SODIUM_NITRATE
  specific = 4
FEATURE [App::DocumentObjectGroupPython] C_element105  label="C_element : 059"  # scripted group (container) (typed FeaturePython)
  n = 14
  ref = C_element
FEATURE [App::DocumentObjectGroupPython] H_element096  label="H_element : 053"  # scripted group (container) (typed FeaturePython)
  n = 12
  ref = H_element
FEATURE [App::DocumentObjectGroupPython] G4_STILBENE  # scripted group (container) (typed FeaturePython)
  Dunit = g/cm3
  Dvalue = 0.9707
  Group = -> [C_element105,H_element096]
  conduct = 2
  density = 1
  expand = 3
  formula = G4_STILBENE
  name = G4_STILBENE
  specific = 4
FEATURE [App::DocumentObjectGroupPython] C_element106  label="C_element : 12"  # scripted group (container) (typed FeaturePython)
  n = 12
  ref = C_element
FEATURE [App::DocumentObjectGroupPython] H_element097  label="H_element : 22"  # scripted group (container) (typed FeaturePython)
  n = 22
  ref = H_element
FEATURE [App::DocumentObjectGroupPython] O_element092  label="O_element : 11"  # scripted group (container) (typed FeaturePython)
  n = 11
  ref = O_element
FEATURE [App::DocumentObjectGroupPython] G4_SUCROSE  # scripted group (container) (typed FeaturePython)
  Dunit = g/cm3
  Dvalue = 1.5805
  Group = -> [C_element106,H_element097,O_element092]
  conduct = 2
  density = 1
  expand = 3
  formula = G4_SUCROSE
  name = G4_SUCROSE
  specific = 4
FEATURE [App::DocumentObjectGroupPython] C_element107  label="C_element : 18"  # scripted group (container) (typed FeaturePython)
  n = 18
  ref = C_element
FEATURE [App::DocumentObjectGroupPython] H_element098  label="H_element : 054"  # scripted group (container) (typed FeaturePython)
  n = 14
  ref = H_element
FEATURE [App::DocumentObjectGroupPython] G4_TERPHENYL  # scripted group (container) (typed FeaturePython)
  Dunit = g/cm3
  Dvalue = 1.24
  Group = -> [C_element107,H_element098]
  conduct = 2
  density = 1
  expand = 3
  formula = G4_TERPHENYL
  name = G4_TERPHENYL
  specific = 4
FEATURE [App::DocumentObjectGroupPython] H_element099  label="H_element : 0.146"  # scripted group (container) (typed FeaturePython)
  n = 0.106
FEATURE [App::DocumentObjectGroupPython] C_element108  label="C_element : 0.883"  # scripted group (container) (typed FeaturePython)
  n = 0.099
FEATURE [App::DocumentObjectGroupPython] N_element041  label="N_element : 0.020"  # scripted group (container) (typed FeaturePython)
  n = 0.02
FEATURE [App::DocumentObjectGroupPython] O_element093  label="O_element : 0.766"  # scripted group (container) (typed FeaturePython)
  n = 0.766
FEATURE [App::DocumentObjectGroupPython] Na_element018  label="Na_element : 0.101"  # scripted group (container) (typed FeaturePython)
  n = 0.002
FEATURE [App::DocumentObjectGroupPython] P_element010  label="P_element : 0.108"  # scripted group (container) (typed FeaturePython)
  n = 0.001
FEATURE [App::DocumentObjectGroupPython] S_element021  label="S_element : 0.022"  # scripted group (container) (typed FeaturePython)
  n = 0.002
FEATURE [App::DocumentObjectGroupPython] Cl_element024  label="Cl_element : 0.002"  # scripted group (container) (typed FeaturePython)
  n = 0.002
FEATURE [App::DocumentObjectGroupPython] K_element011  label="K_element : 0.017"  # scripted group (container) (typed FeaturePython)
  n = 0.002
FEATURE [App::DocumentObjectGroupPython] G4_TESTIS_ICRP  # scripted group (container) (typed FeaturePython)
  Dunit = g/cm3
  Dvalue = 1.04
  Group = -> [H_element099,C_element108,N_element041,O_element093,Na_element018,P_element010,S_element021,Cl_element024,K_element011]
  conduct = 2
  density = 1
  expand = 3
  formula = G4_TESTIS_ICRP
  name = G4_TESTIS_ICRP
  specific = 4
FEATURE [App::DocumentObjectGroupPython] C_element109  label="C_element : 060"  # scripted group (container) (typed FeaturePython)
  n = 2
  ref = C_element
FEATURE [App::DocumentObjectGroupPython] Cl_element025  label="Cl_element : 012"  # scripted group (container) (typed FeaturePython)
  n = 4
  ref = Cl_element
FEATURE [App::DocumentObjectGroupPython] G4_TETRACHLOROETHYLENE  # scripted group (container) (typed FeaturePython)
  Dunit = g/cm3
  Dvalue = 1.625
  Group = -> [C_element109,Cl_element025]
  conduct = 2
  density = 1
  expand = 3
  formula = G4_TETRACHLOROETHYLENE
  name = G4_TETRACHLOROETHYLENE
  specific = 4
FEATURE [App::DocumentObjectGroupPython] Tl_element001  label="Tl_element : 1"  # scripted group (container) (typed FeaturePython)
  n = 1
  ref = Tl_element
FEATURE [App::DocumentObjectGroupPython] Cl_element026  label="Cl_element : 013"  # scripted group (container) (typed FeaturePython)
  n = 1
  ref = Cl_element
FEATURE [App::DocumentObjectGroupPython] G4_THALLIUM_CHLORIDE  # scripted group (container) (typed FeaturePython)
  Dunit = g/cm3
  Dvalue = 7.004
  Group = -> [Tl_element001,Cl_element026]
  conduct = 2
  density = 1
  expand = 3
  formula = G4_THALLIUM_CHLORIDE
  name = G4_THALLIUM_CHLORIDE
  specific = 4
FEATURE [App::DocumentObjectGroupPython] H_element100  label="H_element : 0.147"  # scripted group (container) (typed FeaturePython)
  n = 0.105
FEATURE [App::DocumentObjectGroupPython] C_element110  label="C_element : 0.256"  # scripted group (container) (typed FeaturePython)
  n = 0.256
FEATURE [App::DocumentObjectGroupPython] N_element042  label="N_element : 0.760"  # scripted group (container) (typed FeaturePython)
  n = 0.027
FEATURE [App::DocumentObjectGroupPython] O_element094  label="O_element : 0.602"  # scripted group (container) (typed FeaturePython)
  n = 0.602
FEATURE [App::DocumentObjectGroupPython] Na_element019  label="Na_element : 0.102"  # scripted group (container) (typed FeaturePython)
  n = 0.001
FEATURE [App::DocumentObjectGroupPython] P_element011  label="P_element : 0.109"  # scripted group (container) (typed FeaturePython)
  n = 0.002
FEATURE [App::DocumentObjectGroupPython] S_element022  label="S_element : 0.023"  # scripted group (container) (typed FeaturePython)
  n = 0.003
FEATURE [App::DocumentObjectGroupPython] Cl_element027  label="Cl_element : 0.591"  # scripted group (container) (typed FeaturePython)
  n = 0.002
FEATURE [App::DocumentObjectGroupPython] K_element012  label="K_element : 0.018"  # scripted group (container) (typed FeaturePython)
  n = 0.002
FEATURE [App::DocumentObjectGroupPython] G4_TISSUE_SOFT_ICRP  # scripted group (container) (typed FeaturePython)
  Dunit = g/cm3
  Dvalue = 1.03
  Group = -> [H_element100,C_element110,N_element042,O_element094,Na_element019,P_element011,S_element022,Cl_element027,K_element012]
  conduct = 2
  density = 1
  expand = 3
  formula = G4_TISSUE_SOFT_ICRP
  name = G4_TISSUE_SOFT_ICRP
  specific = 4
FEATURE [App::DocumentObjectGroupPython] H_element101  label="H_element : 0.148"  # scripted group (container) (typed FeaturePython)
  n = 0.101
FEATURE [App::DocumentObjectGroupPython] C_element111  label="C_element : 0.111"  # scripted group (container) (typed FeaturePython)
  n = 0.111
FEATURE [App::DocumentObjectGroupPython] N_element043  label="N_element : 0.026"  # scripted group (container) (typed FeaturePython)
  n = 0.026
FEATURE [App::DocumentObjectGroupPython] O_element095  label="O_element : 0.762"  # scripted group (container) (typed FeaturePython)
  n = 0.762
FEATURE [App::DocumentObjectGroupPython] G4_TISSUE_SOFT_ICRU_4  label="G4_TISSUE_SOFT_ICRU-4"  # scripted group (container) (typed FeaturePython)
  Dunit = g/cm3
  Dvalue = 1
  Group = -> [H_element101,C_element111,N_element043,O_element095]
  conduct = 2
  density = 1
  expand = 3
  formula = G4_TISSUE_SOFT_ICRU-4
  name = G4_TISSUE_SOFT_ICRU-4
  specific = 4
FEATURE [App::DocumentObjectGroupPython] H_element102  label="H_element : 0.149"  # scripted group (container) (typed FeaturePython)
  n = 0.101869
FEATURE [App::DocumentObjectGroupPython] C_element112  label="C_element : 0.456"  # scripted group (container) (typed FeaturePython)
  n = 0.456179
FEATURE [App::DocumentObjectGroupPython] N_element044  label="N_element : 0.761"  # scripted group (container) (typed FeaturePython)
  n = 0.035172
FEATURE [App::DocumentObjectGroupPython] O_element096  label="O_element : 0.407"  # scripted group (container) (typed FeaturePython)
  n = 0.40678
FEATURE [App::DocumentObjectGroupPython] G4_TISSUE_METHANE  label="G4_TISSUE-METHANE"  # scripted group (container) (typed FeaturePython)
  Dunit = g/cm3
  Dvalue = 0.00106409
  Group = -> [H_element102,C_element112,N_element044,O_element096]
  conduct = 2
  density = 1
  expand = 3
  formula = G4_TISSUE-METHANE
  name = G4_TISSUE-METHANE
  specific = 4
FEATURE [App::DocumentObjectGroupPython] H_element103  label="H_element : 0.103"  # scripted group (container) (typed FeaturePython)
  n = 0.102672
FEATURE [App::DocumentObjectGroupPython] C_element113  label="C_element : 0.569"  # scripted group (container) (typed FeaturePython)
  n = 0.56894
FEATURE [App::DocumentObjectGroupPython] N_element045  label="N_element : 0.762"  # scripted group (container) (typed FeaturePython)
  n = 0.035022
FEATURE [App::DocumentObjectGroupPython] O_element097  label="O_element : 0.293"  # scripted group (container) (typed FeaturePython)
  n = 0.293366
FEATURE [App::DocumentObjectGroupPython] G4_TISSUE_PROPANE  label="G4_TISSUE-PROPANE"  # scripted group (container) (typed FeaturePython)
  Dunit = g/cm3
  Dvalue = 0.00182628
  Group = -> [H_element103,C_element113,N_element045,O_element097]
  conduct = 2
  density = 1
  expand = 3
  formula = G4_TISSUE-PROPANE
  name = G4_TISSUE-PROPANE
  specific = 4
FEATURE [App::DocumentObjectGroupPython] Ti_element003  label="Ti_element : 1"  # scripted group (container) (typed FeaturePython)
  n = 1
  ref = Ti_element
FEATURE [App::DocumentObjectGroupPython] O_element098  label="O_element : 052"  # scripted group (container) (typed FeaturePython)
  n = 2
  ref = O_element
FEATURE [App::DocumentObjectGroupPython] G4_TITANIUM_DIOXIDE  # scripted group (container) (typed FeaturePython)
  Dunit = g/cm3
  Dvalue = 4.26
  Group = -> [Ti_element003,O_element098]
  conduct = 2
  density = 1
  expand = 3
  formula = G4_TITANIUM_DIOXIDE
  name = G4_TITANIUM_DIOXIDE
  specific = 4
FEATURE [App::DocumentObjectGroupPython] C_element114  label="C_element : 061"  # scripted group (container) (typed FeaturePython)
  n = 7
  ref = C_element
FEATURE [App::DocumentObjectGroupPython] H_element104  label="H_element : 055"  # scripted group (container) (typed FeaturePython)
  n = 8
  ref = H_element
FEATURE [App::DocumentObjectGroupPython] G4_TOLUENE  # scripted group (container) (typed FeaturePython)
  Dunit = g/cm3
  Dvalue = 0.8669
  Group = -> [C_element114,H_element104]
  conduct = 2
  density = 1
  expand = 3
  formula = G4_TOLUENE
  name = G4_TOLUENE
  specific = 4
FEATURE [App::DocumentObjectGroupPython] C_element115  label="C_element : 062"  # scripted group (container) (typed FeaturePython)
  n = 2
  ref = C_element
FEATURE [App::DocumentObjectGroupPython] H_element105  label="H_element : 056"  # scripted group (container) (typed FeaturePython)
  n = 1
  ref = H_element
FEATURE [App::DocumentObjectGroupPython] Cl_element028  label="Cl_element : 014"  # scripted group (container) (typed FeaturePython)
  n = 3
  ref = Cl_element
FEATURE [App::DocumentObjectGroupPython] G4_TRICHLOROETHYLENE  # scripted group (container) (typed FeaturePython)
  Dunit = g/cm3
  Dvalue = 1.46
  Group = -> [C_element115,H_element105,Cl_element028]
  conduct = 2
  density = 1
  expand = 3
  formula = G4_TRICHLOROETHYLENE
  name = G4_TRICHLOROETHYLENE
  specific = 4
FEATURE [App::DocumentObjectGroupPython] C_element116  label="C_element : 063"  # scripted group (container) (typed FeaturePython)
  n = 6
  ref = C_element
FEATURE [App::DocumentObjectGroupPython] H_element106  label="H_element : 15"  # scripted group (container) (typed FeaturePython)
  n = 15
  ref = H_element
FEATURE [App::DocumentObjectGroupPython] O_element099  label="O_element : 053"  # scripted group (container) (typed FeaturePython)
  n = 4
  ref = O_element
FEATURE [App::DocumentObjectGroupPython] P_element012  label="P_element : 1"  # scripted group (container) (typed FeaturePython)
  n = 1
  ref = P_element
FEATURE [App::DocumentObjectGroupPython] G4_TRIETHYL_PHOSPHATE  # scripted group (container) (typed FeaturePython)
  Dunit = g/cm3
  Dvalue = 1.07
  Group = -> [C_element116,H_element106,O_element099,P_element012]
  conduct = 2
  density = 1
  expand = 3
  formula = G4_TRIETHYL_PHOSPHATE
  name = G4_TRIETHYL_PHOSPHATE
  specific = 4
FEATURE [App::DocumentObjectGroupPython] W_element003  label="W_element : 003"  # scripted group (container) (typed FeaturePython)
  n = 1
  ref = W_element
FEATURE [App::DocumentObjectGroupPython] F_element017  label="F_element : 6"  # scripted group (container) (typed FeaturePython)
  n = 6
  ref = F_element
FEATURE [App::DocumentObjectGroupPython] G4_TUNGSTEN_HEXAFLUORIDE  # scripted group (container) (typed FeaturePython)
  Dunit = g/cm3
  Dvalue = 2.4
  Group = -> [W_element003,F_element017]
  conduct = 2
  density = 1
  expand = 3
  formula = G4_TUNGSTEN_HEXAFLUORIDE
  name = G4_TUNGSTEN_HEXAFLUORIDE
  specific = 4
FEATURE [App::DocumentObjectGroupPython] U_element001  label="U_element : 1"  # scripted group (container) (typed FeaturePython)
  n = 1
  ref = U_element
FEATURE [App::DocumentObjectGroupPython] C_element117  label="C_element : 064"  # scripted group (container) (typed FeaturePython)
  n = 2
  ref = C_element
FEATURE [App::DocumentObjectGroupPython] G4_URANIUM_DICARBIDE  # scripted group (container) (typed FeaturePython)
  Dunit = g/cm3
  Dvalue = 11.28
  Group = -> [U_element001,C_element117]
  conduct = 2
  density = 1
  expand = 3
  formula = G4_URANIUM_DICARBIDE
  name = G4_URANIUM_DICARBIDE
  specific = 4
FEATURE [App::DocumentObjectGroupPython] U_element002  label="U_element : 002"  # scripted group (container) (typed FeaturePython)
  n = 1
  ref = U_element
FEATURE [App::DocumentObjectGroupPython] C_element118  label="C_element : 065"  # scripted group (container) (typed FeaturePython)
  n = 1
  ref = C_element
FEATURE [App::DocumentObjectGroupPython] G4_URANIUM_MONOCARBIDE  # scripted group (container) (typed FeaturePython)
  Dunit = g/cm3
  Dvalue = 13.63
  Group = -> [U_element002,C_element118]
  conduct = 2
  density = 1
  expand = 3
  formula = G4_URANIUM_MONOCARBIDE
  name = G4_URANIUM_MONOCARBIDE
  specific = 4
FEATURE [App::DocumentObjectGroupPython] U_element003  label="U_element : 003"  # scripted group (container) (typed FeaturePython)
  n = 1
  ref = U_element
FEATURE [App::DocumentObjectGroupPython] O_element100  label="O_element : 054"  # scripted group (container) (typed FeaturePython)
  n = 2
  ref = O_element
FEATURE [App::DocumentObjectGroupPython] G4_URANIUM_OXIDE  # scripted group (container) (typed FeaturePython)
  Dunit = g/cm3
  Dvalue = 10.96
  Group = -> [U_element003,O_element100]
  conduct = 2
  density = 1
  expand = 3
  formula = G4_URANIUM_OXIDE
  name = G4_URANIUM_OXIDE
  specific = 4
FEATURE [App::DocumentObjectGroupPython] C_element119  label="C_element : 066"  # scripted group (container) (typed FeaturePython)
  n = 1
  ref = C_element
FEATURE [App::DocumentObjectGroupPython] H_element107  label="H_element : 057"  # scripted group (container) (typed FeaturePython)
  n = 4
  ref = H_element
FEATURE [App::DocumentObjectGroupPython] N_element046  label="N_element : 019"  # scripted group (container) (typed FeaturePython)
  n = 2
  ref = N_element
FEATURE [App::DocumentObjectGroupPython] O_element101  label="O_element : 055"  # scripted group (container) (typed FeaturePython)
  n = 1
  ref = O_element
FEATURE [App::DocumentObjectGroupPython] G4_UREA  # scripted group (container) (typed FeaturePython)
  Dunit = g/cm3
  Dvalue = 1.323
  Group = -> [C_element119,H_element107,N_element046,O_element101]
  conduct = 2
  density = 1
  expand = 3
  formula = G4_UREA
  name = G4_UREA
  specific = 4
FEATURE [App::DocumentObjectGroupPython] C_element120  label="C_element : 067"  # scripted group (container) (typed FeaturePython)
  n = 5
  ref = C_element
FEATURE [App::DocumentObjectGroupPython] H_element108  label="H_element : 058"  # scripted group (container) (typed FeaturePython)
  n = 11
  ref = H_element
FEATURE [App::DocumentObjectGroupPython] N_element047  label="N_element : 020"  # scripted group (container) (typed FeaturePython)
  n = 1
  ref = N_element
FEATURE [App::DocumentObjectGroupPython] O_element102  label="O_element : 056"  # scripted group (container) (typed FeaturePython)
  n = 2
  ref = O_element
FEATURE [App::DocumentObjectGroupPython] G4_VALINE  # scripted group (container) (typed FeaturePython)
  Dunit = g/cm3
  Dvalue = 1.23
  Group = -> [C_element120,H_element108,N_element047,O_element102]
  conduct = 2
  density = 1
  expand = 3
  formula = G4_VALINE
  name = G4_VALINE
  specific = 4
FEATURE [App::DocumentObjectGroupPython] H_element109  label="H_element : 0.009"  # scripted group (container) (typed FeaturePython)
  n = 0.009417
FEATURE [App::DocumentObjectGroupPython] C_element121  label="C_element : 0.281"  # scripted group (container) (typed FeaturePython)
  n = 0.280555
FEATURE [App::DocumentObjectGroupPython] F_element018  label="F_element : 0.710"  # scripted group (container) (typed FeaturePython)
  n = 0.710028
FEATURE [App::DocumentObjectGroupPython] G4_VITON  # scripted group (container) (typed FeaturePython)
  Dunit = g/cm3
  Dvalue = 1.8
  Group = -> [H_element109,C_element121,F_element018]
  conduct = 2
  density = 1
  expand = 3
  formula = G4_VITON
  name = G4_VITON
  specific = 4
FEATURE [App::DocumentObjectGroupPython] H_element110  label="H_element : 059"  # scripted group (container) (typed FeaturePython)
  n = 2
  ref = H_element
FEATURE [App::DocumentObjectGroupPython] O_element103  label="O_element : 057"  # scripted group (container) (typed FeaturePython)
  n = 1
  ref = O_element
FEATURE [App::DocumentObjectGroupPython] G4_WATER  # scripted group (container) (typed FeaturePython)
  Dunit = g/cm3
  Dvalue = 1
  Group = -> [H_element110,O_element103]
  conduct = 2
  density = 1
  expand = 3
  formula = G4_WATER
  name = G4_WATER
  specific = 4
FEATURE [App::DocumentObjectGroupPython] H_element111  label="H_element : 060"  # scripted group (container) (typed FeaturePython)
  n = 2
  ref = H_element
FEATURE [App::DocumentObjectGroupPython] O_element104  label="O_element : 058"  # scripted group (container) (typed FeaturePython)
  n = 1
  ref = O_element
FEATURE [App::DocumentObjectGroupPython] G4_WATER_VAPOR  # scripted group (container) (typed FeaturePython)
  Dunit = g/cm3
  Dvalue = 0.000756182
  Group = -> [H_element111,O_element104]
  conduct = 2
  density = 1
  expand = 3
  formula = G4_WATER_VAPOR
  name = G4_WATER_VAPOR
  specific = 4
FEATURE [App::DocumentObjectGroupPython] C_element122  label="C_element : 068"  # scripted group (container) (typed FeaturePython)
  n = 8
  ref = C_element
FEATURE [App::DocumentObjectGroupPython] H_element112  label="H_element : 061"  # scripted group (container) (typed FeaturePython)
  n = 10
  ref = H_element
FEATURE [App::DocumentObjectGroupPython] G4_XYLENE  # scripted group (container) (typed FeaturePython)
  Dunit = g/cm3
  Dvalue = 0.87
  Group = -> [C_element122,H_element112]
  conduct = 2
  density = 1
  expand = 3
  formula = G4_XYLENE
  name = G4_XYLENE
  specific = 4
FEATURE [App::DocumentObjectGroupPython] C_element123  label="C_element : 069"  # scripted group (container) (typed FeaturePython)
  n = 1
  ref = C_element
FEATURE [App::DocumentObjectGroupPython] G4_GRAPHITE  # scripted group (container) (typed FeaturePython)
  Dunit = g/cm3
  Dvalue = 2.21
  Group = -> [C_element123]
  conduct = 2
  density = 1
  expand = 3
  formula = G4_GRAPHITE
  name = G4_GRAPHITE
  specific = 4
FEATURE [App::DocumentObjectGroupPython] NIST  # scripted group (container) (typed FeaturePython)
  Group = -> [G4_A_150_TISSUE,G4_ACETONE,G4_ACETYLENE,G4_ADENINE,G4_ADIPOSE_TISSUE_ICRP,G4_AIR001,G4_ALANINE,G4_ALUMINUM_OXIDE,G4_AMBER,G4_AMMONIA,G4_ANILINE,G4_ANTHRACENE,G4_B_100_BONE,G4_BAKELITE,G4_BARIUM_FLUORIDE,G4_BARIUM_SULFATE,G4_BENZENE,G4_BERYLLIUM_OXIDE,G4_BGO,G4_BLOOD_ICRP,G4_BONE_COMPACT_ICRU,G4_BONE_CORTICAL_ICRP,G4_BORON_CARBIDE,G4_BORON_OXIDE,G4_BRAIN_ICRP,G4_BUTANE,G4_N_BUTYL_ALCOHOL,G4_C_552,+152 more]
FEATURE [App::DocumentObjectGroupPython] H_element113  label="H_element : 062"  # scripted group (container) (typed FeaturePython)
  n = 1
  ref = H_element
FEATURE [App::DocumentObjectGroupPython] G4_H  # scripted group (container) (typed FeaturePython)
  Dunit = g/cm3
  Dvalue = 8.3748e-05
  Group = -> [H_element113]
  conduct = 2
  density = 1
  expand = 3
  formula = H
  name = G4_H
  specific = 4
FEATURE [App::DocumentObjectGroupPython] He_element001  label="He_element : 1"  # scripted group (container) (typed FeaturePython)
  n = 1
  ref = He_element
FEATURE [App::DocumentObjectGroupPython] G4_He  # scripted group (container) (typed FeaturePython)
  Dunit = g/cm3
  Dvalue = 0.000166322
  Group = -> [He_element001]
  conduct = 2
  density = 1
  expand = 3
  formula = He
  name = G4_He
  specific = 4
FEATURE [App::DocumentObjectGroupPython] Li_element008  label="Li_element : 008"  # scripted group (container) (typed FeaturePython)
  n = 1
  ref = Li_element
FEATURE [App::DocumentObjectGroupPython] G4_Li  # scripted group (container) (typed FeaturePython)
  Dunit = g/cm3
  Dvalue = 0.534
  Group = -> [Li_element008]
  conduct = 2
  density = 1
  expand = 3
  formula = Li
  name = G4_Li
  specific = 4
FEATURE [App::DocumentObjectGroupPython] Be_element002  label="Be_element : 002"  # scripted group (container) (typed FeaturePython)
  n = 1
  ref = Be_element
FEATURE [App::DocumentObjectGroupPython] G4_Be  # scripted group (container) (typed FeaturePython)
  Dunit = g/cm3
  Dvalue = 1.848
  Group = -> [Be_element002]
  conduct = 2
  density = 1
  expand = 3
  formula = Be
  name = G4_Be
  specific = 4
FEATURE [App::DocumentObjectGroupPython] B_element007  label="B_element : 007"  # scripted group (container) (typed FeaturePython)
  n = 1
  ref = B_element
FEATURE [App::DocumentObjectGroupPython] G4_B  # scripted group (container) (typed FeaturePython)
  Dunit = g/cm3
  Dvalue = 2.37
  Group = -> [B_element007]
  conduct = 2
  density = 1
  expand = 3
  formula = B
  name = G4_B
  specific = 4
FEATURE [App::DocumentObjectGroupPython] C_element124  label="C_element : 070"  # scripted group (container) (typed FeaturePython)
  n = 1
  ref = C_element
FEATURE [App::DocumentObjectGroupPython] G4_C  # scripted group (container) (typed FeaturePython)
  Dunit = g/cm3
  Dvalue = 2
  Group = -> [C_element124]
  conduct = 2
  density = 1
  expand = 3
  formula = C
  name = G4_C
  specific = 4
FEATURE [App::DocumentObjectGroupPython] N_element048  label="N_element : 021"  # scripted group (container) (typed FeaturePython)
  n = 1
  ref = N_element
FEATURE [App::DocumentObjectGroupPython] G4_N  # scripted group (container) (typed FeaturePython)
  Dunit = g/cm3
  Dvalue = 0.0011652
  Group = -> [N_element048]
  conduct = 2
  density = 1
  expand = 3
  formula = N
  name = G4_N
  specific = 4
FEATURE [App::DocumentObjectGroupPython] O_element105  label="O_element : 059"  # scripted group (container) (typed FeaturePython)
  n = 1
  ref = O_element
FEATURE [App::DocumentObjectGroupPython] G4_O  # scripted group (container) (typed FeaturePython)
  Dunit = g/cm3
  Dvalue = 0.00133151
  Group = -> [O_element105]
  conduct = 2
  density = 1
  expand = 3
  formula = O
  name = G4_O
  specific = 4
FEATURE [App::DocumentObjectGroupPython] F_element019  label="F_element : 008"  # scripted group (container) (typed FeaturePython)
  n = 1
  ref = F_element
FEATURE [App::DocumentObjectGroupPython] G4_F  # scripted group (container) (typed FeaturePython)
  Dunit = g/cm3
  Dvalue = 0.00158029
  Group = -> [F_element019]
  conduct = 2
  density = 1
  expand = 3
  formula = F
  name = G4_F
  specific = 4
FEATURE [App::DocumentObjectGroupPython] Ne_element001  label="Ne_element : 1"  # scripted group (container) (typed FeaturePython)
  n = 1
  ref = Ne_element
FEATURE [App::DocumentObjectGroupPython] G4_Ne  # scripted group (container) (typed FeaturePython)
  Dunit = g/cm3
  Dvalue = 0.000838505
  Group = -> [Ne_element001]
  conduct = 2
  density = 1
  expand = 3
  formula = Ne
  name = G4_Ne
  specific = 4
FEATURE [App::DocumentObjectGroupPython] Na_element020  label="Na_element : 005"  # scripted group (container) (typed FeaturePython)
  n = 1
  ref = Na_element
FEATURE [App::DocumentObjectGroupPython] G4_Na  # scripted group (container) (typed FeaturePython)
  Dunit = g/cm3
  Dvalue = 0.971
  Group = -> [Na_element020]
  conduct = 2
  density = 1
  expand = 3
  formula = Na
  name = G4_Na
  specific = 4
FEATURE [App::DocumentObjectGroupPython] Mg_element011  label="Mg_element : 005"  # scripted group (container) (typed FeaturePython)
  n = 1
  ref = Mg_element
FEATURE [App::DocumentObjectGroupPython] G4_Mg  # scripted group (container) (typed FeaturePython)
  Dunit = g/cm3
  Dvalue = 1.74
  Group = -> [Mg_element011]
  conduct = 2
  density = 1
  expand = 3
  formula = Mg
  name = G4_Mg
  specific = 4
FEATURE [App::DocumentObjectGroupPython] Al_element004  label="Al_element : 1"  # scripted group (container) (typed FeaturePython)
  n = 1
  ref = Al_element
FEATURE [App::DocumentObjectGroupPython] G4_Al  # scripted group (container) (typed FeaturePython)
  Dunit = g/cm3
  Dvalue = 2.699
  Group = -> [Al_element004]
  conduct = 2
  density = 1
  expand = 3
  formula = Al
  name = G4_Al
  specific = 4
FEATURE [App::DocumentObjectGroupPython] Si_element007  label="Si_element : 002"  # scripted group (container) (typed FeaturePython)
  n = 1
  ref = Si_element
FEATURE [App::DocumentObjectGroupPython] G4_Si  # scripted group (container) (typed FeaturePython)
  Dunit = g/cm3
  Dvalue = 2.33
  Group = -> [Si_element007]
  conduct = 2
  density = 1
  expand = 3
  formula = Si
  name = G4_Si
  specific = 4
FEATURE [App::DocumentObjectGroupPython] P_element013  label="P_element : 002"  # scripted group (container) (typed FeaturePython)
  n = 1
  ref = P_element
FEATURE [App::DocumentObjectGroupPython] G4_P  # scripted group (container) (typed FeaturePython)
  Dunit = g/cm3
  Dvalue = 2.2
  Group = -> [P_element013]
  conduct = 2
  density = 1
  expand = 3
  formula = P
  name = G4_P
  specific = 4
FEATURE [App::DocumentObjectGroupPython] S_element023  label="S_element : 007"  # scripted group (container) (typed FeaturePython)
  n = 1
  ref = S_element
FEATURE [App::DocumentObjectGroupPython] G4_S  # scripted group (container) (typed FeaturePython)
  Dunit = g/cm3
  Dvalue = 2
  Group = -> [S_element023]
  conduct = 2
  density = 1
  expand = 3
  formula = S
  name = G4_S
  specific = 4
FEATURE [App::DocumentObjectGroupPython] Cl_element029  label="Cl_element : 015"  # scripted group (container) (typed FeaturePython)
  n = 1
  ref = Cl_element
FEATURE [App::DocumentObjectGroupPython] G4_Cl  # scripted group (container) (typed FeaturePython)
  Dunit = g/cm3
  Dvalue = 0.00299473
  Group = -> [Cl_element029]
  conduct = 2
  density = 1
  expand = 3
  formula = Cl
  name = G4_Cl
  specific = 4
FEATURE [App::DocumentObjectGroupPython] Ar_element002  label="Ar_element : 1"  # scripted group (container) (typed FeaturePython)
  n = 1
  ref = Ar_element
FEATURE [App::DocumentObjectGroupPython] G4_Ar  # scripted group (container) (typed FeaturePython)
  Dunit = g/cm3
  Dvalue = 0.00166201
  Group = -> [Ar_element002]
  conduct = 2
  density = 1
  expand = 3
  formula = Ar
  name = G4_Ar
  specific = 4
FEATURE [App::DocumentObjectGroupPython] K_element013  label="K_element : 003"  # scripted group (container) (typed FeaturePython)
  n = 1
  ref = K_element
FEATURE [App::DocumentObjectGroupPython] G4_K  # scripted group (container) (typed FeaturePython)
  Dunit = g/cm3
  Dvalue = 0.862
  Group = -> [K_element013]
  conduct = 2
  density = 1
  expand = 3
  formula = K
  name = G4_K
  specific = 4
FEATURE [App::DocumentObjectGroupPython] Ca_element014  label="Ca_element : 007"  # scripted group (container) (typed FeaturePython)
  n = 1
  ref = Ca_element
FEATURE [App::DocumentObjectGroupPython] G4_Ca  # scripted group (container) (typed FeaturePython)
  Dunit = g/cm3
  Dvalue = 1.55
  Group = -> [Ca_element014]
  conduct = 2
  density = 1
  expand = 3
  formula = Ca
  name = G4_Ca
  specific = 4
FEATURE [App::DocumentObjectGroupPython] Sc_element001  label="Sc_element : 1"  # scripted group (container) (typed FeaturePython)
  n = 1
  ref = Sc_element
FEATURE [App::DocumentObjectGroupPython] G4_Sc  # scripted group (container) (typed FeaturePython)
  Dunit = g/cm3
  Dvalue = 2.989
  Group = -> [Sc_element001]
  conduct = 2
  density = 1
  expand = 3
  formula = Sc
  name = G4_Sc
  specific = 4
FEATURE [App::DocumentObjectGroupPython] Ti_element004  label="Ti_element : 002"  # scripted group (container) (typed FeaturePython)
  n = 1
  ref = Ti_element
FEATURE [App::DocumentObjectGroupPython] G4_Ti  # scripted group (container) (typed FeaturePython)
  Dunit = g/cm3
  Dvalue = 4.54
  Group = -> [Ti_element004]
  conduct = 2
  density = 1
  expand = 3
  formula = Ti
  name = G4_Ti
  specific = 4
FEATURE [App::DocumentObjectGroupPython] V_element001  label="V_element : 1"  # scripted group (container) (typed FeaturePython)
  n = 1
  ref = V_element
FEATURE [App::DocumentObjectGroupPython] G4_V  # scripted group (container) (typed FeaturePython)
  Dunit = g/cm3
  Dvalue = 6.11
  Group = -> [V_element001]
  conduct = 2
  density = 1
  expand = 3
  formula = V
  name = G4_V
  specific = 4
FEATURE [App::DocumentObjectGroupPython] Cr_element001  label="Cr_element : 1"  # scripted group (container) (typed FeaturePython)
  n = 1
  ref = Cr_element
FEATURE [App::DocumentObjectGroupPython] G4_Cr  # scripted group (container) (typed FeaturePython)
  Dunit = g/cm3
  Dvalue = 7.18
  Group = -> [Cr_element001]
  conduct = 2
  density = 1
  expand = 3
  formula = Cr
  name = G4_Cr
  specific = 4
FEATURE [App::DocumentObjectGroupPython] Mn_element001  label="Mn_element : 1"  # scripted group (container) (typed FeaturePython)
  n = 1
  ref = Mn_element
FEATURE [App::DocumentObjectGroupPython] G4_Mn  # scripted group (container) (typed FeaturePython)
  Dunit = g/cm3
  Dvalue = 7.44
  Group = -> [Mn_element001]
  conduct = 2
  density = 1
  expand = 3
  formula = Mn
  name = G4_Mn
  specific = 4
FEATURE [App::DocumentObjectGroupPython] Fe_element007  label="Fe_element : 004"  # scripted group (container) (typed FeaturePython)
  n = 1
  ref = Fe_element
FEATURE [App::DocumentObjectGroupPython] G4_Fe  # scripted group (container) (typed FeaturePython)
  Dunit = g/cm3
  Dvalue = 7.874
  Group = -> [Fe_element007]
  conduct = 2
  density = 1
  expand = 3
  formula = Fe
  name = G4_Fe
  specific = 4
FEATURE [App::DocumentObjectGroupPython] Co_element001  label="Co_element : 1"  # scripted group (container) (typed FeaturePython)
  n = 1
  ref = Co_element
FEATURE [App::DocumentObjectGroupPython] G4_Co  # scripted group (container) (typed FeaturePython)
  Dunit = g/cm3
  Dvalue = 8.9
  Group = -> [Co_element001]
  conduct = 2
  density = 1
  expand = 3
  formula = Co
  name = G4_Co
  specific = 4
FEATURE [App::DocumentObjectGroupPython] Ni_element001  label="Ni_element : 1"  # scripted group (container) (typed FeaturePython)
  n = 1
  ref = Ni_element
FEATURE [App::DocumentObjectGroupPython] G4_Ni  # scripted group (container) (typed FeaturePython)
  Dunit = g/cm3
  Dvalue = 8.902
  Group = -> [Ni_element001]
  conduct = 2
  density = 1
  expand = 3
  formula = Ni
  name = G4_Ni
  specific = 4
FEATURE [App::DocumentObjectGroupPython] Cu_element001  label="Cu_element : 1"  # scripted group (container) (typed FeaturePython)
  n = 1
  ref = Cu_element
FEATURE [App::DocumentObjectGroupPython] G4_Cu  # scripted group (container) (typed FeaturePython)
  Dunit = g/cm3
  Dvalue = 8.96
  Group = -> [Cu_element001]
  conduct = 2
  density = 1
  expand = 3
  formula = Cu
  name = G4_Cu
  specific = 4
FEATURE [App::DocumentObjectGroupPython] Zn_element001  label="Zn_element : 1"  # scripted group (container) (typed FeaturePython)
  n = 1
  ref = Zn_element
FEATURE [App::DocumentObjectGroupPython] G4_Zn  # scripted group (container) (typed FeaturePython)
  Dunit = g/cm3
  Dvalue = 7.133
  Group = -> [Zn_element001]
  conduct = 2
  density = 1
  expand = 3
  formula = Zn
  name = G4_Zn
  specific = 4
FEATURE [App::DocumentObjectGroupPython] Ga_element002  label="Ga_element : 002"  # scripted group (container) (typed FeaturePython)
  n = 1
  ref = Ga_element
FEATURE [App::DocumentObjectGroupPython] G4_Ga  # scripted group (container) (typed FeaturePython)
  Dunit = g/cm3
  Dvalue = 5.904
  Group = -> [Ga_element002]
  conduct = 2
  density = 1
  expand = 3
  formula = Ga
  name = G4_Ga
  specific = 4
FEATURE [App::DocumentObjectGroupPython] Ge_element002  label="Ge_element : 1"  # scripted group (container) (typed FeaturePython)
  n = 1
  ref = Ge_element
FEATURE [App::DocumentObjectGroupPython] G4_Ge  # scripted group (container) (typed FeaturePython)
  Dunit = g/cm3
  Dvalue = 5.323
  Group = -> [Ge_element002]
  conduct = 2
  density = 1
  expand = 3
  formula = Ge
  name = G4_Ge
  specific = 4
FEATURE [App::DocumentObjectGroupPython] As_element003  label="As_element : 002"  # scripted group (container) (typed FeaturePython)
  n = 1
  ref = As_element
FEATURE [App::DocumentObjectGroupPython] G4_As  # scripted group (container) (typed FeaturePython)
  Dunit = g/cm3
  Dvalue = 5.73
  Group = -> [As_element003]
  conduct = 2
  density = 1
  expand = 3
  formula = As
  name = G4_As
  specific = 4
FEATURE [App::DocumentObjectGroupPython] Se_element001  label="Se_element : 1"  # scripted group (container) (typed FeaturePython)
  n = 1
  ref = Se_element
FEATURE [App::DocumentObjectGroupPython] G4_Se  # scripted group (container) (typed FeaturePython)
  Dunit = g/cm3
  Dvalue = 4.5
  Group = -> [Se_element001]
  conduct = 2
  density = 1
  expand = 3
  formula = Se
  name = G4_Se
  specific = 4
FEATURE [App::DocumentObjectGroupPython] Br_element007  label="Br_element : 004"  # scripted group (container) (typed FeaturePython)
  n = 1
  ref = Br_element
FEATURE [App::DocumentObjectGroupPython] G4_Br  # scripted group (container) (typed FeaturePython)
  Dunit = g/cm3
  Dvalue = 0.0070721
  Group = -> [Br_element007]
  conduct = 2
  density = 1
  expand = 3
  formula = Br
  name = G4_Br
  specific = 4
FEATURE [App::DocumentObjectGroupPython] Kr_element001  label="Kr_element : 1"  # scripted group (container) (typed FeaturePython)
  n = 1
  ref = Kr_element
FEATURE [App::DocumentObjectGroupPython] G4_Kr  # scripted group (container) (typed FeaturePython)
  Dunit = g/cm3
  Dvalue = 0.00347832
  Group = -> [Kr_element001]
  conduct = 2
  density = 1
  expand = 3
  formula = Kr
  name = G4_Kr
  specific = 4
FEATURE [App::DocumentObjectGroupPython] Rb_element001  label="Rb_element : 1"  # scripted group (container) (typed FeaturePython)
  n = 1
  ref = Rb_element
FEATURE [App::DocumentObjectGroupPython] G4_Rb  # scripted group (container) (typed FeaturePython)
  Dunit = g/cm3
  Dvalue = 1.532
  Group = -> [Rb_element001]
  conduct = 2
  density = 1
  expand = 3
  formula = Rb
  name = G4_Rb
  specific = 4
FEATURE [App::DocumentObjectGroupPython] Sr_element001  label="Sr_element : 1"  # scripted group (container) (typed FeaturePython)
  n = 1
  ref = Sr_element
FEATURE [App::DocumentObjectGroupPython] G4_Sr  # scripted group (container) (typed FeaturePython)
  Dunit = g/cm3
  Dvalue = 2.54
  Group = -> [Sr_element001]
  conduct = 2
  density = 1
  expand = 3
  formula = Sr
  name = G4_Sr
  specific = 4
FEATURE [App::DocumentObjectGroupPython] Y_element001  label="Y_element : 1"  # scripted group (container) (typed FeaturePython)
  n = 1
  ref = Y_element
FEATURE [App::DocumentObjectGroupPython] G4_Y  # scripted group (container) (typed FeaturePython)
  Dunit = g/cm3
  Dvalue = 4.469
  Group = -> [Y_element001]
  conduct = 2
  density = 1
  expand = 3
  formula = Y
  name = G4_Y
  specific = 4
FEATURE [App::DocumentObjectGroupPython] Zr_element001  label="Zr_element : 1"  # scripted group (container) (typed FeaturePython)
  n = 1
  ref = Zr_element
FEATURE [App::DocumentObjectGroupPython] G4_Zr  # scripted group (container) (typed FeaturePython)
  Dunit = g/cm3
  Dvalue = 6.506
  Group = -> [Zr_element001]
  conduct = 2
  density = 1
  expand = 3
  formula = Zr
  name = G4_Zr
  specific = 4
FEATURE [App::DocumentObjectGroupPython] Nb_element001  label="Nb_element : 1"  # scripted group (container) (typed FeaturePython)
  n = 1
  ref = Nb_element
FEATURE [App::DocumentObjectGroupPython] G4_Nb  # scripted group (container) (typed FeaturePython)
  Dunit = g/cm3
  Dvalue = 8.57
  Group = -> [Nb_element001]
  conduct = 2
  density = 1
  expand = 3
  formula = Nb
  name = G4_Nb
  specific = 4
FEATURE [App::DocumentObjectGroupPython] Mo_element001  label="Mo_element : 1"  # scripted group (container) (typed FeaturePython)
  n = 1
  ref = Mo_element
FEATURE [App::DocumentObjectGroupPython] G4_Mo  # scripted group (container) (typed FeaturePython)
  Dunit = g/cm3
  Dvalue = 10.22
  Group = -> [Mo_element001]
  conduct = 2
  density = 1
  expand = 3
  formula = Mo
  name = G4_Mo
  specific = 4
FEATURE [App::DocumentObjectGroupPython] Tc_element001  label="Tc_element : 1"  # scripted group (container) (typed FeaturePython)
  n = 1
  ref = Tc_element
FEATURE [App::DocumentObjectGroupPython] G4_Tc  # scripted group (container) (typed FeaturePython)
  Dunit = g/cm3
  Dvalue = 11.5
  Group = -> [Tc_element001]
  conduct = 2
  density = 1
  expand = 3
  formula = Tc
  name = G4_Tc
  specific = 4
FEATURE [App::DocumentObjectGroupPython] Ru_element001  label="Ru_element : 1"  # scripted group (container) (typed FeaturePython)
  n = 1
  ref = Ru_element
FEATURE [App::DocumentObjectGroupPython] G4_Ru  # scripted group (container) (typed FeaturePython)
  Dunit = g/cm3
  Dvalue = 12.41
  Group = -> [Ru_element001]
  conduct = 2
  density = 1
  expand = 3
  formula = Ru
  name = G4_Ru
  specific = 4
FEATURE [App::DocumentObjectGroupPython] Rh_element001  label="Rh_element : 1"  # scripted group (container) (typed FeaturePython)
  n = 1
  ref = Rh_element
FEATURE [App::DocumentObjectGroupPython] G4_Rh  # scripted group (container) (typed FeaturePython)
  Dunit = g/cm3
  Dvalue = 12.41
  Group = -> [Rh_element001]
  conduct = 2
  density = 1
  expand = 3
  formula = Rh
  name = G4_Rh
  specific = 4
FEATURE [App::DocumentObjectGroupPython] Pd_element001  label="Pd_element : 1"  # scripted group (container) (typed FeaturePython)
  n = 1
  ref = Pd_element
FEATURE [App::DocumentObjectGroupPython] G4_Pd  # scripted group (container) (typed FeaturePython)
  Dunit = g/cm3
  Dvalue = 12.02
  Group = -> [Pd_element001]
  conduct = 2
  density = 1
  expand = 3
  formula = Pd
  name = G4_Pd
  specific = 4
FEATURE [App::DocumentObjectGroupPython] Ag_element006  label="Ag_element : 004"  # scripted group (container) (typed FeaturePython)
  n = 1
  ref = Ag_element
FEATURE [App::DocumentObjectGroupPython] G4_Ag  # scripted group (container) (typed FeaturePython)
  Dunit = g/cm3
  Dvalue = 10.5
  Group = -> [Ag_element006]
  conduct = 2
  density = 1
  expand = 3
  formula = Ag
  name = G4_Ag
  specific = 4
FEATURE [App::DocumentObjectGroupPython] Cd_element003  label="Cd_element : 003"  # scripted group (container) (typed FeaturePython)
  n = 1
  ref = Cd_element
FEATURE [App::DocumentObjectGroupPython] G4_Cd  # scripted group (container) (typed FeaturePython)
  Dunit = g/cm3
  Dvalue = 8.65
  Group = -> [Cd_element003]
  conduct = 2
  density = 1
  expand = 3
  formula = Cd
  name = G4_Cd
  specific = 4
FEATURE [App::DocumentObjectGroupPython] In_element001  label="In_element : 1"  # scripted group (container) (typed FeaturePython)
  n = 1
  ref = In_element
FEATURE [App::DocumentObjectGroupPython] G4_In  # scripted group (container) (typed FeaturePython)
  Dunit = g/cm3
  Dvalue = 7.31
  Group = -> [In_element001]
  conduct = 2
  density = 1
  expand = 3
  formula = In
  name = G4_In
  specific = 4
FEATURE [App::DocumentObjectGroupPython] Sn_element001  label="Sn_element : 1"  # scripted group (container) (typed FeaturePython)
  n = 1
  ref = Sn_element
FEATURE [App::DocumentObjectGroupPython] G4_Sn  # scripted group (container) (typed FeaturePython)
  Dunit = g/cm3
  Dvalue = 7.31
  Group = -> [Sn_element001]
  conduct = 2
  density = 1
  expand = 3
  formula = Sn
  name = G4_Sn
  specific = 4
FEATURE [App::DocumentObjectGroupPython] Sb_element001  label="Sb_element : 1"  # scripted group (container) (typed FeaturePython)
  n = 1
  ref = Sb_element
FEATURE [App::DocumentObjectGroupPython] G4_Sb  # scripted group (container) (typed FeaturePython)
  Dunit = g/cm3
  Dvalue = 6.691
  Group = -> [Sb_element001]
  conduct = 2
  density = 1
  expand = 3
  formula = Sb
  name = G4_Sb
  specific = 4
FEATURE [App::DocumentObjectGroupPython] Te_element002  label="Te_element : 002"  # scripted group (container) (typed FeaturePython)
  n = 1
  ref = Te_element
FEATURE [App::DocumentObjectGroupPython] G4_Te  # scripted group (container) (typed FeaturePython)
  Dunit = g/cm3
  Dvalue = 6.24
  Group = -> [Te_element002]
  conduct = 2
  density = 1
  expand = 3
  formula = Te
  name = G4_Te
  specific = 4
FEATURE [App::DocumentObjectGroupPython] I_element010  label="I_element : 006"  # scripted group (container) (typed FeaturePython)
  n = 1
  ref = I_element
FEATURE [App::DocumentObjectGroupPython] G4_I  # scripted group (container) (typed FeaturePython)
  Dunit = g/cm3
  Dvalue = 4.93
  Group = -> [I_element010]
  conduct = 2
  density = 1
  expand = 3
  formula = I
  name = G4_I
  specific = 4
FEATURE [App::DocumentObjectGroupPython] Xe_element001  label="Xe_element : 1"  # scripted group (container) (typed FeaturePython)
  n = 1
  ref = Xe_element
FEATURE [App::DocumentObjectGroupPython] G4_Xe  # scripted group (container) (typed FeaturePython)
  Dunit = g/cm3
  Dvalue = 0.00548536
  Group = -> [Xe_element001]
  conduct = 2
  density = 1
  expand = 3
  formula = Xe
  name = G4_Xe
  specific = 4
FEATURE [App::DocumentObjectGroupPython] Cs_element003  label="Cs_element : 003"  # scripted group (container) (typed FeaturePython)
  n = 1
  ref = Cs_element
FEATURE [App::DocumentObjectGroupPython] G4_Cs  # scripted group (container) (typed FeaturePython)
  Dunit = g/cm3
  Dvalue = 1.873
  Group = -> [Cs_element003]
  conduct = 2
  density = 1
  expand = 3
  formula = Cs
  name = G4_Cs
  specific = 4
FEATURE [App::DocumentObjectGroupPython] Ba_element003  label="Ba_element : 003"  # scripted group (container) (typed FeaturePython)
  n = 1
  ref = Ba_element
FEATURE [App::DocumentObjectGroupPython] G4_Ba  # scripted group (container) (typed FeaturePython)
  Dunit = g/cm3
  Dvalue = 3.5
  Group = -> [Ba_element003]
  conduct = 2
  density = 1
  expand = 3
  formula = Ba
  name = G4_Ba
  specific = 4
FEATURE [App::DocumentObjectGroupPython] La_element003  label="La_element : 003"  # scripted group (container) (typed FeaturePython)
  n = 1
  ref = La_element
FEATURE [App::DocumentObjectGroupPython] G4_La  # scripted group (container) (typed FeaturePython)
  Dunit = g/cm3
  Dvalue = 6.154
  Group = -> [La_element003]
  conduct = 2
  density = 1
  expand = 3
  formula = La
  name = G4_La
  specific = 4
FEATURE [App::DocumentObjectGroupPython] Ce_element002  label="Ce_element : 1"  # scripted group (container) (typed FeaturePython)
  n = 1
  ref = Ce_element
FEATURE [App::DocumentObjectGroupPython] G4_Ce  # scripted group (container) (typed FeaturePython)
  Dunit = g/cm3
  Dvalue = 6.657
  Group = -> [Ce_element002]
  conduct = 2
  density = 1
  expand = 3
  formula = Ce
  name = G4_Ce
  specific = 4
FEATURE [App::DocumentObjectGroupPython] Pr_element001  label="Pr_element : 1"  # scripted group (container) (typed FeaturePython)
  n = 1
  ref = Pr_element
FEATURE [App::DocumentObjectGroupPython] G4_Pr  # scripted group (container) (typed FeaturePython)
  Dunit = g/cm3
  Dvalue = 6.71
  Group = -> [Pr_element001]
  conduct = 2
  density = 1
  expand = 3
  formula = Pr
  name = G4_Pr
  specific = 4
FEATURE [App::DocumentObjectGroupPython] Nd_element001  label="Nd_element : 1"  # scripted group (container) (typed FeaturePython)
  n = 1
  ref = Nd_element
FEATURE [App::DocumentObjectGroupPython] G4_Nd  # scripted group (container) (typed FeaturePython)
  Dunit = g/cm3
  Dvalue = 6.9
  Group = -> [Nd_element001]
  conduct = 2
  density = 1
  expand = 3
  formula = Nd
  name = G4_Nd
  specific = 4
FEATURE [App::DocumentObjectGroupPython] Pm_element001  label="Pm_element : 1"  # scripted group (container) (typed FeaturePython)
  n = 1
  ref = Pm_element
FEATURE [App::DocumentObjectGroupPython] G4_Pm  # scripted group (container) (typed FeaturePython)
  Dunit = g/cm3
  Dvalue = 7.22
  Group = -> [Pm_element001]
  conduct = 2
  density = 1
  expand = 3
  formula = Pm
  name = G4_Pm
  specific = 4
FEATURE [App::DocumentObjectGroupPython] Sm_element001  label="Sm_element : 1"  # scripted group (container) (typed FeaturePython)
  n = 1
  ref = Sm_element
FEATURE [App::DocumentObjectGroupPython] G4_Sm  # scripted group (container) (typed FeaturePython)
  Dunit = g/cm3
  Dvalue = 7.46
  Group = -> [Sm_element001]
  conduct = 2
  density = 1
  expand = 3
  formula = Sm
  name = G4_Sm
  specific = 4
FEATURE [App::DocumentObjectGroupPython] Eu_element001  label="Eu_element : 1"  # scripted group (container) (typed FeaturePython)
  n = 1
  ref = Eu_element
FEATURE [App::DocumentObjectGroupPython] G4_Eu  # scripted group (container) (typed FeaturePython)
  Dunit = g/cm3
  Dvalue = 5.243
  Group = -> [Eu_element001]
  conduct = 2
  density = 1
  expand = 3
  formula = Eu
  name = G4_Eu
  specific = 4
FEATURE [App::DocumentObjectGroupPython] Gd_element002  label="Gd_element : 1"  # scripted group (container) (typed FeaturePython)
  n = 1
  ref = Gd_element
FEATURE [App::DocumentObjectGroupPython] G4_Gd  # scripted group (container) (typed FeaturePython)
  Dunit = g/cm3
  Dvalue = 7.9004
  Group = -> [Gd_element002]
  conduct = 2
  density = 1
  expand = 3
  formula = Gd
  name = G4_Gd
  specific = 4
FEATURE [App::DocumentObjectGroupPython] Tb_element001  label="Tb_element : 1"  # scripted group (container) (typed FeaturePython)
  n = 1
  ref = Tb_element
FEATURE [App::DocumentObjectGroupPython] G4_Tb  # scripted group (container) (typed FeaturePython)
  Dunit = g/cm3
  Dvalue = 8.229
  Group = -> [Tb_element001]
  conduct = 2
  density = 1
  expand = 3
  formula = Tb
  name = G4_Tb
  specific = 4
FEATURE [App::DocumentObjectGroupPython] Dy_element001  label="Dy_element : 1"  # scripted group (container) (typed FeaturePython)
  n = 1
  ref = Dy_element
FEATURE [App::DocumentObjectGroupPython] G4_Dy  # scripted group (container) (typed FeaturePython)
  Dunit = g/cm3
  Dvalue = 8.55
  Group = -> [Dy_element001]
  conduct = 2
  density = 1
  expand = 3
  formula = Dy
  name = G4_Dy
  specific = 4
FEATURE [App::DocumentObjectGroupPython] Ho_element001  label="Ho_element : 1"  # scripted group (container) (typed FeaturePython)
  n = 1
  ref = Ho_element
FEATURE [App::DocumentObjectGroupPython] G4_Ho  # scripted group (container) (typed FeaturePython)
  Dunit = g/cm3
  Dvalue = 8.795
  Group = -> [Ho_element001]
  conduct = 2
  density = 1
  expand = 3
  formula = Ho
  name = G4_Ho
  specific = 4
FEATURE [App::DocumentObjectGroupPython] Er_element001  label="Er_element : 1"  # scripted group (container) (typed FeaturePython)
  n = 1
  ref = Er_element
FEATURE [App::DocumentObjectGroupPython] G4_Er  # scripted group (container) (typed FeaturePython)
  Dunit = g/cm3
  Dvalue = 9.066
  Group = -> [Er_element001]
  conduct = 2
  density = 1
  expand = 3
  formula = Er
  name = G4_Er
  specific = 4
FEATURE [App::DocumentObjectGroupPython] Tm_element001  label="Tm_element : 1"  # scripted group (container) (typed FeaturePython)
  n = 1
  ref = Tm_element
FEATURE [App::DocumentObjectGroupPython] G4_Tm  # scripted group (container) (typed FeaturePython)
  Dunit = g/cm3
  Dvalue = 9.321
  Group = -> [Tm_element001]
  conduct = 2
  density = 1
  expand = 3
  formula = Tm
  name = G4_Tm
  specific = 4
FEATURE [App::DocumentObjectGroupPython] Yb_element001  label="Yb_element : 1"  # scripted group (container) (typed FeaturePython)
  n = 1
  ref = Yb_element
FEATURE [App::DocumentObjectGroupPython] G4_Yb  # scripted group (container) (typed FeaturePython)
  Dunit = g/cm3
  Dvalue = 6.73
  Group = -> [Yb_element001]
  conduct = 2
  density = 1
  expand = 3
  formula = Yb
  name = G4_Yb
  specific = 4
FEATURE [App::DocumentObjectGroupPython] Lu_element001  label="Lu_element : 1"  # scripted group (container) (typed FeaturePython)
  n = 1
  ref = Lu_element
FEATURE [App::DocumentObjectGroupPython] G4_Lu  # scripted group (container) (typed FeaturePython)
  Dunit = g/cm3
  Dvalue = 9.84
  Group = -> [Lu_element001]
  conduct = 2
  density = 1
  expand = 3
  formula = Lu
  name = G4_Lu
  specific = 4
FEATURE [App::DocumentObjectGroupPython] Hf_element001  label="Hf_element : 1"  # scripted group (container) (typed FeaturePython)
  n = 1
  ref = Hf_element
FEATURE [App::DocumentObjectGroupPython] G4_Hf  # scripted group (container) (typed FeaturePython)
  Dunit = g/cm3
  Dvalue = 13.31
  Group = -> [Hf_element001]
  conduct = 2
  density = 1
  expand = 3
  formula = Hf
  name = G4_Hf
  specific = 4
FEATURE [App::DocumentObjectGroupPython] Ta_element001  label="Ta_element : 1"  # scripted group (container) (typed FeaturePython)
  n = 1
  ref = Ta_element
FEATURE [App::DocumentObjectGroupPython] G4_Ta  # scripted group (container) (typed FeaturePython)
  Dunit = g/cm3
  Dvalue = 16.654
  Group = -> [Ta_element001]
  conduct = 2
  density = 1
  expand = 3
  formula = Ta
  name = G4_Ta
  specific = 4
FEATURE [App::DocumentObjectGroupPython] W_element004  label="W_element : 004"  # scripted group (container) (typed FeaturePython)
  n = 1
  ref = W_element
FEATURE [App::DocumentObjectGroupPython] G4_W  # scripted group (container) (typed FeaturePython)
  Dunit = g/cm3
  Dvalue = 19.3
  Group = -> [W_element004]
  conduct = 2
  density = 1
  expand = 3
  formula = W
  name = G4_W
  specific = 4
FEATURE [App::DocumentObjectGroupPython] Re_element001  label="Re_element : 1"  # scripted group (container) (typed FeaturePython)
  n = 1
  ref = Re_element
FEATURE [App::DocumentObjectGroupPython] G4_Re  # scripted group (container) (typed FeaturePython)
  Dunit = g/cm3
  Dvalue = 21.02
  Group = -> [Re_element001]
  conduct = 2
  density = 1
  expand = 3
  formula = Re
  name = G4_Re
  specific = 4
FEATURE [App::DocumentObjectGroupPython] Os_element001  label="Os_element : 1"  # scripted group (container) (typed FeaturePython)
  n = 1
  ref = Os_element
FEATURE [App::DocumentObjectGroupPython] G4_Os  # scripted group (container) (typed FeaturePython)
  Dunit = g/cm3
  Dvalue = 22.57
  Group = -> [Os_element001]
  conduct = 2
  density = 1
  expand = 3
  formula = Os
  name = G4_Os
  specific = 4
FEATURE [App::DocumentObjectGroupPython] Ir_element001  label="Ir_element : 1"  # scripted group (container) (typed FeaturePython)
  n = 1
  ref = Ir_element
FEATURE [App::DocumentObjectGroupPython] G4_Ir  # scripted group (container) (typed FeaturePython)
  Dunit = g/cm3
  Dvalue = 22.42
  Group = -> [Ir_element001]
  conduct = 2
  density = 1
  expand = 3
  formula = Ir
  name = G4_Ir
  specific = 4
FEATURE [App::DocumentObjectGroupPython] Pt_element001  label="Pt_element : 1"  # scripted group (container) (typed FeaturePython)
  n = 1
  ref = Pt_element
FEATURE [App::DocumentObjectGroupPython] G4_Pt  # scripted group (container) (typed FeaturePython)
  Dunit = g/cm3
  Dvalue = 21.45
  Group = -> [Pt_element001]
  conduct = 2
  density = 1
  expand = 3
  formula = Pt
  name = G4_Pt
  specific = 4
FEATURE [App::DocumentObjectGroupPython] Au_element001  label="Au_element : 1"  # scripted group (container) (typed FeaturePython)
  n = 1
  ref = Au_element
FEATURE [App::DocumentObjectGroupPython] G4_Au  # scripted group (container) (typed FeaturePython)
  Dunit = g/cm3
  Dvalue = 19.32
  Group = -> [Au_element001]
  conduct = 2
  density = 1
  expand = 3
  formula = Au
  name = G4_Au
  specific = 4
FEATURE [App::DocumentObjectGroupPython] Hg_element002  label="Hg_element : 002"  # scripted group (container) (typed FeaturePython)
  n = 1
  ref = Hg_element
FEATURE [App::DocumentObjectGroupPython] G4_Hg  # scripted group (container) (typed FeaturePython)
  Dunit = g/cm3
  Dvalue = 13.546
  Group = -> [Hg_element002]
  conduct = 2
  density = 1
  expand = 3
  formula = Hg
  name = G4_Hg
  specific = 4
FEATURE [App::DocumentObjectGroupPython] Tl_element002  label="Tl_element : 002"  # scripted group (container) (typed FeaturePython)
  n = 1
  ref = Tl_element
FEATURE [App::DocumentObjectGroupPython] G4_Tl  # scripted group (container) (typed FeaturePython)
  Dunit = g/cm3
  Dvalue = 11.72
  Group = -> [Tl_element002]
  conduct = 2
  density = 1
  expand = 3
  formula = Tl
  name = G4_Tl
  specific = 4
FEATURE [App::DocumentObjectGroupPython] Pb_element003  label="Pb_element : 1"  # scripted group (container) (typed FeaturePython)
  n = 1
  ref = Pb_element
FEATURE [App::DocumentObjectGroupPython] G4_Pb  # scripted group (container) (typed FeaturePython)
  Dunit = g/cm3
  Dvalue = 11.35
  Group = -> [Pb_element003]
  conduct = 2
  density = 1
  expand = 3
  formula = Pb
  name = G4_Pb
  specific = 4
FEATURE [App::DocumentObjectGroupPython] Bi_element002  label="Bi_element : 1"  # scripted group (container) (typed FeaturePython)
  n = 1
  ref = Bi_element
FEATURE [App::DocumentObjectGroupPython] G4_Bi  # scripted group (container) (typed FeaturePython)
  Dunit = g/cm3
  Dvalue = 9.747
  Group = -> [Bi_element002]
  conduct = 2
  density = 1
  expand = 3
  formula = Bi
  name = G4_Bi
  specific = 4
FEATURE [App::DocumentObjectGroupPython] Po_element001  label="Po_element : 1"  # scripted group (container) (typed FeaturePython)
  n = 1
  ref = Po_element
FEATURE [App::DocumentObjectGroupPython] G4_Po  # scripted group (container) (typed FeaturePython)
  Dunit = g/cm3
  Dvalue = 9.32
  Group = -> [Po_element001]
  conduct = 2
  density = 1
  expand = 3
  formula = Po
  name = G4_Po
  specific = 4
FEATURE [App::DocumentObjectGroupPython] At_element001  label="At_element : 1"  # scripted group (container) (typed FeaturePython)
  n = 1
  ref = At_element
FEATURE [App::DocumentObjectGroupPython] G4_At  # scripted group (container) (typed FeaturePython)
  Dunit = g/cm3
  Dvalue = 9.32
  Group = -> [At_element001]
  conduct = 2
  density = 1
  expand = 3
  formula = At
  name = G4_At
  specific = 4
FEATURE [App::DocumentObjectGroupPython] Rn_element001  label="Rn_element : 1"  # scripted group (container) (typed FeaturePython)
  n = 1
  ref = Rn_element
FEATURE [App::DocumentObjectGroupPython] G4_Rn  # scripted group (container) (typed FeaturePython)
  Dunit = g/cm3
  Dvalue = 0.00900662
  Group = -> [Rn_element001]
  conduct = 2
  density = 1
  expand = 3
  formula = Rn
  name = G4_Rn
  specific = 4
FEATURE [App::DocumentObjectGroupPython] Fr_element001  label="Fr_element : 1"  # scripted group (container) (typed FeaturePython)
  n = 1
  ref = Fr_element
FEATURE [App::DocumentObjectGroupPython] G4_Fr  # scripted group (container) (typed FeaturePython)
  Dunit = g/cm3
  Dvalue = 1
  Group = -> [Fr_element001]
  conduct = 2
  density = 1
  expand = 3
  formula = Fr
  name = G4_Fr
  specific = 4
FEATURE [App::DocumentObjectGroupPython] Ra_element001  label="Ra_element : 1"  # scripted group (container) (typed FeaturePython)
  n = 1
  ref = Ra_element
FEATURE [App::DocumentObjectGroupPython] G4_Ra  # scripted group (container) (typed FeaturePython)
  Dunit = g/cm3
  Dvalue = 5
  Group = -> [Ra_element001]
  conduct = 2
  density = 1
  expand = 3
  formula = Ra
  name = G4_Ra
  specific = 4
FEATURE [App::DocumentObjectGroupPython] Ac_element001  label="Ac_element : 1"  # scripted group (container) (typed FeaturePython)
  n = 1
  ref = Ac_element
FEATURE [App::DocumentObjectGroupPython] G4_Ac  # scripted group (container) (typed FeaturePython)
  Dunit = g/cm3
  Dvalue = 10.07
  Group = -> [Ac_element001]
  conduct = 2
  density = 1
  expand = 3
  formula = Ac
  name = G4_Ac
  specific = 4
FEATURE [App::DocumentObjectGroupPython] Th_element001  label="Th_element : 1"  # scripted group (container) (typed FeaturePython)
  n = 1
  ref = Th_element
FEATURE [App::DocumentObjectGroupPython] G4_Th  # scripted group (container) (typed FeaturePython)
  Dunit = g/cm3
  Dvalue = 11.72
  Group = -> [Th_element001]
  conduct = 2
  density = 1
  expand = 3
  formula = Th
  name = G4_Th
  specific = 4
FEATURE [App::DocumentObjectGroupPython] Pa_element001  label="Pa_element : 1"  # scripted group (container) (typed FeaturePython)
  n = 1
  ref = Pa_element
FEATURE [App::DocumentObjectGroupPython] G4_Pa  # scripted group (container) (typed FeaturePython)
  Dunit = g/cm3
  Dvalue = 15.37
  Group = -> [Pa_element001]
  conduct = 2
  density = 1
  expand = 3
  formula = Pa
  name = G4_Pa
  specific = 4
FEATURE [App::DocumentObjectGroupPython] U_element004  label="U_element : 004"  # scripted group (container) (typed FeaturePython)
  n = 1
  ref = U_element
FEATURE [App::DocumentObjectGroupPython] G4_U  # scripted group (container) (typed FeaturePython)
  Dunit = g/cm3
  Dvalue = 18.95
  Group = -> [U_element004]
  conduct = 2
  density = 1
  expand = 3
  formula = U
  name = G4_U
  specific = 4
FEATURE [App::DocumentObjectGroupPython] Np_element001  label="Np_element : 1"  # scripted group (container) (typed FeaturePython)
  n = 1
  ref = Np_element
FEATURE [App::DocumentObjectGroupPython] G4_Np  # scripted group (container) (typed FeaturePython)
  Dunit = g/cm3
  Dvalue = 20.25
  Group = -> [Np_element001]
  conduct = 2
  density = 1
  expand = 3
  formula = Np
  name = G4_Np
  specific = 4
FEATURE [App::DocumentObjectGroupPython] Pu_element002  label="Pu_element : 002"  # scripted group (container) (typed FeaturePython)
  n = 1
  ref = Pu_element
FEATURE [App::DocumentObjectGroupPython] G4_Pu  # scripted group (container) (typed FeaturePython)
  Dunit = g/cm3
  Dvalue = 19.84
  Group = -> [Pu_element002]
  conduct = 2
  density = 1
  expand = 3
  formula = Pu
  name = G4_Pu
  specific = 4
FEATURE [App::DocumentObjectGroupPython] Am_element001  label="Am_element : 1"  # scripted group (container) (typed FeaturePython)
  n = 1
  ref = Am_element
FEATURE [App::DocumentObjectGroupPython] G4_Am  # scripted group (container) (typed FeaturePython)
  Dunit = g/cm3
  Dvalue = 13.67
  Group = -> [Am_element001]
  conduct = 2
  density = 1
  expand = 3
  formula = Am
  name = G4_Am
  specific = 4
FEATURE [App::DocumentObjectGroupPython] Cm_element001  label="Cm_element : 1"  # scripted group (container) (typed FeaturePython)
  n = 1
  ref = Cm_element
FEATURE [App::DocumentObjectGroupPython] G4_Cm  # scripted group (container) (typed FeaturePython)
  Dunit = g/cm3
  Dvalue = 13.51
  Group = -> [Cm_element001]
  conduct = 2
  density = 1
  expand = 3
  formula = Cm
  name = G4_Cm
  specific = 4
FEATURE [App::DocumentObjectGroupPython] Bk_element001  label="Bk_element : 1"  # scripted group (container) (typed FeaturePython)
  n = 1
  ref = Bk_element
FEATURE [App::DocumentObjectGroupPython] G4_Bk  # scripted group (container) (typed FeaturePython)
  Dunit = g/cm3
  Dvalue = 14
  Group = -> [Bk_element001]
  conduct = 2
  density = 1
  expand = 3
  formula = Bk
  name = G4_Bk
  specific = 4
FEATURE [App::DocumentObjectGroupPython] Cf_element001  label="Cf_element : 1"  # scripted group (container) (typed FeaturePython)
  n = 1
  ref = Cf_element
FEATURE [App::DocumentObjectGroupPython] G4_Cf  # scripted group (container) (typed FeaturePython)
  Dunit = g/cm3
  Dvalue = 10
  Group = -> [Cf_element001]
  conduct = 2
  density = 1
  expand = 3
  formula = Cf
  name = G4_Cf
  specific = 4
FEATURE [App::DocumentObjectGroupPython] Element  # scripted group (container) (typed FeaturePython)
  Group = -> [G4_H,G4_He,G4_Li,G4_Be,G4_B,G4_C,G4_N,G4_O,G4_F,G4_Ne,G4_Na,G4_Mg,G4_Al,G4_Si,G4_P,G4_S,G4_Cl,G4_Ar,G4_K,G4_Ca,G4_Sc,G4_Ti,G4_V,G4_Cr,G4_Mn,G4_Fe,G4_Co,G4_Ni,G4_Cu,G4_Zn,G4_Ga,G4_Ge,G4_As,G4_Se,G4_Br,G4_Kr,G4_Rb,G4_Sr,G4_Y,G4_Zr,G4_Nb,G4_Mo,G4_Tc,G4_Ru,G4_Rh,G4_Pd,G4_Ag,G4_Cd,G4_In,G4_Sn,G4_Sb,G4_Te,G4_I,G4_Xe,G4_Cs,G4_Ba,G4_La,G4_Ce,G4_Pr,G4_Nd,G4_Pm,G4_Sm,G4_Eu,G4_Gd,G4_Tb,G4_Dy,G4_Ho,G4_Er,+30 more]
FEATURE [App::DocumentObjectGroupPython] H_element114  label="H_element : 063"  # scripted group (container) (typed FeaturePython)
  n = 2
  ref = H_element
FEATURE [App::DocumentObjectGroupPython] G4_lH2  # scripted group (container) (typed FeaturePython)
  Dunit = g/cm3
  Dvalue = 0.0708
  Group = -> [H_element114]
  conduct = 2
  density = 1
  expand = 3
  formula = G4_lH2
  name = G4_lH2
  specific = 4
FEATURE [App::DocumentObjectGroupPython] N_element049  label="N_element : 022"  # scripted group (container) (typed FeaturePython)
  n = 2
  ref = N_element
FEATURE [App::DocumentObjectGroupPython] G4_lN2  # scripted group (container) (typed FeaturePython)
  Dunit = g/cm3
  Dvalue = 0.807
  Group = -> [N_element049]
  conduct = 2
  density = 1
  expand = 3
  formula = G4_lN2
  name = G4_lN2
  specific = 4
FEATURE [App::DocumentObjectGroupPython] O_element106  label="O_element : 060"  # scripted group (container) (typed FeaturePython)
  n = 2
  ref = O_element
FEATURE [App::DocumentObjectGroupPython] G4_lO2  # scripted group (container) (typed FeaturePython)
  Dunit = g/cm3
  Dvalue = 1.141
  Group = -> [O_element106]
  conduct = 2
  density = 1
  expand = 3
  formula = G4_lO2
  name = G4_lO2
  specific = 4
FEATURE [App::DocumentObjectGroupPython] Ar  label="Ar : 1"  # scripted group (container) (typed FeaturePython)
  n = 1
  ref = Ar
FEATURE [App::DocumentObjectGroupPython] G4_lAr  # scripted group (container) (typed FeaturePython)
  Dunit = g/cm3
  Dvalue = 1.396
  Group = -> [Ar]
  conduct = 2
  density = 1
  expand = 3
  formula = G4_lAr
  name = G4_lAr
  specific = 4
FEATURE [App::DocumentObjectGroupPython] Br  label="Br : 1"  # scripted group (container) (typed FeaturePython)
  n = 1
  ref = Br
FEATURE [App::DocumentObjectGroupPython] G4_lBr  # scripted group (container) (typed FeaturePython)
  Dunit = g/cm3
  Dvalue = 3.1028
  Group = -> [Br]
  conduct = 2
  density = 1
  expand = 3
  formula = G4_lBr
  name = G4_lBr
  specific = 4
FEATURE [App::DocumentObjectGroupPython] Kr  label="Kr : 1"  # scripted group (container) (typed FeaturePython)
  n = 1
  ref = Kr
FEATURE [App::DocumentObjectGroupPython] G4_lKr  # scripted group (container) (typed FeaturePython)
  Dunit = g/cm3
  Dvalue = 2.418
  Group = -> [Kr]
  conduct = 2
  density = 1
  expand = 3
  formula = G4_lKr
  name = G4_lKr
  specific = 4
FEATURE [App::DocumentObjectGroupPython] Xe  label="Xe : 1"  # scripted group (container) (typed FeaturePython)
  n = 1
  ref = Xe
FEATURE [App::DocumentObjectGroupPython] G4_lXe  # scripted group (container) (typed FeaturePython)
  Dunit = g/cm3
  Dvalue = 2.953
  Group = -> [Xe]
  conduct = 2
  density = 1
  expand = 3
  formula = G4_lXe
  name = G4_lXe
  specific = 4
FEATURE [App::DocumentObjectGroupPython] O_element107  label="O_element : 061"  # scripted group (container) (typed FeaturePython)
  n = 4
  ref = O_element
FEATURE [App::DocumentObjectGroupPython] Pb_element004  label="Pb_element : 002"  # scripted group (container) (typed FeaturePython)
  n = 1
  ref = Pb_element
FEATURE [App::DocumentObjectGroupPython] W_element005  label="W_element : 005"  # scripted group (container) (typed FeaturePython)
  n = 1
  ref = W_element
FEATURE [App::DocumentObjectGroupPython] G4_PbWO4  # scripted group (container) (typed FeaturePython)
  Dunit = g/cm3
  Dvalue = 8.28
  Group = -> [O_element107,Pb_element004,W_element005]
  conduct = 2
  density = 1
  expand = 3
  formula = G4_PbWO4
  name = G4_PbWO4
  specific = 4
FEATURE [App::DocumentObjectGroupPython] alactic  label="alactic : 1"  # scripted group (container) (typed FeaturePython)
  n = 1
  ref = alactic
FEATURE [App::DocumentObjectGroupPython] G4_Galactic  # scripted group (container) (typed FeaturePython)
  Dunit = g/cm3
  Dvalue = 0
  Group = -> [alactic]
  conduct = 2
  density = 1
  expand = 3
  formula = G4_Galactic
  name = G4_Galactic
  specific = 4
FEATURE [App::DocumentObjectGroupPython] RAPHITE_POROUS  label="RAPHITE_POROUS : 1"  # scripted group (container) (typed FeaturePython)
  n = 1
  ref = RAPHITE_POROUS
FEATURE [App::DocumentObjectGroupPython] G4_GRAPHITE_POROUS  # scripted group (container) (typed FeaturePython)
  Dunit = g/cm3
  Dvalue = 1.7
  Group = -> [RAPHITE_POROUS]
  conduct = 2
  density = 1
  expand = 3
  formula = G4_GRAPHITE_POROUS
  name = G4_GRAPHITE_POROUS
  specific = 4
FEATURE [App::DocumentObjectGroupPython] H_element115  label="H_element : 0.150"  # scripted group (container) (typed FeaturePython)
  n = 0.080538
FEATURE [App::DocumentObjectGroupPython] C_element125  label="C_element : 0.600"  # scripted group (container) (typed FeaturePython)
  n = 0.599848
FEATURE [App::DocumentObjectGroupPython] O_element108  label="O_element : 0.320"  # scripted group (container) (typed FeaturePython)
  n = 0.319614
FEATURE [App::DocumentObjectGroupPython] G4_LUCITE  # scripted group (container) (typed FeaturePython)
  Dunit = g/cm3
  Dvalue = 1.19
  Group = -> [H_element115,C_element125,O_element108]
  conduct = 2
  density = 1
  expand = 3
  formula = G4_LUCITE
  name = G4_LUCITE
  specific = 4
FEATURE [App::DocumentObjectGroupPython] Cu_element002  label="Cu_element : 62"  # scripted group (container) (typed FeaturePython)
  n = 62
  ref = Cu_element
FEATURE [App::DocumentObjectGroupPython] Zn_element002  label="Zn_element : 35"  # scripted group (container) (typed FeaturePython)
  n = 35
  ref = Zn_element
FEATURE [App::DocumentObjectGroupPython] Pb_element005  label="Pb_element : 3"  # scripted group (container) (typed FeaturePython)
  n = 3
  ref = Pb_element
FEATURE [App::DocumentObjectGroupPython] G4_BRASS  # scripted group (container) (typed FeaturePython)
  Dunit = g/cm3
  Dvalue = 8.52
  Group = -> [Cu_element002,Zn_element002,Pb_element005]
  conduct = 2
  density = 1
  expand = 3
  formula = G4_BRASS
  name = G4_BRASS
  specific = 4
FEATURE [App::DocumentObjectGroupPython] Cu_element003  label="Cu_element : 89"  # scripted group (container) (typed FeaturePython)
  n = 89
  ref = Cu_element
FEATURE [App::DocumentObjectGroupPython] Zn_element003  label="Zn_element : 9"  # scripted group (container) (typed FeaturePython)
  n = 9
  ref = Zn_element
FEATURE [App::DocumentObjectGroupPython] Pb_element006  label="Pb_element : 2"  # scripted group (container) (typed FeaturePython)
  n = 2
  ref = Pb_element
FEATURE [App::DocumentObjectGroupPython] G4_BRONZE  # scripted group (container) (typed FeaturePython)
  Dunit = g/cm3
  Dvalue = 8.82
  Group = -> [Cu_element003,Zn_element003,Pb_element006]
  conduct = 2
  density = 1
  expand = 3
  formula = G4_BRONZE
  name = G4_BRONZE
  specific = 4
FEATURE [App::DocumentObjectGroupPython] Fe_element008  label="Fe_element : 74"  # scripted group (container) (typed FeaturePython)
  n = 74
  ref = Fe_element
FEATURE [App::DocumentObjectGroupPython] Cr_element002  label="Cr_element : 18"  # scripted group (container) (typed FeaturePython)
  n = 18
  ref = Cr_element
FEATURE [App::DocumentObjectGroupPython] Ni_element002  label="Ni_element : 8"  # scripted group (container) (typed FeaturePython)
  n = 8
  ref = Ni_element
FEATURE [App::DocumentObjectGroupPython] G4_STAINLESS_STEEL  label="G4_STAINLESS-STEEL"  # scripted group (container) (typed FeaturePython)
  Dunit = g/cm3
  Dvalue = 8
  Group = -> [Fe_element008,Cr_element002,Ni_element002]
  conduct = 2
  density = 1
  expand = 3
  formula = G4_STAINLESS-STEEL
  name = G4_STAINLESS-STEEL
  specific = 4
FEATURE [App::DocumentObjectGroupPython] H_element116  label="H_element : 064"  # scripted group (container) (typed FeaturePython)
  n = 18
  ref = H_element
FEATURE [App::DocumentObjectGroupPython] C_element126  label="C_element : 071"  # scripted group (container) (typed FeaturePython)
  n = 12
  ref = C_element
FEATURE [App::DocumentObjectGroupPython] O_element109  label="O_element : 062"  # scripted group (container) (typed FeaturePython)
  n = 7
  ref = O_element
FEATURE [App::DocumentObjectGroupPython] G4_CR39  # scripted group (container) (typed FeaturePython)
  Dunit = g/cm3
  Dvalue = 1.32
  Group = -> [H_element116,C_element126,O_element109]
  conduct = 2
  density = 1
  expand = 3
  formula = G4_CR39
  name = G4_CR39
  specific = 4
FEATURE [App::DocumentObjectGroupPython] H_element117  label="H_element : 38"  # scripted group (container) (typed FeaturePython)
  n = 38
  ref = H_element
FEATURE [App::DocumentObjectGroupPython] C_element127  label="C_element : 072"  # scripted group (container) (typed FeaturePython)
  n = 18
  ref = C_element
FEATURE [App::DocumentObjectGroupPython] O_element110  label="O_element : 063"  # scripted group (container) (typed FeaturePython)
  n = 1
  ref = O_element
FEATURE [App::DocumentObjectGroupPython] G4_OCTADECANOL  # scripted group (container) (typed FeaturePython)
  Dunit = g/cm3
  Dvalue = 0.812
  Group = -> [H_element117,C_element127,O_element110]
  conduct = 2
  density = 1
  expand = 3
  formula = G4_OCTADECANOL
  name = G4_OCTADECANOL
  specific = 4
FEATURE [App::DocumentObjectGroupPython] HEP  # scripted group (container) (typed FeaturePython)
  Group = -> [G4_lH2,G4_lN2,G4_lO2,G4_lAr,G4_lBr,G4_lKr,G4_lXe,G4_PbWO4,G4_Galactic,G4_GRAPHITE_POROUS,G4_LUCITE,G4_BRASS,G4_BRONZE,G4_STAINLESS_STEEL,G4_CR39,G4_OCTADECANOL]
FEATURE [App::DocumentObjectGroupPython] C_element128  label="C_element : 073"  # scripted group (container) (typed FeaturePython)
  n = 14
  ref = C_element
FEATURE [App::DocumentObjectGroupPython] H_element118  label="H_element : 065"  # scripted group (container) (typed FeaturePython)
  n = 10
  ref = H_element
FEATURE [App::DocumentObjectGroupPython] O_element111  label="O_element : 064"  # scripted group (container) (typed FeaturePython)
  n = 2
  ref = O_element
FEATURE [App::DocumentObjectGroupPython] N_element050  label="N_element : 023"  # scripted group (container) (typed FeaturePython)
  n = 2
  ref = N_element
FEATURE [App::DocumentObjectGroupPython] G4_KEVLAR  # scripted group (container) (typed FeaturePython)
  Dunit = g/cm3
  Dvalue = 1.44
  Group = -> [C_element128,H_element118,O_element111,N_element050]
  conduct = 2
  density = 1
  expand = 3
  formula = G4_KEVLAR
  name = G4_KEVLAR
  specific = 4
FEATURE [App::DocumentObjectGroupPython] C_element129  label="C_element : 074"  # scripted group (container) (typed FeaturePython)
  n = 10
  ref = C_element
FEATURE [App::DocumentObjectGroupPython] H_element119  label="H_element : 066"  # scripted group (container) (typed FeaturePython)
  n = 8
  ref = H_element
FEATURE [App::DocumentObjectGroupPython] O_element112  label="O_element : 065"  # scripted group (container) (typed FeaturePython)
  n = 4
  ref = O_element
FEATURE [App::DocumentObjectGroupPython] G4_DACRON  # scripted group (container) (typed FeaturePython)
  Dunit = g/cm3
  Dvalue = 1.4
  Group = -> [C_element129,H_element119,O_element112]
  conduct = 2
  density = 1
  expand = 3
  formula = G4_DACRON
  name = G4_DACRON
  specific = 4
FEATURE [App::DocumentObjectGroupPython] C_element130  label="C_element : 075"  # scripted group (container) (typed FeaturePython)
  n = 4
  ref = C_element
FEATURE [App::DocumentObjectGroupPython] H_element120  label="H_element : 067"  # scripted group (container) (typed FeaturePython)
  n = 5
  ref = H_element
FEATURE [App::DocumentObjectGroupPython] Cl_element030  label="Cl_element : 016"  # scripted group (container) (typed FeaturePython)
  n = 1
  ref = Cl_element
FEATURE [App::DocumentObjectGroupPython] G4_NEOPRENE  # scripted group (container) (typed FeaturePython)
  Dunit = g/cm3
  Dvalue = 1.23
  Group = -> [C_element130,H_element120,Cl_element030]
  conduct = 2
  density = 1
  expand = 3
  formula = G4_NEOPRENE
  name = G4_NEOPRENE
  specific = 4
FEATURE [App::DocumentObjectGroupPython] Space  # scripted group (container) (typed FeaturePython)
  Group = -> [G4_KEVLAR,G4_DACRON,G4_NEOPRENE]
FEATURE [App::DocumentObjectGroupPython] H_element121  label="H_element : 068"  # scripted group (container) (typed FeaturePython)
  n = 5
  ref = H_element
FEATURE [App::DocumentObjectGroupPython] C_element131  label="C_element : 076"  # scripted group (container) (typed FeaturePython)
  n = 4
  ref = C_element
FEATURE [App::DocumentObjectGroupPython] N_element051  label="N_element : 3"  # scripted group (container) (typed FeaturePython)
  n = 3
  ref = N_element
FEATURE [App::DocumentObjectGroupPython] O_element113  label="O_element : 066"  # scripted group (container) (typed FeaturePython)
  n = 1
  ref = O_element
FEATURE [App::DocumentObjectGroupPython] G4_CYTOSINE  # scripted group (container) (typed FeaturePython)
  Dunit = g/cm3
  Dvalue = 1.55
  Group = -> [H_element121,C_element131,N_element051,O_element113]
  conduct = 2
  density = 1
  expand = 3
  formula = G4_CYTOSINE
  name = G4_CYTOSINE
  specific = 4
FEATURE [App::DocumentObjectGroupPython] H_element122  label="H_element : 069"  # scripted group (container) (typed FeaturePython)
  n = 6
  ref = H_element
FEATURE [App::DocumentObjectGroupPython] C_element132  label="C_element : 077"  # scripted group (container) (typed FeaturePython)
  n = 5
  ref = C_element
FEATURE [App::DocumentObjectGroupPython] N_element052  label="N_element : 024"  # scripted group (container) (typed FeaturePython)
  n = 2
  ref = N_element
FEATURE [App::DocumentObjectGroupPython] O_element114  label="O_element : 067"  # scripted group (container) (typed FeaturePython)
  n = 2
  ref = O_element
FEATURE [App::DocumentObjectGroupPython] G4_THYMINE  # scripted group (container) (typed FeaturePython)
  Dunit = g/cm3
  Dvalue = 1.23
  Group = -> [H_element122,C_element132,N_element052,O_element114]
  conduct = 2
  density = 1
  expand = 3
  formula = G4_THYMINE
  name = G4_THYMINE
  specific = 4
FEATURE [App::DocumentObjectGroupPython] H_element123  label="H_element : 070"  # scripted group (container) (typed FeaturePython)
  n = 4
  ref = H_element
FEATURE [App::DocumentObjectGroupPython] C_element133  label="C_element : 078"  # scripted group (container) (typed FeaturePython)
  n = 4
  ref = C_element
FEATURE [App::DocumentObjectGroupPython] N_element053  label="N_element : 025"  # scripted group (container) (typed FeaturePython)
  n = 2
  ref = N_element
FEATURE [App::DocumentObjectGroupPython] O_element115  label="O_element : 068"  # scripted group (container) (typed FeaturePython)
  n = 2
  ref = O_element
FEATURE [App::DocumentObjectGroupPython] G4_URACIL  # scripted group (container) (typed FeaturePython)
  Dunit = g/cm3
  Dvalue = 1.32
  Group = -> [H_element123,C_element133,N_element053,O_element115]
  conduct = 2
  density = 1
  expand = 3
  formula = G4_URACIL
  name = G4_URACIL
  specific = 4
FEATURE [App::DocumentObjectGroupPython] H_element124  label="H_element : 071"  # scripted group (container) (typed FeaturePython)
  n = 4
  ref = H_element
FEATURE [App::DocumentObjectGroupPython] C_element134  label="C_element : 079"  # scripted group (container) (typed FeaturePython)
  n = 5
  ref = C_element
FEATURE [App::DocumentObjectGroupPython] N_element054  label="N_element : 026"  # scripted group (container) (typed FeaturePython)
  n = 5
  ref = N_element
FEATURE [App::DocumentObjectGroupPython] G4_DNA_ADENINE  # scripted group (container) (typed FeaturePython)
  Dunit = g/cm3
  Dvalue = 1
  Group = -> [H_element124,C_element134,N_element054]
  conduct = 2
  density = 1
  expand = 3
  formula = G4_DNA_ADENINE
  name = G4_DNA_ADENINE
  specific = 4
FEATURE [App::DocumentObjectGroupPython] H_element125  label="H_element : 072"  # scripted group (container) (typed FeaturePython)
  n = 4
  ref = H_element
FEATURE [App::DocumentObjectGroupPython] C_element135  label="C_element : 080"  # scripted group (container) (typed FeaturePython)
  n = 5
  ref = C_element
FEATURE [App::DocumentObjectGroupPython] N_element055  label="N_element : 027"  # scripted group (container) (typed FeaturePython)
  n = 5
  ref = N_element
FEATURE [App::DocumentObjectGroupPython] O_element116  label="O_element : 069"  # scripted group (container) (typed FeaturePython)
  n = 1
  ref = O_element
FEATURE [App::DocumentObjectGroupPython] G4_DNA_GUANINE  # scripted group (container) (typed FeaturePython)
  Dunit = g/cm3
  Dvalue = 1
  Group = -> [H_element125,C_element135,N_element055,O_element116]
  conduct = 2
  density = 1
  expand = 3
  formula = G4_DNA_GUANINE
  name = G4_DNA_GUANINE
  specific = 4
FEATURE [App::DocumentObjectGroupPython] H_element126  label="H_element : 073"  # scripted group (container) (typed FeaturePython)
  n = 4
  ref = H_element
FEATURE [App::DocumentObjectGroupPython] C_element136  label="C_element : 081"  # scripted group (container) (typed FeaturePython)
  n = 4
  ref = C_element
FEATURE [App::DocumentObjectGroupPython] N_element056  label="N_element : 028"  # scripted group (container) (typed FeaturePython)
  n = 3
  ref = N_element
FEATURE [App::DocumentObjectGroupPython] O_element117  label="O_element : 070"  # scripted group (container) (typed FeaturePython)
  n = 1
  ref = O_element
FEATURE [App::DocumentObjectGroupPython] G4_DNA_CYTOSINE  # scripted group (container) (typed FeaturePython)
  Dunit = g/cm3
  Dvalue = 1
  Group = -> [H_element126,C_element136,N_element056,O_element117]
  conduct = 2
  density = 1
  expand = 3
  formula = G4_DNA_CYTOSINE
  name = G4_DNA_CYTOSINE
  specific = 4
FEATURE [App::DocumentObjectGroupPython] H_element127  label="H_element : 074"  # scripted group (container) (typed FeaturePython)
  n = 5
  ref = H_element
FEATURE [App::DocumentObjectGroupPython] C_element137  label="C_element : 082"  # scripted group (container) (typed FeaturePython)
  n = 5
  ref = C_element
FEATURE [App::DocumentObjectGroupPython] N_element057  label="N_element : 029"  # scripted group (container) (typed FeaturePython)
  n = 2
  ref = N_element
FEATURE [App::DocumentObjectGroupPython] O_element118  label="O_element : 071"  # scripted group (container) (typed FeaturePython)
  n = 2
  ref = O_element
FEATURE [App::DocumentObjectGroupPython] G4_DNA_THYMINE  # scripted group (container) (typed FeaturePython)
  Dunit = g/cm3
  Dvalue = 1
  Group = -> [H_element127,C_element137,N_element057,O_element118]
  conduct = 2
  density = 1
  expand = 3
  formula = G4_DNA_THYMINE
  name = G4_DNA_THYMINE
  specific = 4
FEATURE [App::DocumentObjectGroupPython] H_element128  label="H_element : 075"  # scripted group (container) (typed FeaturePython)
  n = 3
  ref = H_element
FEATURE [App::DocumentObjectGroupPython] C_element138  label="C_element : 083"  # scripted group (container) (typed FeaturePython)
  n = 4
  ref = C_element
FEATURE [App::DocumentObjectGroupPython] N_element058  label="N_element : 030"  # scripted group (container) (typed FeaturePython)
  n = 2
  ref = N_element
FEATURE [App::DocumentObjectGroupPython] O_element119  label="O_element : 072"  # scripted group (container) (typed FeaturePython)
  n = 2
  ref = O_element
FEATURE [App::DocumentObjectGroupPython] G4_DNA_URACIL  # scripted group (container) (typed FeaturePython)
  Dunit = g/cm3
  Dvalue = 1
  Group = -> [H_element128,C_element138,N_element058,O_element119]
  conduct = 2
  density = 1
  expand = 3
  formula = G4_DNA_URACIL
  name = G4_DNA_URACIL
  specific = 4
FEATURE [App::DocumentObjectGroupPython] H_element129  label="H_element : 076"  # scripted group (container) (typed FeaturePython)
  n = 10
  ref = H_element
FEATURE [App::DocumentObjectGroupPython] C_element139  label="C_element : 084"  # scripted group (container) (typed FeaturePython)
  n = 10
  ref = C_element
FEATURE [App::DocumentObjectGroupPython] N_element059  label="N_element : 031"  # scripted group (container) (typed FeaturePython)
  n = 5
  ref = N_element
FEATURE [App::DocumentObjectGroupPython] O_element120  label="O_element : 073"  # scripted group (container) (typed FeaturePython)
  n = 4
  ref = O_element
FEATURE [App::DocumentObjectGroupPython] G4_DNA_ADENOSINE  # scripted group (container) (typed FeaturePython)
  Dunit = g/cm3
  Dvalue = 1
  Group = -> [H_element129,C_element139,N_element059,O_element120]
  conduct = 2
  density = 1
  expand = 3
  formula = G4_DNA_ADENOSINE
  name = G4_DNA_ADENOSINE
  specific = 4
FEATURE [App::DocumentObjectGroupPython] H_element130  label="H_element : 077"  # scripted group (container) (typed FeaturePython)
  n = 10
  ref = H_element
FEATURE [App::DocumentObjectGroupPython] C_element140  label="C_element : 085"  # scripted group (container) (typed FeaturePython)
  n = 10
  ref = C_element
FEATURE [App::DocumentObjectGroupPython] N_element060  label="N_element : 032"  # scripted group (container) (typed FeaturePython)
  n = 5
  ref = N_element
FEATURE [App::DocumentObjectGroupPython] O_element121  label="O_element : 074"  # scripted group (container) (typed FeaturePython)
  n = 5
  ref = O_element
FEATURE [App::DocumentObjectGroupPython] G4_DNA_GUANOSINE  # scripted group (container) (typed FeaturePython)
  Dunit = g/cm3
  Dvalue = 1
  Group = -> [H_element130,C_element140,N_element060,O_element121]
  conduct = 2
  density = 1
  expand = 3
  formula = G4_DNA_GUANOSINE
  name = G4_DNA_GUANOSINE
  specific = 4
FEATURE [App::DocumentObjectGroupPython] H_element131  label="H_element : 078"  # scripted group (container) (typed FeaturePython)
  n = 10
  ref = H_element
FEATURE [App::DocumentObjectGroupPython] C_element141  label="C_element : 086"  # scripted group (container) (typed FeaturePython)
  n = 9
  ref = C_element
FEATURE [App::DocumentObjectGroupPython] N_element061  label="N_element : 033"  # scripted group (container) (typed FeaturePython)
  n = 3
  ref = N_element
FEATURE [App::DocumentObjectGroupPython] O_element122  label="O_element : 075"  # scripted group (container) (typed FeaturePython)
  n = 5
  ref = O_element
FEATURE [App::DocumentObjectGroupPython] G4_DNA_CYTIDINE  # scripted group (container) (typed FeaturePython)
  Dunit = g/cm3
  Dvalue = 1
  Group = -> [H_element131,C_element141,N_element061,O_element122]
  conduct = 2
  density = 1
  expand = 3
  formula = G4_DNA_CYTIDINE
  name = G4_DNA_CYTIDINE
  specific = 4
FEATURE [App::DocumentObjectGroupPython] H_element132  label="H_element : 079"  # scripted group (container) (typed FeaturePython)
  n = 9
  ref = H_element
FEATURE [App::DocumentObjectGroupPython] C_element142  label="C_element : 087"  # scripted group (container) (typed FeaturePython)
  n = 9
  ref = C_element
FEATURE [App::DocumentObjectGroupPython] N_element062  label="N_element : 034"  # scripted group (container) (typed FeaturePython)
  n = 2
  ref = N_element
FEATURE [App::DocumentObjectGroupPython] O_element123  label="O_element : 076"  # scripted group (container) (typed FeaturePython)
  n = 6
  ref = O_element
FEATURE [App::DocumentObjectGroupPython] G4_DNA_URIDINE  # scripted group (container) (typed FeaturePython)
  Dunit = g/cm3
  Dvalue = 1
  Group = -> [H_element132,C_element142,N_element062,O_element123]
  conduct = 2
  density = 1
  expand = 3
  formula = G4_DNA_URIDINE
  name = G4_DNA_URIDINE
  specific = 4
FEATURE [App::DocumentObjectGroupPython] H_element133  label="H_element : 080"  # scripted group (container) (typed FeaturePython)
  n = 11
  ref = H_element
FEATURE [App::DocumentObjectGroupPython] C_element143  label="C_element : 088"  # scripted group (container) (typed FeaturePython)
  n = 10
  ref = C_element
FEATURE [App::DocumentObjectGroupPython] N_element063  label="N_element : 035"  # scripted group (container) (typed FeaturePython)
  n = 2
  ref = N_element
FEATURE [App::DocumentObjectGroupPython] O_element124  label="O_element : 077"  # scripted group (container) (typed FeaturePython)
  n = 6
  ref = O_element
FEATURE [App::DocumentObjectGroupPython] G4_DNA_METHYLURIDINE  # scripted group (container) (typed FeaturePython)
  Dunit = g/cm3
  Dvalue = 1
  Group = -> [H_element133,C_element143,N_element063,O_element124]
  conduct = 2
  density = 1
  expand = 3
  formula = G4_DNA_METHYLURIDINE
  name = G4_DNA_METHYLURIDINE
  specific = 4
FEATURE [App::DocumentObjectGroupPython] P_element014  label="P_element : 003"  # scripted group (container) (typed FeaturePython)
  n = 1
  ref = P_element
FEATURE [App::DocumentObjectGroupPython] O_element125  label="O_element : 078"  # scripted group (container) (typed FeaturePython)
  n = 3
  ref = O_element
FEATURE [App::DocumentObjectGroupPython] G4_DNA_MONOPHOSPHATE  # scripted group (container) (typed FeaturePython)
  Dunit = g/cm3
  Dvalue = 1
  Group = -> [P_element014,O_element125]
  conduct = 2
  density = 1
  expand = 3
  formula = G4_DNA_MONOPHOSPHATE
  name = G4_DNA_MONOPHOSPHATE
  specific = 4
FEATURE [App::DocumentObjectGroupPython] H_element134  label="H_element : 081"  # scripted group (container) (typed FeaturePython)
  n = 10
  ref = H_element
FEATURE [App::DocumentObjectGroupPython] C_element144  label="C_element : 089"  # scripted group (container) (typed FeaturePython)
  n = 10
  ref = C_element
FEATURE [App::DocumentObjectGroupPython] N_element064  label="N_element : 036"  # scripted group (container) (typed FeaturePython)
  n = 5
  ref = N_element
FEATURE [App::DocumentObjectGroupPython] O_element126  label="O_element : 079"  # scripted group (container) (typed FeaturePython)
  n = 7
  ref = O_element
FEATURE [App::DocumentObjectGroupPython] P_element015  label="P_element : 004"  # scripted group (container) (typed FeaturePython)
  n = 1
  ref = P_element
FEATURE [App::DocumentObjectGroupPython] G4_DNA_A  # scripted group (container) (typed FeaturePython)
  Dunit = g/cm3
  Dvalue = 1
  Group = -> [H_element134,C_element144,N_element064,O_element126,P_element015]
  conduct = 2
  density = 1
  expand = 3
  formula = G4_DNA_A
  name = G4_DNA_A
  specific = 4
FEATURE [App::DocumentObjectGroupPython] H_element135  label="H_element : 082"  # scripted group (container) (typed FeaturePython)
  n = 10
  ref = H_element
FEATURE [App::DocumentObjectGroupPython] C_element145  label="C_element : 090"  # scripted group (container) (typed FeaturePython)
  n = 10
  ref = C_element
FEATURE [App::DocumentObjectGroupPython] N_element065  label="N_element : 037"  # scripted group (container) (typed FeaturePython)
  n = 5
  ref = N_element
FEATURE [App::DocumentObjectGroupPython] O_element127  label="O_element : 8"  # scripted group (container) (typed FeaturePython)
  n = 8
  ref = O_element
FEATURE [App::DocumentObjectGroupPython] P_element016  label="P_element : 005"  # scripted group (container) (typed FeaturePython)
  n = 1
  ref = P_element
FEATURE [App::DocumentObjectGroupPython] G4_DNA_G  # scripted group (container) (typed FeaturePython)
  Dunit = g/cm3
  Dvalue = 1
  Group = -> [H_element135,C_element145,N_element065,O_element127,P_element016]
  conduct = 2
  density = 1
  expand = 3
  formula = G4_DNA_G
  name = G4_DNA_G
  specific = 4
FEATURE [App::DocumentObjectGroupPython] H_element136  label="H_element : 083"  # scripted group (container) (typed FeaturePython)
  n = 10
  ref = H_element
FEATURE [App::DocumentObjectGroupPython] C_element146  label="C_element : 091"  # scripted group (container) (typed FeaturePython)
  n = 9
  ref = C_element
FEATURE [App::DocumentObjectGroupPython] N_element066  label="N_element : 038"  # scripted group (container) (typed FeaturePython)
  n = 3
  ref = N_element
FEATURE [App::DocumentObjectGroupPython] O_element128  label="O_element : 080"  # scripted group (container) (typed FeaturePython)
  n = 8
  ref = O_element
FEATURE [App::DocumentObjectGroupPython] P_element017  label="P_element : 006"  # scripted group (container) (typed FeaturePython)
  n = 1
  ref = P_element
FEATURE [App::DocumentObjectGroupPython] G4_DNA_C  # scripted group (container) (typed FeaturePython)
  Dunit = g/cm3
  Dvalue = 1
  Group = -> [H_element136,C_element146,N_element066,O_element128,P_element017]
  conduct = 2
  density = 1
  expand = 3
  formula = G4_DNA_C
  name = G4_DNA_C
  specific = 4
FEATURE [App::DocumentObjectGroupPython] H_element137  label="H_element : 084"  # scripted group (container) (typed FeaturePython)
  n = 9
  ref = H_element
FEATURE [App::DocumentObjectGroupPython] C_element147  label="C_element : 092"  # scripted group (container) (typed FeaturePython)
  n = 9
  ref = C_element
FEATURE [App::DocumentObjectGroupPython] N_element067  label="N_element : 039"  # scripted group (container) (typed FeaturePython)
  n = 2
  ref = N_element
FEATURE [App::DocumentObjectGroupPython] O_element129  label="O_element : 9"  # scripted group (container) (typed FeaturePython)
  n = 9
  ref = O_element
FEATURE [App::DocumentObjectGroupPython] P_element018  label="P_element : 007"  # scripted group (container) (typed FeaturePython)
  n = 1
  ref = P_element
FEATURE [App::DocumentObjectGroupPython] G4_DNA_U  # scripted group (container) (typed FeaturePython)
  Dunit = g/cm3
  Dvalue = 1
  Group = -> [H_element137,C_element147,N_element067,O_element129,P_element018]
  conduct = 2
  density = 1
  expand = 3
  formula = G4_DNA_U
  name = G4_DNA_U
  specific = 4
FEATURE [App::DocumentObjectGroupPython] H_element138  label="H_element : 085"  # scripted group (container) (typed FeaturePython)
  n = 11
  ref = H_element
FEATURE [App::DocumentObjectGroupPython] C_element148  label="C_element : 093"  # scripted group (container) (typed FeaturePython)
  n = 10
  ref = C_element
FEATURE [App::DocumentObjectGroupPython] N_element068  label="N_element : 040"  # scripted group (container) (typed FeaturePython)
  n = 2
  ref = N_element
FEATURE [App::DocumentObjectGroupPython] O_element130  label="O_element : 081"  # scripted group (container) (typed FeaturePython)
  n = 9
  ref = O_element
FEATURE [App::DocumentObjectGroupPython] P_element019  label="P_element : 008"  # scripted group (container) (typed FeaturePython)
  n = 1
  ref = P_element
FEATURE [App::DocumentObjectGroupPython] G4_DNA_MU  # scripted group (container) (typed FeaturePython)
  Dunit = g/cm3
  Dvalue = 1
  Group = -> [H_element138,C_element148,N_element068,O_element130,P_element019]
  conduct = 2
  density = 1
  expand = 3
  formula = G4_DNA_MU
  name = G4_DNA_MU
  specific = 4
FEATURE [App::DocumentObjectGroupPython] BioChemical  # scripted group (container) (typed FeaturePython)
  Group = -> [G4_CYTOSINE,G4_THYMINE,G4_URACIL,G4_DNA_ADENINE,G4_DNA_GUANINE,G4_DNA_CYTOSINE,G4_DNA_THYMINE,G4_DNA_URACIL,G4_DNA_ADENOSINE,G4_DNA_GUANOSINE,G4_DNA_CYTIDINE,G4_DNA_URIDINE,G4_DNA_METHYLURIDINE,G4_DNA_MONOPHOSPHATE,G4_DNA_A,G4_DNA_G,G4_DNA_C,G4_DNA_U,G4_DNA_MU]
FEATURE [App::DocumentObjectGroupPython] G4Materials  # scripted group (container) (typed FeaturePython)
  Group = -> [NIST,Element,HEP,Space,BioChemical]
  version = 1
FEATURE [App::DocumentObjectGroupPython] Geant4  # scripted group (container) (typed FeaturePython)
  Group = -> [G4Isotopes,G4Elements,G4Materials]
FEATURE [App::DocumentObjectGroupPython] Materials  # scripted group (container) (typed FeaturePython)
  Group = -> [LYSO,Air,Glass,Geant4]
FEATURE [Part::FeaturePython] GDMLBox_World  # WARN: FeaturePython — macro-defined, semantics opaque (R4)
  lunit = 2
  material = 1
  x = 50
  y = 50
  z = 50
FEATURE [Part::FeaturePython] GDMLBox_Obj  # WARN: FeaturePython — macro-defined, semantics opaque (R4)
  lunit = 2
  material = 0
  x = 2
  y = 2
  z = 15
FEATURE [Part::FeaturePython] GDMLBox_GlassPlate  # WARN: FeaturePython — macro-defined, semantics opaque (R4)
  lunit = 2
  material = 2
  x = 2
  y = 2
  z = 2
FEATURE [App::Part] Det
  CopyNumber = 0
  Group = -> [GDMLBox_GlassPlate]
  Origin = -> Origin002
  Placement = pos=(0,0,8.5) rot=(0,0,1;0rad)
  SensDet = PhotonDetector
  SkinSurface = 0
FEATURE [App::FeaturePython] ScintWrap0  # WARN: FeaturePython — macro-defined, semantics opaque (R4)
  PV1 = Obj
  PV2 = Det
  Surface = ScintWrap
FEATURE [App::Part] Obj
  Group = -> [GDMLBox_Obj,Det,ScintWrap0]
  Origin = -> Origin001
  SensDet = Radiator
  SkinSurface = 0
FEATURE [Part::FeaturePython] Array  # Draft array (typed FeaturePython)
  AlwaysSyncPlacement = false
  Angle = 360
  ArrayType = 0
  Axis = (0,0,1)
  Base = -> Obj
  Center = (0,0,0)
  Count = 4
  ExpandArray = false
  Fuse = false
  IntervalAxis = (0,0,0)
  IntervalX = (3,0,0)
  IntervalY = (0,3,0)
  IntervalZ = (0,0,0)
  NumberCircles = 3
  NumberPolar = 5
  NumberX = 2
  NumberY = 2
  NumberZ = 1
  PlacementList = 4 placements: [(0,0,0),(0,3,0),(3,0,0),(3,3,0)]
  RadialDistance = 50
  ScaleList = (4) [(1,1,1),(1,1,1),(1,1,1),(1,1,1)]
  Symmetry = 1
  TangentialDistance = 25
  exportFlag = false
FEATURE [Part::FeaturePython] GDMLBox_Obj001  # WARN: FeaturePython — macro-defined, semantics opaque (R4)
  CopyNumber = 1
  lunit = 2
  material = 0
  x = 2
  y = 2
  z = 15
FEATURE [Part::FeaturePython] GDMLBox_GlassPlate001  # WARN: FeaturePython — macro-defined, semantics opaque (R4)
  CopyNumber = 1
  lunit = 2
  material = 2
  x = 2
  y = 2
  z = 2
FEATURE [App::Part] Det001
  CopyNumber = 1
  Group = -> [GDMLBox_GlassPlate001]
  Origin = -> Origin005
  Placement = pos=(0,0,8.5) rot=(0,0,1;0rad)
FEATURE [App::FeaturePython] ScintWrap001  # WARN: FeaturePython — macro-defined, semantics opaque (R4)
  PV1 = Obj001
  PV2 = Det001
  Surface = ScintWrap
FEATURE [App::Part] Obj001
  CopyNumber = 1
  Group = -> [GDMLBox_Obj001,Det001,ScintWrap001]
  Origin = -> Origin004
FEATURE [App::Link] Link_Obj001
  CopyNumber = 2
  LinkedObject = -> Obj001
FEATURE [App::Link] Link_Obj001001
  CopyNumber = 3
  LinkPlacement = pos=(0,3,0) rot=(0,0,1;0rad)
  LinkedObject = -> Obj001
  Placement = pos=(0,3,0) rot=(0,0,1;0rad)
FEATURE [App::Link] Link_Obj001002
  CopyNumber = 4
  LinkPlacement = pos=(3,0,0) rot=(0,0,1;0rad)
  LinkedObject = -> Obj001
  Placement = pos=(3,0,0) rot=(0,0,1;0rad)
FEATURE [App::Link] Link_Obj001003
  CopyNumber = 5
  LinkPlacement = pos=(3,3,0) rot=(0,0,1;0rad)
  LinkedObject = -> Obj001
  Placement = pos=(3,3,0) rot=(0,0,1;0rad)
FEATURE [App::Part] Array001
  Group = -> [Obj001,Link_Obj001,Link_Obj001001,Link_Obj001002,Link_Obj001003]
  Origin = -> Origin003
FEATURE [App::Part] World
  Group = -> [GDMLBox_World,Obj,Array,Array001]
  Origin = -> Origin
